# Revit family: ESTS-DOAS
name_source: partatom
category: Mechanical Equipment
revit_build: Autodesk Revit 2018 (Build: 20170223_1515(x64)
units: mm (PartAtom-declared; Revit-internal decimal feet)

## family parameters
Always vertical = Yes
Cut with Voids When Loaded = No
Part Type = Normal
Room Calculation Point = No
Round Connector Dimension = Use Radius
Shared = No
Work Plane-Based = No

## types (364) — shared parameters
Connect Dia = 7/8"
Connect V = 1 5/16"
Discharge Offset = 3"
Induct Filter C = 15 3/4"
Induct Filter Thickness = 2"
Induction C = 15"
Inlet Offset = 4"
Inlet S = 5 1/2"
Manufacturer = Anemostat
Pipe Radius = 7/16"

## per-type parameters (varying)
- ESTS/DOAS 1-hp - 16L W/2ROW & Filter: Connect H=1 7/16"; Connect Length=4 1/2"; Connector for 6ROW LS=No; Connector for 6ROW RS=No; Description=DOAS SERIES FAN POWERED AIR TERMINAL; Diameter=15 7/8"; Discharge Height "Y"=16"; Discharge Width "X"=19"; Duct Inlet=8"; Filter LH=No; Filter RH=Yes; Height=20"; Induct Center C=10"; Induct Center D=24"; Induct Filter D=41 3/4"; Induction D=41"; Inlet Left=Yes; Inlet Right=No; Length=48"; Model=ESTS/DOAS; Radius=7 15/16"; Row F=4"; Second Pipe H=1/8"; URL=https://www.anemostat-hvac.com; Width=48"
- ESTS/DOAS 3/4-hp - 14L W/2ROW & Filter: Connect H=1 7/16"; Connect Length=4 1/4"; Connector for 6ROW LS=No; Connector for 6ROW RS=No; Description=DOAS SERIES FAN POWERED AIR TERMINAL; Diameter=13 7/8"; Discharge Height "Y"=16"; Discharge Width "X"=19"; Duct Inlet=7"; Filter LH=No; Filter RH=Yes; Height=20"; Induct Center C=10"; Induct Center D=24"; Induct Filter D=41 3/4"; Induction D=41"; Inlet Left=Yes; Inlet Right=No; Length=48"; Model=ESTS/DOAS; Radius=6 15/16"; Row F=4"; Second Pipe H=1/8"; URL=https://www.anemostat-hvac.com; Width=48"
- ESTS/DOAS 1/2-hp - 14L W/2ROW & Filter: Connect H=1 7/16"; Connect Length=4 1/2"; Connector for 6ROW LS=No; Connector for 6ROW RS=No; Description=DOAS SERIES FAN POWERED AIR TERMINAL; Diameter=13 7/8"; Discharge Height "Y"=12"; Discharge Width "X"=14"; Duct Inlet=7"; Filter LH=No; Filter RH=Yes; Height=18"; Induct Center C=9"; Induct Center D=20"; Induct Filter D=33 3/4"; Induction D=33"; Inlet Left=Yes; Inlet Right=No; Length=40"; Model=ESTS/DOAS; Radius=6 15/16"; Row F=4"; Second Pipe H=1/8"; URL=https://www.anemostat-hvac.com; Width=40"
- ESTS/DOAS 1/3-hp - 10L W/2ROW & Filter: Connect H=1 7/16"; Connect Length=4 1/2"; Connector for 6ROW LS=No; Connector for 6ROW RS=No; Description=DOAS SERIES FAN POWERED AIR TERMINAL; Diameter=9 7/8"; Discharge Height "Y"=11"; Discharge Width "X"=11 1/2"; Duct Inlet=5"; Filter LH=No; Filter RH=Yes; Height=18"; Induct Center C=9"; Induct Center D=18"; Induct Filter D=29 3/4"; Induction D=29"; Inlet Left=Yes; Inlet Right=No; Length=36"; Model=ESTS/DOAS; Radius=4 15/16"; Row F=4"; Second Pipe H=1/8"; URL=https://www.anemostat-hvac.com; Width=32"
- ESTS/DOAS 3/4-hp - 14R W/2ROW & Filter: Connect H=1 7/16"; Connect Length=4 1/4"; Connector for 6ROW LS=No; Connector for 6ROW RS=No; Description=DOAS SERIES FAN POWERED AIR TERMINAL; Diameter=13 7/8"; Discharge Height "Y"=16"; Discharge Width "X"=19"; Duct Inlet=7"; Filter LH=Yes; Filter RH=No; Height=20"; Induct Center C=10"; Induct Center D=24"; Induct Filter D=41 3/4"; Induction D=41"; Inlet Left=No; Inlet Right=Yes; Length=48"; Model=ESTS/DOAS; Radius=6 15/16"; Row F=4"; Second Pipe H=1/8"; URL=https://www.anemostat-hvac.com; Width=48"
- ESTS/DOAS 1-hp - 16R W/2ROW & Filter: Connect H=1 5/16"; Connect Length=4 1/4"; Connector for 6ROW LS=No; Connector for 6ROW RS=No; Description=Series Fan Powered Air Terminal with ECM Motor; Diameter=15 7/8"; Discharge Height "Y"=16"; Discharge Width "X"=19"; Duct Inlet=8"; Filter LH=Yes; Filter RH=No; Height=20"; Induct Center C=10"; Induct Center D=24"; Induct Filter D=41 3/4"; Induction D=41"; Inlet Left=No; Inlet Right=Yes; Length=48"; Model=ESTS; Radius=7 15/16"; Row F=4"; Second Pipe H=1/8"; URL=http://www.anemostat.com; Width=48"
- ESTS/DOAS 1/3-hp - 10R W/2ROW & Filter: Connect H=1 7/16"; Connect Length=4 1/2"; Connector for 6ROW LS=No; Connector for 6ROW RS=No; Description=DOAS SERIES FAN POWERED AIR TERMINAL; Diameter=9 7/8"; Discharge Height "Y"=11"; Discharge Width "X"=11 1/2"; Duct Inlet=5"; Filter LH=Yes; Filter RH=No; Height=18"; Induct Center C=9"; Induct Center D=18"; Induct Filter D=29 3/4"; Induction D=29"; Inlet Left=No; Inlet Right=Yes; Length=36"; Model=ESTS/DOAS; Radius=4 15/16"; Row F=4"; Second Pipe H=1/8"; URL=https://www.anemostat-hvac.com; Width=32"
- ESTS/DOAS 1/2-hp - 14R W/2ROW & Filter: Connect H=1 7/16"; Connect Length=4 1/2"; Connector for 6ROW LS=No; Connector for 6ROW RS=No; Description=DOAS SERIES FAN POWERED AIR TERMINAL; Diameter=13 7/8"; Discharge Height "Y"=12"; Discharge Width "X"=14"; Duct Inlet=7"; Filter LH=Yes; Filter RH=No; Height=18"; Induct Center C=9"; Induct Center D=20"; Induct Filter D=33 3/4"; Induction D=33"; Inlet Left=No; Inlet Right=Yes; Length=40"; Model=ESTS/DOAS; Radius=6 15/16"; Row F=4"; Second Pipe H=1/8"; URL=https://www.anemostat-hvac.com; Width=40"
- ESTS/DOAS 1/3-hp - 09L W/2ROW & Filter: Connect H=1 7/16"; Connect Length=4 1/2"; Connector for 6ROW LS=No; Connector for 6ROW RS=No; Description=DOAS SERIES FAN POWERED AIR TERMINAL; Diameter=8 7/8"; Discharge Height "Y"=11"; Discharge Width "X"=11 1/2"; Duct Inlet=4"; Filter LH=No; Filter RH=Yes; Height=18"; Induct Center C=9"; Induct Center D=18"; Induct Filter D=29 3/4"; Induction D=29"; Inlet Left=Yes; Inlet Right=No; Length=36"; Model=ESTS/DOAS; Radius=4 7/16"; Row F=4"; Second Pipe H=1/8"; URL=https://www.anemostat-hvac.com; Width=32"
- ESTS/DOAS 1/3-hp - 08L W/2ROW & Filter: Connect H=1 7/16"; Connect Length=4 1/2"; Connector for 6ROW LS=No; Connector for 6ROW RS=No; Description=DOAS SERIES FAN POWERED AIR TERMINAL; Diameter=7 7/8"; Discharge Height "Y"=11"; Discharge Width "X"=11 1/2"; Duct Inlet=4"; Filter LH=No; Filter RH=Yes; Height=18"; Induct Center C=9"; Induct Center D=18"; Induct Filter D=29 3/4"; Induction D=29"; Inlet Left=Yes; Inlet Right=No; Length=36"; Model=ESTS/DOAS; Radius=3 15/16"; Row F=4"; Second Pipe H=1/8"; URL=https://www.anemostat-hvac.com; Width=32"
- ESTS/DOAS 1/3-hp - 07L W/2ROW & Filter: Connect H=1 7/16"; Connect Length=4 1/2"; Connector for 6ROW LS=No; Connector for 6ROW RS=No; Description=DOAS SERIES FAN POWERED AIR TERMINAL; Diameter=6 7/8"; Discharge Height "Y"=11"; Discharge Width "X"=11 1/2"; Duct Inlet=3"; Filter LH=No; Filter RH=Yes; Height=18"; Induct Center C=9"; Induct Center D=18"; Induct Filter D=29 3/4"; Induction D=29"; Inlet Left=Yes; Inlet Right=No; Length=36"; Model=ESTS/DOAS; Radius=3 7/16"; Row F=4"; Second Pipe H=1/8"; URL=https://www.anemostat-hvac.com; Width=32"
- ESTS/DOAS 1/3-hp - 06L W/2ROW & Filter: Connect H=1 7/16"; Connect Length=4 1/2"; Connector for 6ROW LS=No; Connector for 6ROW RS=No; Description=DOAS SERIES FAN POWERED AIR TERMINAL; Diameter=5 7/8"; Discharge Height "Y"=11"; Discharge Width "X"=11 1/2"; Duct Inlet=3"; Filter LH=No; Filter RH=Yes; Height=18"; Induct Center C=9"; Induct Center D=18"; Induct Filter D=29 3/4"; Induction D=29"; Inlet Left=Yes; Inlet Right=No; Length=36"; Model=ESTS/DOAS; Radius=2 15/16"; Row F=4"; Second Pipe H=1/8"; URL=https://www.anemostat-hvac.com; Width=32"
- ESTS/DOAS 1/3-hp - 05L W/2ROW & Filter: Connect H=1 7/16"; Connect Length=4 1/2"; Connector for 6ROW LS=No; Connector for 6ROW RS=No; Description=DOAS SERIES FAN POWERED AIR TERMINAL; Diameter=4 7/8"; Discharge Height "Y"=11"; Discharge Width "X"=11 1/2"; Duct Inlet=2"; Filter LH=No; Filter RH=Yes; Height=18"; Induct Center C=9"; Induct Center D=18"; Induct Filter D=29 3/4"; Induction D=29"; Inlet Left=Yes; Inlet Right=No; Length=36"; Model=ESTS/DOAS; Radius=2 7/16"; Row F=4"; Second Pipe H=1/8"; URL=https://www.anemostat-hvac.com; Width=32"
- ESTS/DOAS 1/3-hp - 09R W/2ROW & Filter: Connect H=1 7/16"; Connect Length=4 1/2"; Connector for 6ROW LS=No; Connector for 6ROW RS=No; Description=DOAS SERIES FAN POWERED AIR TERMINAL; Diameter=8 7/8"; Discharge Height "Y"=11"; Discharge Width "X"=11 1/2"; Duct Inlet=4"; Filter LH=Yes; Filter RH=No; Height=18"; Induct Center C=9"; Induct Center D=18"; Induct Filter D=29 3/4"; Induction D=29"; Inlet Left=No; Inlet Right=Yes; Length=36"; Model=ESTS/DOAS; Radius=4 7/16"; Row F=4"; Second Pipe H=1/8"; URL=https://www.anemostat-hvac.com; Width=32"
- ESTS/DOAS 1/3-hp - 08R W/2ROW & Filter: Connect H=1 7/16"; Connect Length=4 1/2"; Connector for 6ROW LS=No; Connector for 6ROW RS=No; Description=DOAS SERIES FAN POWERED AIR TERMINAL; Diameter=7 7/8"; Discharge Height "Y"=11"; Discharge Width "X"=11 1/2"; Duct Inlet=4"; Filter LH=Yes; Filter RH=No; Height=18"; Induct Center C=9"; Induct Center D=18"; Induct Filter D=29 3/4"; Induction D=29"; Inlet Left=No; Inlet Right=Yes; Length=36"; Model=ESTS/DOAS; Radius=3 15/16"; Row F=4"; Second Pipe H=1/8"; URL=https://www.anemostat-hvac.com; Width=32"
- ESTS/DOAS 1/3-hp - 07R W/2ROW & Filter: Connect H=1 7/16"; Connect Length=4 1/2"; Connector for 6ROW LS=No; Connector for 6ROW RS=No; Description=DOAS SERIES FAN POWERED AIR TERMINAL; Diameter=6 7/8"; Discharge Height "Y"=11"; Discharge Width "X"=11 1/2"; Duct Inlet=3"; Filter LH=Yes; Filter RH=No; Height=18"; Induct Center C=9"; Induct Center D=18"; Induct Filter D=29 3/4"; Induction D=29"; Inlet Left=No; Inlet Right=Yes; Length=36"; Model=ESTS/DOAS; Radius=3 7/16"; Row F=4"; Second Pipe H=1/8"; URL=https://www.anemostat-hvac.com; Width=32"
- ESTS/DOAS 1/3-hp - 06R W/2ROW & Filter: Connect H=1 7/16"; Connect Length=4 1/2"; Connector for 6ROW LS=No; Connector for 6ROW RS=No; Description=DOAS SERIES FAN POWERED AIR TERMINAL; Diameter=5 7/8"; Discharge Height "Y"=11"; Discharge Width "X"=11 1/2"; Duct Inlet=3"; Filter LH=Yes; Filter RH=No; Height=18"; Induct Center C=9"; Induct Center D=18"; Induct Filter D=29 3/4"; Induction D=29"; Inlet Left=No; Inlet Right=Yes; Length=36"; Model=ESTS/DOAS; Radius=2 15/16"; Row F=4"; Second Pipe H=1/8"; URL=https://www.anemostat-hvac.com; Width=32"
- ESTS/DOAS 1/3-hp - 05R W/2ROW & Filter: Connect H=1 7/16"; Connect Length=4 1/2"; Connector for 6ROW LS=No; Connector for 6ROW RS=No; Description=DOAS SERIES FAN POWERED AIR TERMINAL; Diameter=4 7/8"; Discharge Height "Y"=11"; Discharge Width "X"=11 1/2"; Duct Inlet=2"; Filter LH=Yes; Filter RH=No; Height=18"; Induct Center C=9"; Induct Center D=18"; Induct Filter D=29 3/4"; Induction D=29"; Inlet Left=No; Inlet Right=Yes; Length=36"; Model=ESTS/DOAS; Radius=2 7/16"; Row F=4"; Second Pipe H=1/8"; URL=https://www.anemostat-hvac.com; Width=32"
- ESTS/DOAS 1/2-hp - 14L W/2ROW NO Filter: Connect H=1 7/16"; Connect Length=4 1/2"; Connector for 6ROW LS=No; Connector for 6ROW RS=No; Description=DOAS SERIES FAN POWERED AIR TERMINAL; Diameter=13 7/8"; Discharge Height "Y"=12"; Discharge Width "X"=14"; Duct Inlet=7"; Filter LH=No; Filter RH=No; Height=18"; Induct Center C=9"; Induct Center D=20"; Induct Filter D=33 3/4"; Induction D=33"; Inlet Left=Yes; Inlet Right=No; Length=40"; Model=ESTS/DOAS; Radius=6 15/16"; Row F=4"; Second Pipe H=1/8"; URL=https://www.anemostat-hvac.com; Width=40"
- ESTS/DOAS 1/3-hp - 10R W/2ROW NO Filter: Connect H=1 7/16"; Connect Length=4 1/2"; Connector for 6ROW LS=No; Connector for 6ROW RS=No; Description=DOAS SERIES FAN POWERED AIR TERMINAL; Diameter=9 7/8"; Discharge Height "Y"=11"; Discharge Width "X"=11 1/2"; Duct Inlet=5"; Filter LH=No; Filter RH=No; Height=18"; Induct Center C=9"; Induct Center D=18"; Induct Filter D=29 3/4"; Induction D=29"; Inlet Left=No; Inlet Right=Yes; Length=36"; Model=ESTS/DOAS; Radius=4 15/16"; Row F=4"; Second Pipe H=1/8"; URL=https://www.anemostat-hvac.com; Width=32"
- ESTS/DOAS 1/3-hp - 10L W/2ROW NO Filter: Connect H=1 7/16"; Connect Length=4 1/2"; Connector for 6ROW LS=No; Connector for 6ROW RS=No; Description=DOAS SERIES FAN POWERED AIR TERMINAL; Diameter=9 7/8"; Discharge Height "Y"=11"; Discharge Width "X"=11 1/2"; Duct Inlet=5"; Filter LH=No; Filter RH=No; Height=18"; Induct Center C=9"; Induct Center D=18"; Induct Filter D=29 3/4"; Induction D=29"; Inlet Left=Yes; Inlet Right=No; Length=36"; Model=ESTS/DOAS; Radius=4 15/16"; Row F=4"; Second Pipe H=1/8"; URL=https://www.anemostat-hvac.com; Width=32"
- ESTS/DOAS 1/3-hp - 09R W/2ROW NO Filter: Connect H=1 7/16"; Connect Length=4 1/2"; Connector for 6ROW LS=No; Connector for 6ROW RS=No; Description=DOAS SERIES FAN POWERED AIR TERMINAL; Diameter=8 7/8"; Discharge Height "Y"=11"; Discharge Width "X"=11 1/2"; Duct Inlet=4"; Filter LH=No; Filter RH=No; Height=18"; Induct Center C=9"; Induct Center D=18"; Induct Filter D=29 3/4"; Induction D=29"; Inlet Left=No; Inlet Right=Yes; Length=36"; Model=ESTS/DOAS; Radius=4 7/16"; Row F=4"; Second Pipe H=1/8"; URL=https://www.anemostat-hvac.com; Width=32"
- ESTS/DOAS 1/3-hp - 09L W/2ROW NO Filter: Connect H=1 7/16"; Connect Length=4 1/2"; Connector for 6ROW LS=No; Connector for 6ROW RS=No; Description=DOAS SERIES FAN POWERED AIR TERMINAL; Diameter=8 7/8"; Discharge Height "Y"=11"; Discharge Width "X"=11 1/2"; Duct Inlet=4"; Filter LH=No; Filter RH=No; Height=18"; Induct Center C=9"; Induct Center D=18"; Induct Filter D=29 3/4"; Induction D=29"; Inlet Left=Yes; Inlet Right=No; Length=36"; Model=ESTS/DOAS; Radius=4 7/16"; Row F=4"; Second Pipe H=1/8"; URL=https://www.anemostat-hvac.com; Width=32"
- ESTS/DOAS 1/3-hp - 08R W/2ROW NO Filter: Connect H=1 7/16"; Connect Length=4 1/2"; Connector for 6ROW LS=No; Connector for 6ROW RS=No; Description=DOAS SERIES FAN POWERED AIR TERMINAL; Diameter=7 7/8"; Discharge Height "Y"=11"; Discharge Width "X"=11 1/2"; Duct Inlet=4"; Filter LH=No; Filter RH=No; Height=18"; Induct Center C=9"; Induct Center D=18"; Induct Filter D=29 3/4"; Induction D=29"; Inlet Left=No; Inlet Right=Yes; Length=36"; Model=ESTS/DOAS; Radius=3 15/16"; Row F=4"; Second Pipe H=1/8"; URL=https://www.anemostat-hvac.com; Width=32"
- ESTS/DOAS 1/3-hp - 08L W/2ROW NO Filter: Connect H=1 7/16"; Connect Length=4 1/2"; Connector for 6ROW LS=No; Connector for 6ROW RS=No; Description=DOAS SERIES FAN POWERED AIR TERMINAL; Diameter=7 7/8"; Discharge Height "Y"=11"; Discharge Width "X"=11 1/2"; Duct Inlet=4"; Filter LH=No; Filter RH=No; Height=18"; Induct Center C=9"; Induct Center D=18"; Induct Filter D=29 3/4"; Induction D=29"; Inlet Left=Yes; Inlet Right=No; Length=36"; Model=ESTS/DOAS; Radius=3 15/16"; Row F=4"; Second Pipe H=1/8"; URL=https://www.anemostat-hvac.com; Width=32"
- ESTS/DOAS 1/3-hp - 07R W/2ROW NO Filter: Connect H=1 7/16"; Connect Length=4 1/2"; Connector for 6ROW LS=No; Connector for 6ROW RS=No; Description=DOAS SERIES FAN POWERED AIR TERMINAL; Diameter=6 7/8"; Discharge Height "Y"=11"; Discharge Width "X"=11 1/2"; Duct Inlet=3"; Filter LH=No; Filter RH=No; Height=18"; Induct Center C=9"; Induct Center D=18"; Induct Filter D=29 3/4"; Induction D=29"; Inlet Left=No; Inlet Right=Yes; Length=36"; Model=ESTS/DOAS; Radius=3 7/16"; Row F=4"; Second Pipe H=1/8"; URL=https://www.anemostat-hvac.com; Width=32"
- ESTS/DOAS 1/3-hp - 07L W/2ROW NO Filter: Connect H=1 7/16"; Connect Length=4 1/2"; Connector for 6ROW LS=No; Connector for 6ROW RS=No; Description=DOAS SERIES FAN POWERED AIR TERMINAL; Diameter=6 7/8"; Discharge Height "Y"=11"; Discharge Width "X"=11 1/2"; Duct Inlet=3"; Filter LH=No; Filter RH=No; Height=18"; Induct Center C=9"; Induct Center D=18"; Induct Filter D=29 3/4"; Induction D=29"; Inlet Left=Yes; Inlet Right=No; Length=36"; Model=ESTS/DOAS; Radius=3 7/16"; Row F=4"; Second Pipe H=1/8"; URL=https://www.anemostat-hvac.com; Width=32"
- ESTS/DOAS 1/3-hp - 06R W/2ROW NO Filter: Connect H=1 7/16"; Connect Length=4 1/2"; Connector for 6ROW LS=No; Connector for 6ROW RS=No; Description=DOAS SERIES FAN POWERED AIR TERMINAL; Diameter=5 7/8"; Discharge Height "Y"=11"; Discharge Width "X"=11 1/2"; Duct Inlet=3"; Filter LH=No; Filter RH=No; Height=18"; Induct Center C=9"; Induct Center D=18"; Induct Filter D=29 3/4"; Induction D=29"; Inlet Left=No; Inlet Right=Yes; Length=36"; Model=ESTS/DOAS; Radius=2 15/16"; Row F=4"; Second Pipe H=1/8"; URL=https://www.anemostat-hvac.com; Width=32"
- ESTS/DOAS 1/3-hp - 06L W/2ROW NO Filter: Connect H=1 7/16"; Connect Length=4 1/2"; Connector for 6ROW LS=No; Connector for 6ROW RS=No; Description=DOAS SERIES FAN POWERED AIR TERMINAL; Diameter=5 7/8"; Discharge Height "Y"=11"; Discharge Width "X"=11 1/2"; Duct Inlet=3"; Filter LH=No; Filter RH=No; Height=18"; Induct Center C=9"; Induct Center D=18"; Induct Filter D=29 3/4"; Induction D=29"; Inlet Left=Yes; Inlet Right=No; Length=36"; Model=ESTS/DOAS; Radius=2 15/16"; Row F=4"; Second Pipe H=1/8"; URL=https://www.anemostat-hvac.com; Width=32"
- ESTS/DOAS 1/3-hp - 05R W/2ROW NO Filter: Connect H=1 7/16"; Connect Length=4 1/2"; Connector for 6ROW LS=No; Connector for 6ROW RS=No; Description=DOAS SERIES FAN POWERED AIR TERMINAL; Diameter=4 7/8"; Discharge Height "Y"=11"; Discharge Width "X"=11 1/2"; Duct Inlet=2"; Filter LH=No; Filter RH=No; Height=18"; Induct Center C=9"; Induct Center D=18"; Induct Filter D=29 3/4"; Induction D=29"; Inlet Left=No; Inlet Right=Yes; Length=36"; Model=ESTS/DOAS; Radius=2 7/16"; Row F=4"; Second Pipe H=1/8"; URL=https://www.anemostat-hvac.com; Width=32"
- ESTS/DOAS 1/3-hp - 05L W/2ROW NO Filter: Connect H=1 7/16"; Connect Length=4 1/2"; Connector for 6ROW LS=No; Connector for 6ROW RS=No; Description=DOAS SERIES FAN POWERED AIR TERMINAL; Diameter=4 7/8"; Discharge Height "Y"=11"; Discharge Width "X"=11 1/2"; Duct Inlet=2"; Filter LH=No; Filter RH=No; Height=18"; Induct Center C=9"; Induct Center D=18"; Induct Filter D=29 3/4"; Induction D=29"; Inlet Left=Yes; Inlet Right=No; Length=36"; Model=ESTS/DOAS; Radius=2 7/16"; Row F=4"; Second Pipe H=1/8"; URL=https://www.anemostat-hvac.com; Width=32"
- ESTS/DOAS 1/2-hp - 14R W/2ROW NO Filter: Connect H=1 7/16"; Connect Length=4 1/2"; Connector for 6ROW LS=No; Connector for 6ROW RS=No; Description=DOAS SERIES FAN POWERED AIR TERMINAL; Diameter=13 7/8"; Discharge Height "Y"=12"; Discharge Width "X"=14"; Duct Inlet=7"; Filter LH=No; Filter RH=No; Height=18"; Induct Center C=9"; Induct Center D=20"; Induct Filter D=33 3/4"; Induction D=33"; Inlet Left=No; Inlet Right=Yes; Length=40"; Model=ESTS/DOAS; Radius=6 15/16"; Row F=4"; Second Pipe H=1/8"; URL=https://www.anemostat-hvac.com; Width=40"
- ESTS/DOAS 3/4-hp - 14R W/2ROW NO Filter: Connect H=1 7/16"; Connect Length=4 1/4"; Connector for 6ROW LS=No; Connector for 6ROW RS=No; Description=DOAS SERIES FAN POWERED AIR TERMINAL; Diameter=13 7/8"; Discharge Height "Y"=16"; Discharge Width "X"=19"; Duct Inlet=7"; Filter LH=No; Filter RH=No; Height=20"; Induct Center C=10"; Induct Center D=24"; Induct Filter D=41 3/4"; Induction D=41"; Inlet Left=No; Inlet Right=Yes; Length=48"; Model=ESTS/DOAS; Radius=6 15/16"; Row F=4"; Second Pipe H=1/8"; URL=https://www.anemostat-hvac.com; Width=48"
- ESTS/DOAS 3/4-hp - 14L W/2ROW NO Filter: Connect H=1 7/16"; Connect Length=4 1/4"; Connector for 6ROW LS=No; Connector for 6ROW RS=Yes; Description=DOAS SERIES FAN POWERED AIR TERMINAL; Diameter=13 7/8"; Discharge Height "Y"=16"; Discharge Width "X"=19"; Duct Inlet=7"; Filter LH=No; Filter RH=No; Height=20"; Induct Center C=10"; Induct Center D=24"; Induct Filter D=41 3/4"; Induction D=41"; Inlet Left=Yes; Inlet Right=No; Length=48"; Model=ESTS/DOAS; Radius=6 15/16"; Row F=4"; Second Pipe H=1/8"; URL=https://www.anemostat-hvac.com; Width=48"
- ESTS/DOAS 1-hp - 16R W/2ROW NO Filter: Connect H=1 5/16"; Connect Length=4 1/4"; Connector for 6ROW LS=No; Connector for 6ROW RS=No; Description=Series Fan Powered Air Terminal with ECM Motor; Diameter=15 7/8"; Discharge Height "Y"=16"; Discharge Width "X"=19"; Duct Inlet=8"; Filter LH=No; Filter RH=No; Height=20"; Induct Center C=10"; Induct Center D=24"; Induct Filter D=41 3/4"; Induction D=41"; Inlet Left=No; Inlet Right=Yes; Length=48"; Model=ESTS; Radius=7 15/16"; Row F=4"; Second Pipe H=1/8"; URL=http://www.anemostat.com; Width=48"
- ESTS/DOAS 1-hp - 14L W/2ROW NO Filter: Connect H=1 7/16"; Connect Length=4 1/4"; Connector for 6ROW LS=No; Connector for 6ROW RS=No; Description=DOAS SERIES FAN POWERED AIR TERMINAL; Diameter=13 7/8"; Discharge Height "Y"=16"; Discharge Width "X"=19"; Duct Inlet=7"; Filter LH=No; Filter RH=No; Height=20"; Induct Center C=10"; Induct Center D=24"; Induct Filter D=41 3/4"; Induction D=41"; Inlet Left=Yes; Inlet Right=No; Length=48"; Model=ESTS/DOAS; Radius=6 15/16"; Row F=4"; Second Pipe H=1/8"; URL=https://www.anemostat-hvac.com; Width=48"
- ESTS/DOAS 1-hp - 12L W/2ROW NO Filter: Connect H=1 7/16"; Connect Length=4 1/2"; Connector for 6ROW LS=No; Connector for 6ROW RS=No; Description=DOAS SERIES FAN POWERED AIR TERMINAL; Diameter=11 7/8"; Discharge Height "Y"=16"; Discharge Width "X"=19"; Duct Inlet=6"; Filter LH=No; Filter RH=No; Height=20"; Induct Center C=10"; Induct Center D=24"; Induct Filter D=41 3/4"; Induction D=41"; Inlet Left=Yes; Inlet Right=No; Length=48"; Model=ESTS/DOAS; Radius=5 15/16"; Row F=4"; Second Pipe H=1/8"; URL=https://www.anemostat-hvac.com; Width=48"
- ESTS/DOAS 1-hp - 14L W/2ROW & Filter: Connect H=1 7/16"; Connect Length=4 1/2"; Connector for 6ROW LS=No; Connector for 6ROW RS=No; Description=DOAS SERIES FAN POWERED AIR TERMINAL; Diameter=13 7/8"; Discharge Height "Y"=16"; Discharge Width "X"=19"; Duct Inlet=7"; Filter LH=No; Filter RH=Yes; Height=20"; Induct Center C=10"; Induct Center D=24"; Induct Filter D=41 3/4"; Induction D=41"; Inlet Left=Yes; Inlet Right=No; Length=48"; Model=ESTS/DOAS; Radius=6 15/16"; Row F=4"; Second Pipe H=1/8"; URL=https://www.anemostat-hvac.com; Width=48"
- ESTS/DOAS 1-hp - 12L W/2ROW & Filter: Connect H=1 7/16"; Connect Length=4 1/2"; Connector for 6ROW LS=No; Connector for 6ROW RS=No; Description=DOAS SERIES FAN POWERED AIR TERMINAL; Diameter=11 7/8"; Discharge Height "Y"=16"; Discharge Width "X"=19"; Duct Inlet=6"; Filter LH=No; Filter RH=Yes; Height=20"; Induct Center C=10"; Induct Center D=24"; Induct Filter D=41 3/4"; Induction D=41"; Inlet Left=Yes; Inlet Right=No; Length=48"; Model=ESTS/DOAS; Radius=5 15/16"; Row F=4"; Second Pipe H=1/8"; URL=https://www.anemostat-hvac.com; Width=48"
- ESTS/DOAS 1-hp - 14R W/2ROW & Filter: Connect H=1 5/16"; Connect Length=4 1/4"; Connector for 6ROW LS=No; Connector for 6ROW RS=No; Description=Series Fan Powered Air Terminal with ECM Motor; Diameter=13 7/8"; Discharge Height "Y"=16"; Discharge Width "X"=19"; Duct Inlet=7"; Filter LH=Yes; Filter RH=No; Height=20"; Induct Center C=10"; Induct Center D=24"; Induct Filter D=41 3/4"; Induction D=41"; Inlet Left=No; Inlet Right=Yes; Length=48"; Model=ESTS; Radius=6 15/16"; Row F=4"; Second Pipe H=1/8"; URL=http://www.anemostat.com; Width=48"
- ESTS/DOAS 1-hp - 12R W/2ROW & Filter: Connect H=1 5/16"; Connect Length=4 1/4"; Connector for 6ROW LS=No; Connector for 6ROW RS=No; Description=Series Fan Powered Air Terminal with ECM Motor; Diameter=11 7/8"; Discharge Height "Y"=16"; Discharge Width "X"=19"; Duct Inlet=6"; Filter LH=Yes; Filter RH=No; Height=20"; Induct Center C=10"; Induct Center D=24"; Induct Filter D=41 3/4"; Induction D=41"; Inlet Left=No; Inlet Right=Yes; Length=48"; Model=ESTS; Radius=5 15/16"; Row F=4"; Second Pipe H=1/8"; URL=http://www.anemostat.com; Width=48"
- ESTS/DOAS 1-hp - 10R W/2ROW & Filter: Connect H=1 5/16"; Connect Length=4 1/4"; Connector for 6ROW LS=No; Connector for 6ROW RS=No; Description=Series Fan Powered Air Terminal with ECM Motor; Diameter=9 7/8"; Discharge Height "Y"=16"; Discharge Width "X"=19"; Duct Inlet=5"; Filter LH=Yes; Filter RH=No; Height=20"; Induct Center C=10"; Induct Center D=24"; Induct Filter D=41 3/4"; Induction D=41"; Inlet Left=No; Inlet Right=Yes; Length=48"; Model=ESTS; Radius=4 15/16"; Row F=4"; Second Pipe H=1/8"; URL=http://www.anemostat.com; Width=48"
- ESTS/DOAS 1-hp - 09R W/2ROW & Filter: Connect H=1 5/16"; Connect Length=4 1/4"; Connector for 6ROW LS=No; Connector for 6ROW RS=No; Description=Series Fan Powered Air Terminal with ECM Motor; Diameter=8 7/8"; Discharge Height "Y"=16"; Discharge Width "X"=19"; Duct Inlet=4"; Filter LH=Yes; Filter RH=No; Height=20"; Induct Center C=10"; Induct Center D=24"; Induct Filter D=41 3/4"; Induction D=41"; Inlet Left=No; Inlet Right=Yes; Length=48"; Model=ESTS; Radius=4 7/16"; Row F=4"; Second Pipe H=1/8"; URL=http://www.anemostat.com; Width=48"
- ESTS/DOAS 1-hp - 08R W/2ROW & Filter: Connect H=1 5/16"; Connect Length=4 1/4"; Connector for 6ROW LS=No; Connector for 6ROW RS=No; Description=Series Fan Powered Air Terminal with ECM Motor; Diameter=7 7/8"; Discharge Height "Y"=16"; Discharge Width "X"=19"; Duct Inlet=4"; Filter LH=Yes; Filter RH=No; Height=20"; Induct Center C=10"; Induct Center D=24"; Induct Filter D=41 3/4"; Induction D=41"; Inlet Left=No; Inlet Right=Yes; Length=48"; Model=ESTS; Radius=3 15/16"; Row F=4"; Second Pipe H=1/8"; URL=http://www.anemostat.com; Width=48"
- ESTS/DOAS 1-hp - 07R W/2ROW & Filter: Connect H=1 5/16"; Connect Length=4 1/4"; Connector for 6ROW LS=No; Connector for 6ROW RS=No; Description=Series Fan Powered Air Terminal with ECM Motor; Diameter=6 7/8"; Discharge Height "Y"=16"; Discharge Width "X"=19"; Duct Inlet=3"; Filter LH=Yes; Filter RH=No; Height=20"; Induct Center C=10"; Induct Center D=24"; Induct Filter D=41 3/4"; Induction D=41"; Inlet Left=No; Inlet Right=Yes; Length=48"; Model=ESTS; Radius=3 7/16"; Row F=4"; Second Pipe H=1/8"; URL=http://www.anemostat.com; Width=48"
- ESTS/DOAS 1-hp - 06R W/2ROW & Filter: Connect H=1 5/16"; Connect Length=4 1/4"; Connector for 6ROW LS=No; Connector for 6ROW RS=No; Description=Series Fan Powered Air Terminal with ECM Motor; Diameter=5 7/8"; Discharge Height "Y"=16"; Discharge Width "X"=19"; Duct Inlet=3"; Filter LH=Yes; Filter RH=No; Height=20"; Induct Center C=10"; Induct Center D=24"; Induct Filter D=41 3/4"; Induction D=41"; Inlet Left=No; Inlet Right=Yes; Length=48"; Model=ESTS; Radius=2 15/16"; Row F=4"; Second Pipe H=1/8"; URL=http://www.anemostat.com; Width=48"
- ESTS/DOAS 1-hp - 05R W/2ROW & Filter: Connect H=1 5/16"; Connect Length=4 1/4"; Connector for 6ROW LS=No; Connector for 6ROW RS=No; Description=Series Fan Powered Air Terminal with ECM Motor; Diameter=4 7/8"; Discharge Height "Y"=16"; Discharge Width "X"=19"; Duct Inlet=2"; Filter LH=No; Filter RH=Yes; Height=20"; Induct Center C=10"; Induct Center D=24"; Induct Filter D=41 3/4"; Induction D=41"; Inlet Left=No; Inlet Right=Yes; Length=48"; Model=ESTS; Radius=2 7/16"; Row F=4"; Second Pipe H=1/8"; URL=http://www.anemostat.com; Width=48"
- ESTS/DOAS 1-hp - 14R W/2ROW NO Filter: Connect H=1 5/16"; Connect Length=4 1/4"; Connector for 6ROW LS=No; Connector for 6ROW RS=No; Description=Series Fan Powered Air Terminal with ECM Motor; Diameter=13 7/8"; Discharge Height "Y"=16"; Discharge Width "X"=19"; Duct Inlet=7"; Filter LH=No; Filter RH=No; Height=20"; Induct Center C=10"; Induct Center D=24"; Induct Filter D=41 3/4"; Induction D=41"; Inlet Left=No; Inlet Right=Yes; Length=48"; Model=ESTS; Radius=6 15/16"; Row F=4"; Second Pipe H=1/8"; URL=http://www.anemostat.com; Width=48"
- ESTS/DOAS 1-hp - 12R W/2ROW NO Filter: Connect H=1 5/16"; Connect Length=4 1/4"; Connector for 6ROW LS=No; Connector for 6ROW RS=No; Description=Series Fan Powered Air Terminal with ECM Motor; Diameter=11 7/8"; Discharge Height "Y"=16"; Discharge Width "X"=19"; Duct Inlet=6"; Filter LH=No; Filter RH=No; Height=20"; Induct Center C=10"; Induct Center D=24"; Induct Filter D=41 3/4"; Induction D=41"; Inlet Left=No; Inlet Right=Yes; Length=48"; Model=ESTS; Radius=5 15/16"; Row F=4"; Second Pipe H=1/8"; URL=http://www.anemostat.com; Width=48"
- ESTS/DOAS 1-hp - 10R W/2ROW NO Filter: Connect H=1 5/16"; Connect Length=4 1/4"; Connector for 6ROW LS=No; Connector for 6ROW RS=No; Description=Series Fan Powered Air Terminal with ECM Motor; Diameter=9 7/8"; Discharge Height "Y"=16"; Discharge Width "X"=19"; Duct Inlet=5"; Filter LH=No; Filter RH=No; Height=20"; Induct Center C=10"; Induct Center D=24"; Induct Filter D=41 3/4"; Induction D=41"; Inlet Left=No; Inlet Right=Yes; Length=48"; Model=ESTS; Radius=4 15/16"; Row F=4"; Second Pipe H=1/8"; URL=http://www.anemostat.com; Width=48"
- ESTS/DOAS 1-hp - 09R W/2ROW NO Filter: Connect H=1 5/16"; Connect Length=4 1/4"; Connector for 6ROW LS=No; Connector for 6ROW RS=No; Description=Series Fan Powered Air Terminal with ECM Motor; Diameter=8 7/8"; Discharge Height "Y"=16"; Discharge Width "X"=19"; Duct Inlet=4"; Filter LH=No; Filter RH=No; Height=20"; Induct Center C=10"; Induct Center D=24"; Induct Filter D=41 3/4"; Induction D=41"; Inlet Left=No; Inlet Right=Yes; Length=48"; Model=ESTS; Radius=4 7/16"; Row F=4"; Second Pipe H=1/8"; URL=http://www.anemostat.com; Width=48"
- ESTS/DOAS 1-hp - 08R W/2ROW NO Filter: Connect H=1 5/16"; Connect Length=4 1/4"; Connector for 6ROW LS=No; Connector for 6ROW RS=No; Description=Series Fan Powered Air Terminal with ECM Motor; Diameter=7 7/8"; Discharge Height "Y"=16"; Discharge Width "X"=19"; Duct Inlet=4"; Filter LH=No; Filter RH=No; Height=20"; Induct Center C=10"; Induct Center D=24"; Induct Filter D=41 3/4"; Induction D=41"; Inlet Left=No; Inlet Right=Yes; Length=48"; Model=ESTS; Radius=3 15/16"; Row F=4"; Second Pipe H=1/8"; URL=http://www.anemostat.com; Width=48"
- ESTS/DOAS 1-hp - 07R W/2ROW NO Filter: Connect H=1 5/16"; Connect Length=4 1/4"; Connector for 6ROW LS=No; Connector for 6ROW RS=No; Description=Series Fan Powered Air Terminal with ECM Motor; Diameter=6 7/8"; Discharge Height "Y"=16"; Discharge Width "X"=19"; Duct Inlet=3"; Filter LH=No; Filter RH=No; Height=20"; Induct Center C=10"; Induct Center D=24"; Induct Filter D=41 3/4"; Induction D=41"; Inlet Left=No; Inlet Right=Yes; Length=48"; Model=ESTS; Radius=3 7/16"; Row F=4"; Second Pipe H=1/8"; URL=http://www.anemostat.com; Width=48"
- ESTS/DOAS 1-hp - 06R W/2ROW NO Filter: Connect H=1 5/16"; Connect Length=4 1/4"; Connector for 6ROW LS=No; Connector for 6ROW RS=No; Description=Series Fan Powered Air Terminal with ECM Motor; Diameter=5 7/8"; Discharge Height "Y"=16"; Discharge Width "X"=19"; Duct Inlet=3"; Filter LH=No; Filter RH=No; Height=20"; Induct Center C=10"; Induct Center D=24"; Induct Filter D=41 3/4"; Induction D=41"; Inlet Left=No; Inlet Right=Yes; Length=48"; Model=ESTS; Radius=2 15/16"; Row F=4"; Second Pipe H=1/8"; URL=http://www.anemostat.com; Width=48"
- ESTS/DOAS 1-hp - 05R W/2ROW NO Filter: Connect H=1 5/16"; Connect Length=4 1/4"; Connector for 6ROW LS=No; Connector for 6ROW RS=No; Description=Series Fan Powered Air Terminal with ECM Motor; Diameter=4 7/8"; Discharge Height "Y"=16"; Discharge Width "X"=19"; Duct Inlet=2"; Filter LH=No; Filter RH=No; Height=20"; Induct Center C=10"; Induct Center D=24"; Induct Filter D=41 3/4"; Induction D=41"; Inlet Left=No; Inlet Right=Yes; Length=48"; Model=ESTS; Radius=2 7/16"; Row F=4"; Second Pipe H=1/8"; URL=http://www.anemostat.com; Width=48"
- ESTS/DOAS 3/4-hp - 12L W/2ROW NO Filter: Connect H=1 7/16"; Connect Length=4 1/4"; Connector for 6ROW LS=No; Connector for 6ROW RS=No; Description=DOAS SERIES FAN POWERED AIR TERMINAL; Diameter=11 7/8"; Discharge Height "Y"=16"; Discharge Width "X"=19"; Duct Inlet=6"; Filter LH=No; Filter RH=No; Height=20"; Induct Center C=10"; Induct Center D=24"; Induct Filter D=41 3/4"; Induction D=41"; Inlet Left=Yes; Inlet Right=No; Length=48"; Model=ESTS/DOAS; Radius=5 15/16"; Row F=4"; Second Pipe H=1/8"; URL=https://www.anemostat-hvac.com; Width=48"
- ESTS/DOAS 3/4-hp - 10L W/2ROW NO Filter: Connect H=1 7/16"; Connect Length=4 1/4"; Connector for 6ROW LS=No; Connector for 6ROW RS=No; Description=DOAS SERIES FAN POWERED AIR TERMINAL; Diameter=9 7/8"; Discharge Height "Y"=16"; Discharge Width "X"=19"; Duct Inlet=5"; Filter LH=No; Filter RH=No; Height=20"; Induct Center C=10"; Induct Center D=24"; Induct Filter D=41 3/4"; Induction D=41"; Inlet Left=Yes; Inlet Right=No; Length=48"; Model=ESTS/DOAS; Radius=4 15/16"; Row F=4"; Second Pipe H=1/8"; URL=https://www.anemostat-hvac.com; Width=48"
- ESTS/DOAS 3/4-hp - 09L W/2ROW NO Filter: Connect H=1 7/16"; Connect Length=4 1/4"; Connector for 6ROW LS=No; Connector for 6ROW RS=Yes; Description=DOAS SERIES FAN POWERED AIR TERMINAL; Diameter=8 7/8"; Discharge Height "Y"=16"; Discharge Width "X"=19"; Duct Inlet=4"; Filter LH=No; Filter RH=No; Height=20"; Induct Center C=10"; Induct Center D=24"; Induct Filter D=41 3/4"; Induction D=41"; Inlet Left=Yes; Inlet Right=No; Length=48"; Model=ESTS/DOAS; Radius=4 7/16"; Row F=4"; Second Pipe H=1/8"; URL=https://www.anemostat-hvac.com; Width=48"
- ESTS/DOAS 3/4-hp - 08L W/2ROW NO Filter: Connect H=1 7/16"; Connect Length=4 1/4"; Connector for 6ROW LS=No; Connector for 6ROW RS=No; Description=DOAS SERIES FAN POWERED AIR TERMINAL; Diameter=7 7/8"; Discharge Height "Y"=16"; Discharge Width "X"=19"; Duct Inlet=4"; Filter LH=No; Filter RH=No; Height=20"; Induct Center C=10"; Induct Center D=24"; Induct Filter D=41 3/4"; Induction D=41"; Inlet Left=Yes; Inlet Right=No; Length=48"; Model=ESTS/DOAS; Radius=3 15/16"; Row F=4"; Second Pipe H=1/8"; URL=https://www.anemostat-hvac.com; Width=48"
- ESTS/DOAS 3/4-hp - 07L W/2ROW NO Filter: Connect H=1 7/16"; Connect Length=4 1/4"; Connector for 6ROW LS=No; Connector for 6ROW RS=No; Description=DOAS SERIES FAN POWERED AIR TERMINAL; Diameter=6 7/8"; Discharge Height "Y"=16"; Discharge Width "X"=19"; Duct Inlet=3"; Filter LH=No; Filter RH=No; Height=20"; Induct Center C=10"; Induct Center D=24"; Induct Filter D=41 3/4"; Induction D=41"; Inlet Left=Yes; Inlet Right=No; Length=48"; Model=ESTS/DOAS; Radius=3 7/16"; Row F=4"; Second Pipe H=1/8"; URL=https://www.anemostat-hvac.com; Width=48"
- ESTS/DOAS 3/4-hp - 06L W/2ROW NO Filter: Connect H=1 7/16"; Connect Length=4 1/4"; Connector for 6ROW LS=No; Connector for 6ROW RS=No; Description=DOAS SERIES FAN POWERED AIR TERMINAL; Diameter=5 7/8"; Discharge Height "Y"=16"; Discharge Width "X"=19"; Duct Inlet=3"; Filter LH=No; Filter RH=No; Height=20"; Induct Center C=10"; Induct Center D=24"; Induct Filter D=41 3/4"; Induction D=41"; Inlet Left=Yes; Inlet Right=No; Length=48"; Model=ESTS/DOAS; Radius=2 15/16"; Row F=4"; Second Pipe H=1/8"; URL=https://www.anemostat-hvac.com; Width=48"
- ESTS/DOAS 3/4-hp - 05L W/2ROW NO Filter: Connect H=1 7/16"; Connect Length=4 1/4"; Connector for 6ROW LS=No; Connector for 6ROW RS=No; Description=DOAS SERIES FAN POWERED AIR TERMINAL; Diameter=4 7/8"; Discharge Height "Y"=16"; Discharge Width "X"=19"; Duct Inlet=2"; Filter LH=No; Filter RH=No; Height=20"; Induct Center C=10"; Induct Center D=24"; Induct Filter D=41 3/4"; Induction D=41"; Inlet Left=Yes; Inlet Right=No; Length=48"; Model=ESTS/DOAS; Radius=2 7/16"; Row F=4"; Second Pipe H=1/8"; URL=https://www.anemostat-hvac.com; Width=48"
- ESTS/DOAS 3/4-hp - 12L W/2ROW & Filter: Connect H=1 7/16"; Connect Length=4 1/4"; Connector for 6ROW LS=No; Connector for 6ROW RS=No; Description=DOAS SERIES FAN POWERED AIR TERMINAL; Diameter=11 7/8"; Discharge Height "Y"=16"; Discharge Width "X"=19"; Duct Inlet=6"; Filter LH=No; Filter RH=Yes; Height=20"; Induct Center C=10"; Induct Center D=24"; Induct Filter D=41 3/4"; Induction D=41"; Inlet Left=Yes; Inlet Right=No; Length=48"; Model=ESTS/DOAS; Radius=5 15/16"; Row F=4"; Second Pipe H=1/8"; URL=https://www.anemostat-hvac.com; Width=48"
- ESTS/DOAS 3/4-hp - 10L W/2ROW & Filter: Connect H=1 7/16"; Connect Length=4 1/4"; Connector for 6ROW LS=No; Connector for 6ROW RS=No; Description=DOAS SERIES FAN POWERED AIR TERMINAL; Diameter=9 7/8"; Discharge Height "Y"=16"; Discharge Width "X"=19"; Duct Inlet=5"; Filter LH=No; Filter RH=Yes; Height=20"; Induct Center C=10"; Induct Center D=24"; Induct Filter D=41 3/4"; Induction D=41"; Inlet Left=Yes; Inlet Right=No; Length=48"; Model=ESTS/DOAS; Radius=4 15/16"; Row F=4"; Second Pipe H=1/8"; URL=https://www.anemostat-hvac.com; Width=48"
- ESTS/DOAS 3/4-hp - 09L W/2ROW & Filter: Connect H=1 7/16"; Connect Length=4 1/4"; Connector for 6ROW LS=No; Connector for 6ROW RS=No; Description=DOAS SERIES FAN POWERED AIR TERMINAL; Diameter=8 7/8"; Discharge Height "Y"=16"; Discharge Width "X"=19"; Duct Inlet=4"; Filter LH=No; Filter RH=Yes; Height=20"; Induct Center C=10"; Induct Center D=24"; Induct Filter D=41 3/4"; Induction D=41"; Inlet Left=Yes; Inlet Right=No; Length=48"; Model=ESTS/DOAS; Radius=4 7/16"; Row F=4"; Second Pipe H=1/8"; URL=https://www.anemostat-hvac.com; Width=48"
- ESTS/DOAS 3/4-hp - 08L W/2ROW & Filter: Connect H=1 7/16"; Connect Length=4 1/4"; Connector for 6ROW LS=No; Connector for 6ROW RS=No; Description=DOAS SERIES FAN POWERED AIR TERMINAL; Diameter=7 7/8"; Discharge Height "Y"=16"; Discharge Width "X"=19"; Duct Inlet=4"; Filter LH=No; Filter RH=Yes; Height=20"; Induct Center C=10"; Induct Center D=24"; Induct Filter D=41 3/4"; Induction D=41"; Inlet Left=Yes; Inlet Right=No; Length=48"; Model=ESTS/DOAS; Radius=3 15/16"; Row F=4"; Second Pipe H=1/8"; URL=https://www.anemostat-hvac.com; Width=48"
- ESTS/DOAS 3/4-hp - 07L W/2ROW & Filter: Connect H=1 7/16"; Connect Length=4 1/4"; Connector for 6ROW LS=No; Connector for 6ROW RS=No; Description=DOAS SERIES FAN POWERED AIR TERMINAL; Diameter=6 7/8"; Discharge Height "Y"=16"; Discharge Width "X"=19"; Duct Inlet=3"; Filter LH=No; Filter RH=Yes; Height=20"; Induct Center C=10"; Induct Center D=24"; Induct Filter D=41 3/4"; Induction D=41"; Inlet Left=Yes; Inlet Right=No; Length=48"; Model=ESTS/DOAS; Radius=3 7/16"; Row F=4"; Second Pipe H=1/8"; URL=https://www.anemostat-hvac.com; Width=48"
- ESTS/DOAS 3/4-hp - 06L W/2ROW & Filter: Connect H=1 7/16"; Connect Length=4 1/4"; Connector for 6ROW LS=No; Connector for 6ROW RS=No; Description=DOAS SERIES FAN POWERED AIR TERMINAL; Diameter=5 7/8"; Discharge Height "Y"=16"; Discharge Width "X"=19"; Duct Inlet=3"; Filter LH=No; Filter RH=Yes; Height=20"; Induct Center C=10"; Induct Center D=24"; Induct Filter D=41 3/4"; Induction D=41"; Inlet Left=Yes; Inlet Right=No; Length=48"; Model=ESTS/DOAS; Radius=2 15/16"; Row F=4"; Second Pipe H=1/8"; URL=https://www.anemostat-hvac.com; Width=48"
- ESTS/DOAS 3/4-hp - 05L W/2ROW & Filter: Connect H=1 7/16"; Connect Length=4 1/4"; Connector for 6ROW LS=No; Connector for 6ROW RS=No; Description=DOAS SERIES FAN POWERED AIR TERMINAL; Diameter=4 7/8"; Discharge Height "Y"=16"; Discharge Width "X"=19"; Duct Inlet=2"; Filter LH=No; Filter RH=Yes; Height=20"; Induct Center C=10"; Induct Center D=24"; Induct Filter D=41 3/4"; Induction D=41"; Inlet Left=Yes; Inlet Right=No; Length=48"; Model=ESTS/DOAS; Radius=2 7/16"; Row F=4"; Second Pipe H=1/8"; URL=https://www.anemostat-hvac.com; Width=48"
- ESTS/DOAS 1/2-hp - 12L W/2ROW & Filter: Connect H=1 7/16"; Connect Length=4 1/2"; Connector for 6ROW LS=No; Connector for 6ROW RS=No; Description=DOAS SERIES FAN POWERED AIR TERMINAL; Diameter=11 7/8"; Discharge Height "Y"=12"; Discharge Width "X"=14"; Duct Inlet=6"; Filter LH=No; Filter RH=Yes; Height=18"; Induct Center C=9"; Induct Center D=20"; Induct Filter D=33 3/4"; Induction D=33"; Inlet Left=Yes; Inlet Right=No; Length=40"; Model=ESTS/DOAS; Radius=5 15/16"; Row F=4"; Second Pipe H=1/8"; URL=https://www.anemostat-hvac.com; Width=40"
- ESTS/DOAS 1/2-hp - 10L W/2ROW & Filter: Connect H=1 7/16"; Connect Length=4 1/2"; Connector for 6ROW LS=No; Connector for 6ROW RS=No; Description=DOAS SERIES FAN POWERED AIR TERMINAL; Diameter=9 7/8"; Discharge Height "Y"=12"; Discharge Width "X"=14"; Duct Inlet=5"; Filter LH=No; Filter RH=Yes; Height=18"; Induct Center C=9"; Induct Center D=20"; Induct Filter D=33 3/4"; Induction D=33"; Inlet Left=Yes; Inlet Right=No; Length=40"; Model=ESTS/DOAS; Radius=4 15/16"; Row F=4"; Second Pipe H=1/8"; URL=https://www.anemostat-hvac.com; Width=40"
- ESTS/DOAS 1/2-hp - 09L W/2ROW & Filter: Connect H=1 7/16"; Connect Length=4 1/2"; Connector for 6ROW LS=No; Connector for 6ROW RS=No; Description=DOAS SERIES FAN POWERED AIR TERMINAL; Diameter=8 7/8"; Discharge Height "Y"=12"; Discharge Width "X"=14"; Duct Inlet=4"; Filter LH=No; Filter RH=Yes; Height=18"; Induct Center C=9"; Induct Center D=20"; Induct Filter D=33 3/4"; Induction D=33"; Inlet Left=Yes; Inlet Right=No; Length=40"; Model=ESTS/DOAS; Radius=4 7/16"; Row F=4"; Second Pipe H=1/8"; URL=https://www.anemostat-hvac.com; Width=40"
- ESTS/DOAS 1/2-hp - 08L W/2ROW & Filter: Connect H=1 7/16"; Connect Length=4 1/2"; Connector for 6ROW LS=No; Connector for 6ROW RS=No; Description=DOAS SERIES FAN POWERED AIR TERMINAL; Diameter=7 7/8"; Discharge Height "Y"=12"; Discharge Width "X"=14"; Duct Inlet=4"; Filter LH=No; Filter RH=Yes; Height=18"; Induct Center C=9"; Induct Center D=20"; Induct Filter D=33 3/4"; Induction D=33"; Inlet Left=Yes; Inlet Right=No; Length=40"; Model=ESTS/DOAS; Radius=3 15/16"; Row F=4"; Second Pipe H=1/8"; URL=https://www.anemostat-hvac.com; Width=40"
- ESTS/DOAS 1/2-hp - 07L W/2ROW & Filter: Connect H=1 7/16"; Connect Length=4 1/2"; Connector for 6ROW LS=No; Connector for 6ROW RS=No; Description=DOAS SERIES FAN POWERED AIR TERMINAL; Diameter=6 7/8"; Discharge Height "Y"=12"; Discharge Width "X"=14"; Duct Inlet=3"; Filter LH=No; Filter RH=Yes; Height=18"; Induct Center C=9"; Induct Center D=20"; Induct Filter D=33 3/4"; Induction D=33"; Inlet Left=Yes; Inlet Right=No; Length=40"; Model=ESTS/DOAS; Radius=3 7/16"; Row F=4"; Second Pipe H=1/8"; URL=https://www.anemostat-hvac.com; Width=40"
- ESTS/DOAS 1/2-hp - 06L W/2ROW & Filter: Connect H=1 7/16"; Connect Length=4 1/2"; Connector for 6ROW LS=No; Connector for 6ROW RS=No; Description=DOAS SERIES FAN POWERED AIR TERMINAL; Diameter=5 7/8"; Discharge Height "Y"=12"; Discharge Width "X"=14"; Duct Inlet=3"; Filter LH=No; Filter RH=Yes; Height=18"; Induct Center C=9"; Induct Center D=20"; Induct Filter D=33 3/4"; Induction D=33"; Inlet Left=Yes; Inlet Right=No; Length=40"; Model=ESTS/DOAS; Radius=2 15/16"; Row F=4"; Second Pipe H=1/8"; URL=https://www.anemostat-hvac.com; Width=40"
- ESTS/DOAS 1/2-hp - 05L W/2ROW & Filter: Connect H=1 7/16"; Connect Length=4 1/2"; Connector for 6ROW LS=No; Connector for 6ROW RS=No; Description=DOAS SERIES FAN POWERED AIR TERMINAL; Diameter=4 7/8"; Discharge Height "Y"=12"; Discharge Width "X"=14"; Duct Inlet=2"; Filter LH=No; Filter RH=Yes; Height=18"; Induct Center C=9"; Induct Center D=20"; Induct Filter D=33 3/4"; Induction D=33"; Inlet Left=Yes; Inlet Right=No; Length=40"; Model=ESTS/DOAS; Radius=2 7/16"; Row F=4"; Second Pipe H=1/8"; URL=https://www.anemostat-hvac.com; Width=40"
- ESTS/DOAS 1/2-hp - 12L W/2ROW NO Filter: Connect H=1 7/16"; Connect Length=4 1/2"; Connector for 6ROW LS=No; Connector for 6ROW RS=No; Description=DOAS SERIES FAN POWERED AIR TERMINAL; Diameter=11 7/8"; Discharge Height "Y"=12"; Discharge Width "X"=14"; Duct Inlet=6"; Filter LH=No; Filter RH=No; Height=18"; Induct Center C=9"; Induct Center D=20"; Induct Filter D=33 3/4"; Induction D=33"; Inlet Left=Yes; Inlet Right=No; Length=40"; Model=ESTS/DOAS; Radius=5 15/16"; Row F=4"; Second Pipe H=1/8"; URL=https://www.anemostat-hvac.com; Width=40"
- ESTS/DOAS 1/2-hp - 10L W/2ROW NO Filter: Connect H=1 7/16"; Connect Length=4 1/2"; Connector for 6ROW LS=No; Connector for 6ROW RS=No; Description=DOAS SERIES FAN POWERED AIR TERMINAL; Diameter=9 7/8"; Discharge Height "Y"=12"; Discharge Width "X"=14"; Duct Inlet=5"; Filter LH=No; Filter RH=No; Height=18"; Induct Center C=9"; Induct Center D=20"; Induct Filter D=33 3/4"; Induction D=33"; Inlet Left=Yes; Inlet Right=No; Length=40"; Model=ESTS/DOAS; Radius=4 15/16"; Row F=4"; Second Pipe H=1/8"; URL=https://www.anemostat-hvac.com; Width=40"
- ESTS/DOAS 1/2-hp - 09L W/2ROW NO Filter: Connect H=1 7/16"; Connect Length=4 1/2"; Connector for 6ROW LS=No; Connector for 6ROW RS=No; Description=DOAS SERIES FAN POWERED AIR TERMINAL; Diameter=8 7/8"; Discharge Height "Y"=12"; Discharge Width "X"=14"; Duct Inlet=4"; Filter LH=No; Filter RH=No; Height=18"; Induct Center C=9"; Induct Center D=20"; Induct Filter D=33 3/4"; Induction D=33"; Inlet Left=Yes; Inlet Right=No; Length=40"; Model=ESTS/DOAS; Radius=4 7/16"; Row F=4"; Second Pipe H=1/8"; URL=https://www.anemostat-hvac.com; Width=40"
- ESTS/DOAS 1/2-hp - 08L W/2ROW NO Filter: Connect H=1 7/16"; Connect Length=4 1/2"; Connector for 6ROW LS=No; Connector for 6ROW RS=No; Description=DOAS SERIES FAN POWERED AIR TERMINAL; Diameter=7 7/8"; Discharge Height "Y"=12"; Discharge Width "X"=14"; Duct Inlet=4"; Filter LH=No; Filter RH=No; Height=18"; Induct Center C=9"; Induct Center D=20"; Induct Filter D=33 3/4"; Induction D=33"; Inlet Left=Yes; Inlet Right=No; Length=40"; Model=ESTS/DOAS; Radius=3 15/16"; Row F=4"; Second Pipe H=1/8"; URL=https://www.anemostat-hvac.com; Width=40"
- ESTS/DOAS 1/2-hp - 07L W/2ROW NO Filter: Connect H=1 7/16"; Connect Length=4 1/2"; Connector for 6ROW LS=No; Connector for 6ROW RS=No; Description=DOAS SERIES FAN POWERED AIR TERMINAL; Diameter=6 7/8"; Discharge Height "Y"=12"; Discharge Width "X"=14"; Duct Inlet=3"; Filter LH=No; Filter RH=No; Height=18"; Induct Center C=9"; Induct Center D=20"; Induct Filter D=33 3/4"; Induction D=33"; Inlet Left=Yes; Inlet Right=No; Length=40"; Model=ESTS/DOAS; Radius=3 7/16"; Row F=4"; Second Pipe H=1/8"; URL=https://www.anemostat-hvac.com; Width=40"
- ESTS/DOAS 1/2-hp - 06L W/2ROW NO Filter: Connect H=1 7/16"; Connect Length=4 1/2"; Connector for 6ROW LS=No; Connector for 6ROW RS=No; Description=DOAS SERIES FAN POWERED AIR TERMINAL; Diameter=5 7/8"; Discharge Height "Y"=12"; Discharge Width "X"=14"; Duct Inlet=3"; Filter LH=No; Filter RH=No; Height=18"; Induct Center C=9"; Induct Center D=20"; Induct Filter D=33 3/4"; Induction D=33"; Inlet Left=Yes; Inlet Right=No; Length=40"; Model=ESTS/DOAS; Radius=2 15/16"; Row F=4"; Second Pipe H=1/8"; URL=https://www.anemostat-hvac.com; Width=40"
- ESTS/DOAS 1/2-hp - 05L W/2ROW NO Filter: Connect H=1 7/16"; Connect Length=4 1/2"; Connector for 6ROW LS=No; Connector for 6ROW RS=No; Description=DOAS SERIES FAN POWERED AIR TERMINAL; Diameter=4 7/8"; Discharge Height "Y"=12"; Discharge Width "X"=14"; Duct Inlet=2"; Filter LH=No; Filter RH=No; Height=18"; Induct Center C=9"; Induct Center D=20"; Induct Filter D=33 3/4"; Induction D=33"; Inlet Left=Yes; Inlet Right=No; Length=40"; Model=ESTS/DOAS; Radius=2 7/16"; Row F=4"; Second Pipe H=1/8"; URL=https://www.anemostat-hvac.com; Width=40"
- ESTS/DOAS 1/2-hp - 12R W/2ROW & Filter: Connect H=1 7/16"; Connect Length=4 1/2"; Connector for 6ROW LS=No; Connector for 6ROW RS=No; Description=DOAS SERIES FAN POWERED AIR TERMINAL; Diameter=11 7/8"; Discharge Height "Y"=12"; Discharge Width "X"=14"; Duct Inlet=6"; Filter LH=Yes; Filter RH=No; Height=18"; Induct Center C=9"; Induct Center D=20"; Induct Filter D=33 3/4"; Induction D=33"; Inlet Left=No; Inlet Right=Yes; Length=40"; Model=ESTS/DOAS; Radius=5 15/16"; Row F=4"; Second Pipe H=1/8"; URL=https://www.anemostat-hvac.com; Width=40"
- ESTS/DOAS 1/2-hp - 10R W/2ROW & Filter: Connect H=1 7/16"; Connect Length=4 1/2"; Connector for 6ROW LS=No; Connector for 6ROW RS=No; Description=DOAS SERIES FAN POWERED AIR TERMINAL; Diameter=9 7/8"; Discharge Height "Y"=12"; Discharge Width "X"=14"; Duct Inlet=5"; Filter LH=Yes; Filter RH=No; Height=18"; Induct Center C=9"; Induct Center D=20"; Induct Filter D=33 3/4"; Induction D=33"; Inlet Left=No; Inlet Right=Yes; Length=40"; Model=ESTS/DOAS; Radius=4 15/16"; Row F=4"; Second Pipe H=1/8"; URL=https://www.anemostat-hvac.com; Width=40"
- ESTS/DOAS 1/2-hp - 09R W/2ROW & Filter: Connect H=1 7/16"; Connect Length=4 1/2"; Connector for 6ROW LS=No; Connector for 6ROW RS=No; Description=DOAS SERIES FAN POWERED AIR TERMINAL; Diameter=8 7/8"; Discharge Height "Y"=12"; Discharge Width "X"=14"; Duct Inlet=4"; Filter LH=Yes; Filter RH=No; Height=18"; Induct Center C=9"; Induct Center D=20"; Induct Filter D=33 3/4"; Induction D=33"; Inlet Left=No; Inlet Right=Yes; Length=40"; Model=ESTS/DOAS; Radius=4 7/16"; Row F=4"; Second Pipe H=1/8"; URL=https://www.anemostat-hvac.com; Width=40"
- ESTS/DOAS 1/2-hp - 08R W/2ROW & Filter: Connect H=1 7/16"; Connect Length=4 1/2"; Connector for 6ROW LS=No; Connector for 6ROW RS=No; Description=DOAS SERIES FAN POWERED AIR TERMINAL; Diameter=7 7/8"; Discharge Height "Y"=12"; Discharge Width "X"=14"; Duct Inlet=4"; Filter LH=Yes; Filter RH=No; Height=18"; Induct Center C=9"; Induct Center D=20"; Induct Filter D=33 3/4"; Induction D=33"; Inlet Left=No; Inlet Right=Yes; Length=40"; Model=ESTS/DOAS; Radius=3 15/16"; Row F=4"; Second Pipe H=1/8"; URL=https://www.anemostat-hvac.com; Width=40"
- ESTS/DOAS 1/2-hp - 07R W/2ROW & Filter: Connect H=1 7/16"; Connect Length=4 1/2"; Connector for 6ROW LS=No; Connector for 6ROW RS=No; Description=DOAS SERIES FAN POWERED AIR TERMINAL; Diameter=6 7/8"; Discharge Height "Y"=12"; Discharge Width "X"=14"; Duct Inlet=3"; Filter LH=Yes; Filter RH=No; Height=18"; Induct Center C=9"; Induct Center D=20"; Induct Filter D=33 3/4"; Induction D=33"; Inlet Left=No; Inlet Right=Yes; Length=40"; Model=ESTS/DOAS; Radius=3 7/16"; Row F=4"; Second Pipe H=1/8"; URL=https://www.anemostat-hvac.com; Width=40"
- ESTS/DOAS 1/2-hp - 06R W/2ROW & Filter: Connect H=1 7/16"; Connect Length=4 1/2"; Connector for 6ROW LS=No; Connector for 6ROW RS=No; Description=DOAS SERIES FAN POWERED AIR TERMINAL; Diameter=5 7/8"; Discharge Height "Y"=12"; Discharge Width "X"=14"; Duct Inlet=3"; Filter LH=Yes; Filter RH=No; Height=18"; Induct Center C=9"; Induct Center D=20"; Induct Filter D=33 3/4"; Induction D=33"; Inlet Left=No; Inlet Right=Yes; Length=40"; Model=ESTS/DOAS; Radius=2 15/16"; Row F=4"; Second Pipe H=1/8"; URL=https://www.anemostat-hvac.com; Width=40"
- ESTS/DOAS 1/2-hp - 05R W/2ROW & Filter: Connect H=1 7/16"; Connect Length=4 1/2"; Connector for 6ROW LS=No; Connector for 6ROW RS=No; Description=DOAS SERIES FAN POWERED AIR TERMINAL; Diameter=4 7/8"; Discharge Height "Y"=12"; Discharge Width "X"=14"; Duct Inlet=2"; Filter LH=Yes; Filter RH=No; Height=18"; Induct Center C=9"; Induct Center D=20"; Induct Filter D=33 3/4"; Induction D=33"; Inlet Left=No; Inlet Right=Yes; Length=40"; Model=ESTS/DOAS; Radius=2 7/16"; Row F=4"; Second Pipe H=1/8"; URL=https://www.anemostat-hvac.com; Width=40"
- ESTS/DOAS 1/2-hp - 12R W/2ROW NO Filter: Connect H=1 7/16"; Connect Length=4 1/2"; Connector for 6ROW LS=No; Connector for 6ROW RS=No; Description=DOAS SERIES FAN POWERED AIR TERMINAL; Diameter=11 7/8"; Discharge Height "Y"=12"; Discharge Width "X"=14"; Duct Inlet=6"; Filter LH=No; Filter RH=No; Height=18"; Induct Center C=9"; Induct Center D=20"; Induct Filter D=33 3/4"; Induction D=33"; Inlet Left=No; Inlet Right=Yes; Length=40"; Model=ESTS/DOAS; Radius=5 15/16"; Row F=4"; Second Pipe H=1/8"; URL=https://www.anemostat-hvac.com; Width=40"
- ESTS/DOAS 1/2-hp - 10R W/2ROW NO Filter: Connect H=1 7/16"; Connect Length=4 1/2"; Connector for 6ROW LS=No; Connector for 6ROW RS=No; Description=DOAS SERIES FAN POWERED AIR TERMINAL; Diameter=9 7/8"; Discharge Height "Y"=12"; Discharge Width "X"=14"; Duct Inlet=5"; Filter LH=No; Filter RH=No; Height=18"; Induct Center C=9"; Induct Center D=20"; Induct Filter D=33 3/4"; Induction D=33"; Inlet Left=No; Inlet Right=Yes; Length=40"; Model=ESTS/DOAS; Radius=4 15/16"; Row F=4"; Second Pipe H=1/8"; URL=https://www.anemostat-hvac.com; Width=40"
- ESTS/DOAS 1/2-hp - 09R W/2ROW NO Filter: Connect H=1 7/16"; Connect Length=4 1/2"; Connector for 6ROW LS=No; Connector for 6ROW RS=No; Description=DOAS SERIES FAN POWERED AIR TERMINAL; Diameter=8 7/8"; Discharge Height "Y"=12"; Discharge Width "X"=14"; Duct Inlet=4"; Filter LH=No; Filter RH=No; Height=18"; Induct Center C=9"; Induct Center D=20"; Induct Filter D=33 3/4"; Induction D=33"; Inlet Left=No; Inlet Right=Yes; Length=40"; Model=ESTS/DOAS; Radius=4 7/16"; Row F=4"; Second Pipe H=1/8"; URL=https://www.anemostat-hvac.com; Width=40"
- ESTS/DOAS 1/2-hp - 08R W/2ROW NO Filter: Connect H=1 7/16"; Connect Length=4 1/2"; Connector for 6ROW LS=No; Connector for 6ROW RS=No; Description=DOAS SERIES FAN POWERED AIR TERMINAL; Diameter=7 7/8"; Discharge Height "Y"=12"; Discharge Width "X"=14"; Duct Inlet=4"; Filter LH=No; Filter RH=No; Height=18"; Induct Center C=9"; Induct Center D=20"; Induct Filter D=33 3/4"; Induction D=33"; Inlet Left=No; Inlet Right=Yes; Length=40"; Model=ESTS/DOAS; Radius=3 15/16"; Row F=4"; Second Pipe H=1/8"; URL=https://www.anemostat-hvac.com; Width=40"
- ESTS/DOAS 1/2-hp - 07R W/2ROW NO Filter: Connect H=1 7/16"; Connect Length=4 1/2"; Connector for 6ROW LS=No; Connector for 6ROW RS=No; Description=DOAS SERIES FAN POWERED AIR TERMINAL; Diameter=6 7/8"; Discharge Height "Y"=12"; Discharge Width "X"=14"; Duct Inlet=3"; Filter LH=No; Filter RH=No; Height=18"; Induct Center C=9"; Induct Center D=20"; Induct Filter D=33 3/4"; Induction D=33"; Inlet Left=No; Inlet Right=Yes; Length=40"; Model=ESTS/DOAS; Radius=3 7/16"; Row F=4"; Second Pipe H=1/8"; URL=https://www.anemostat-hvac.com; Width=40"
- ESTS/DOAS 1/2-hp - 06R W/2ROW NO Filter: Connect H=1 7/16"; Connect Length=4 1/2"; Connector for 6ROW LS=No; Connector for 6ROW RS=No; Description=DOAS SERIES FAN POWERED AIR TERMINAL; Diameter=5 7/8"; Discharge Height "Y"=12"; Discharge Width "X"=14"; Duct Inlet=3"; Filter LH=No; Filter RH=No; Height=18"; Induct Center C=9"; Induct Center D=20"; Induct Filter D=33 3/4"; Induction D=33"; Inlet Left=No; Inlet Right=Yes; Length=40"; Model=ESTS/DOAS; Radius=2 15/16"; Row F=4"; Second Pipe H=1/8"; URL=https://www.anemostat-hvac.com; Width=40"
- ESTS/DOAS 1/2-hp - 05R W/2ROW NO Filter: Connect H=1 7/16"; Connect Length=4 1/2"; Connector for 6ROW LS=No; Connector for 6ROW RS=No; Description=DOAS SERIES FAN POWERED AIR TERMINAL; Diameter=4 7/8"; Discharge Height "Y"=12"; Discharge Width "X"=14"; Duct Inlet=2"; Filter LH=No; Filter RH=No; Height=18"; Induct Center C=9"; Induct Center D=20"; Induct Filter D=33 3/4"; Induction D=33"; Inlet Left=No; Inlet Right=Yes; Length=40"; Model=ESTS/DOAS; Radius=2 7/16"; Row F=4"; Second Pipe H=1/8"; URL=https://www.anemostat-hvac.com; Width=40"
- ESTS/DOAS 3/4-hp - 14R W/4ROW NO Filter: Connect H=1 7/16"; Connect Length=4 1/4"; Connector for 6ROW LS=No; Connector for 6ROW RS=No; Description=DOAS SERIES FAN POWERED AIR TERMINAL; Diameter=13 7/8"; Discharge Height "Y"=16"; Discharge Width "X"=19"; Duct Inlet=7"; Filter LH=No; Filter RH=No; Height=20"; Induct Center C=10"; Induct Center D=24"; Induct Filter D=41 3/4"; Induction D=41"; Inlet Left=No; Inlet Right=Yes; Length=48"; Model=ESTS/DOAS; Radius=6 15/16"; Row F=6"; Second Pipe H=2 1/8"; URL=https://www.anemostat-hvac.com; Width=48"
- ESTS/DOAS 3/4-hp - 14R W/4ROW & Filter: Connect H=1 7/16"; Connect Length=4 1/4"; Connector for 6ROW LS=No; Connector for 6ROW RS=No; Description=DOAS SERIES FAN POWERED AIR TERMINAL; Diameter=13 7/8"; Discharge Height "Y"=16"; Discharge Width "X"=19"; Duct Inlet=7"; Filter LH=Yes; Filter RH=No; Height=20"; Induct Center C=10"; Induct Center D=24"; Induct Filter D=41 3/4"; Induction D=41"; Inlet Left=No; Inlet Right=Yes; Length=48"; Model=ESTS/DOAS; Radius=6 15/16"; Row F=6"; Second Pipe H=2 1/8"; URL=https://www.anemostat-hvac.com; Width=48"
- ESTS/DOAS 3/4-hp - 14L W/4ROW NO Filter: Connect H=1 7/16"; Connect Length=4 1/4"; Connector for 6ROW LS=No; Connector for 6ROW RS=No; Description=DOAS SERIES FAN POWERED AIR TERMINAL; Diameter=13 7/8"; Discharge Height "Y"=16"; Discharge Width "X"=19"; Duct Inlet=7"; Filter LH=No; Filter RH=No; Height=20"; Induct Center C=10"; Induct Center D=24"; Induct Filter D=41 3/4"; Induction D=41"; Inlet Left=Yes; Inlet Right=No; Length=48"; Model=ESTS/DOAS; Radius=6 15/16"; Row F=6"; Second Pipe H=2 1/8"; URL=https://www.anemostat-hvac.com; Width=48"
- ESTS/DOAS 3/4-hp - 14L W/6ROW NO Filter: Connect H=1 7/16"; Connect Length=4 1/4"; Connector for 6ROW LS=No; Connector for 6ROW RS=Yes; Description=DOAS SERIES FAN POWERED AIR TERMINAL; Diameter=13 7/8"; Discharge Height "Y"=16"; Discharge Width "X"=19"; Duct Inlet=7"; Filter LH=No; Filter RH=No; Height=20"; Induct Center C=10"; Induct Center D=24"; Induct Filter D=41 3/4"; Induction D=41"; Inlet Left=Yes; Inlet Right=No; Length=48"; Model=ESTS/DOAS; Radius=6 15/16"; Row F=8"; Second Pipe H=4 1/8"; URL=https://www.anemostat-hvac.com; Width=48"
- ESTS/DOAS 3/4-hp - 14R W/6ROW NO Filter: Connect H=1 7/16"; Connect Length=4 1/4"; Connector for 6ROW LS=Yes; Connector for 6ROW RS=No; Description=DOAS SERIES FAN POWERED AIR TERMINAL; Diameter=13 7/8"; Discharge Height "Y"=16"; Discharge Width "X"=19"; Duct Inlet=7"; Filter LH=No; Filter RH=No; Height=20"; Induct Center C=10"; Induct Center D=24"; Induct Filter D=41 3/4"; Induction D=41"; Inlet Left=No; Inlet Right=Yes; Length=48"; Model=ESTS/DOAS; Radius=6 15/16"; Row F=8"; Second Pipe H=4 1/8"; URL=https://www.anemostat-hvac.com; Width=48"
- ESTS/DOAS 3/4-hp - 14R W/6ROW & Filter: Connect H=1 7/16"; Connect Length=4 1/4"; Connector for 6ROW LS=Yes; Connector for 6ROW RS=No; Description=DOAS SERIES FAN POWERED AIR TERMINAL; Diameter=13 7/8"; Discharge Height "Y"=16"; Discharge Width "X"=19"; Duct Inlet=7"; Filter LH=Yes; Filter RH=No; Height=20"; Induct Center C=10"; Induct Center D=24"; Induct Filter D=41 3/4"; Induction D=41"; Inlet Left=No; Inlet Right=Yes; Length=48"; Model=ESTS/DOAS; Radius=6 15/16"; Row F=8"; Second Pipe H=4 1/8"; URL=https://www.anemostat-hvac.com; Width=48"
- ESTS/DOAS 3/4-hp - 14L W/4ROW & Filter: Connect H=1 7/16"; Connect Length=4 1/4"; Connector for 6ROW LS=No; Connector for 6ROW RS=No; Description=DOAS SERIES FAN POWERED AIR TERMINAL; Diameter=13 7/8"; Discharge Height "Y"=16"; Discharge Width "X"=19"; Duct Inlet=7"; Filter LH=No; Filter RH=Yes; Height=20"; Induct Center C=10"; Induct Center D=24"; Induct Filter D=41 3/4"; Induction D=41"; Inlet Left=Yes; Inlet Right=No; Length=48"; Model=ESTS/DOAS; Radius=6 15/16"; Row F=6"; Second Pipe H=2 1/8"; URL=https://www.anemostat-hvac.com; Width=48"
- ESTS/DOAS 3/4-hp - 14L W/6ROW & Filter: Connect H=1 7/16"; Connect Length=4 1/4"; Connector for 6ROW LS=No; Connector for 6ROW RS=Yes; Description=DOAS SERIES FAN POWERED AIR TERMINAL; Diameter=13 7/8"; Discharge Height "Y"=16"; Discharge Width "X"=19"; Duct Inlet=7"; Filter LH=No; Filter RH=Yes; Height=20"; Induct Center C=10"; Induct Center D=24"; Induct Filter D=41 3/4"; Induction D=41"; Inlet Left=Yes; Inlet Right=No; Length=48"; Model=ESTS/DOAS; Radius=6 15/16"; Row F=8"; Second Pipe H=4 1/8"; URL=https://www.anemostat-hvac.com; Width=48"
- ESTS/DOAS 3/4-hp - 12L W/4ROW & Filter: Connect H=1 7/16"; Connect Length=4 1/4"; Connector for 6ROW LS=No; Connector for 6ROW RS=No; Description=DOAS SERIES FAN POWERED AIR TERMINAL; Diameter=11 7/8"; Discharge Height "Y"=16"; Discharge Width "X"=19"; Duct Inlet=6"; Filter LH=No; Filter RH=Yes; Height=20"; Induct Center C=10"; Induct Center D=24"; Induct Filter D=41 3/4"; Induction D=41"; Inlet Left=Yes; Inlet Right=No; Length=48"; Model=ESTS/DOAS; Radius=5 15/16"; Row F=6"; Second Pipe H=2 1/8"; URL=https://www.anemostat-hvac.com; Width=48"
- ESTS/DOAS 3/4-hp - 12L W/6ROW & Filter: Connect H=1 7/16"; Connect Length=4 1/4"; Connector for 6ROW LS=No; Connector for 6ROW RS=Yes; Description=DOAS SERIES FAN POWERED AIR TERMINAL; Diameter=11 7/8"; Discharge Height "Y"=16"; Discharge Width "X"=19"; Duct Inlet=6"; Filter LH=No; Filter RH=Yes; Height=20"; Induct Center C=10"; Induct Center D=24"; Induct Filter D=41 3/4"; Induction D=41"; Inlet Left=Yes; Inlet Right=No; Length=48"; Model=ESTS/DOAS; Radius=5 15/16"; Row F=8"; Second Pipe H=4 1/8"; URL=https://www.anemostat-hvac.com; Width=48"
- ESTS/DOAS 3/4-hp - 12L W/4ROW NO Filter: Connect H=1 7/16"; Connect Length=4 1/4"; Connector for 6ROW LS=No; Connector for 6ROW RS=No; Description=DOAS SERIES FAN POWERED AIR TERMINAL; Diameter=11 7/8"; Discharge Height "Y"=16"; Discharge Width "X"=19"; Duct Inlet=6"; Filter LH=No; Filter RH=No; Height=20"; Induct Center C=10"; Induct Center D=24"; Induct Filter D=41 3/4"; Induction D=41"; Inlet Left=Yes; Inlet Right=No; Length=48"; Model=ESTS/DOAS; Radius=5 15/16"; Row F=6"; Second Pipe H=2 1/8"; URL=https://www.anemostat-hvac.com; Width=48"
- ESTS/DOAS 3/4-hp - 12L W/6ROW NO Filter: Connect H=1 7/16"; Connect Length=4 1/4"; Connector for 6ROW LS=No; Connector for 6ROW RS=Yes; Description=DOAS SERIES FAN POWERED AIR TERMINAL; Diameter=11 7/8"; Discharge Height "Y"=16"; Discharge Width "X"=19"; Duct Inlet=6"; Filter LH=No; Filter RH=No; Height=20"; Induct Center C=10"; Induct Center D=24"; Induct Filter D=41 3/4"; Induction D=41"; Inlet Left=Yes; Inlet Right=No; Length=48"; Model=ESTS/DOAS; Radius=5 15/16"; Row F=8"; Second Pipe H=4 1/8"; URL=https://www.anemostat-hvac.com; Width=48"
- ESTS/DOAS 3/4-hp - 12R W/2ROW & Filter: Connect H=1 7/16"; Connect Length=4 1/4"; Connector for 6ROW LS=No; Connector for 6ROW RS=No; Description=DOAS SERIES FAN POWERED AIR TERMINAL; Diameter=11 7/8"; Discharge Height "Y"=16"; Discharge Width "X"=19"; Duct Inlet=6"; Filter LH=Yes; Filter RH=No; Height=20"; Induct Center C=10"; Induct Center D=24"; Induct Filter D=41 3/4"; Induction D=41"; Inlet Left=No; Inlet Right=Yes; Length=48"; Model=ESTS/DOAS; Radius=5 15/16"; Row F=4"; Second Pipe H=1/8"; URL=https://www.anemostat-hvac.com; Width=48"
- ESTS/DOAS 3/4-hp - 12R W/4ROW & Filter: Connect H=1 7/16"; Connect Length=4 1/4"; Connector for 6ROW LS=No; Connector for 6ROW RS=No; Description=DOAS SERIES FAN POWERED AIR TERMINAL; Diameter=11 7/8"; Discharge Height "Y"=16"; Discharge Width "X"=19"; Duct Inlet=6"; Filter LH=Yes; Filter RH=No; Height=20"; Induct Center C=10"; Induct Center D=24"; Induct Filter D=41 3/4"; Induction D=41"; Inlet Left=No; Inlet Right=Yes; Length=48"; Model=ESTS/DOAS; Radius=5 15/16"; Row F=6"; Second Pipe H=2 1/8"; URL=https://www.anemostat-hvac.com; Width=48"
- ESTS/DOAS 3/4-hp - 12R W/6ROW & Filter: Connect H=1 7/16"; Connect Length=4 1/4"; Connector for 6ROW LS=Yes; Connector for 6ROW RS=No; Description=DOAS SERIES FAN POWERED AIR TERMINAL; Diameter=11 7/8"; Discharge Height "Y"=16"; Discharge Width "X"=19"; Duct Inlet=6"; Filter LH=Yes; Filter RH=No; Height=20"; Induct Center C=10"; Induct Center D=24"; Induct Filter D=41 3/4"; Induction D=41"; Inlet Left=No; Inlet Right=Yes; Length=48"; Model=ESTS/DOAS; Radius=5 15/16"; Row F=8"; Second Pipe H=4 1/8"; URL=https://www.anemostat-hvac.com; Width=48"
- ESTS/DOAS 3/4-hp - 12R W/2ROW NO Filter: Connect H=1 7/16"; Connect Length=4 1/4"; Connector for 6ROW LS=No; Connector for 6ROW RS=No; Description=DOAS SERIES FAN POWERED AIR TERMINAL; Diameter=11 7/8"; Discharge Height "Y"=16"; Discharge Width "X"=19"; Duct Inlet=6"; Filter LH=No; Filter RH=No; Height=20"; Induct Center C=10"; Induct Center D=24"; Induct Filter D=41 3/4"; Induction D=41"; Inlet Left=No; Inlet Right=Yes; Length=48"; Model=ESTS/DOAS; Radius=5 15/16"; Row F=4"; Second Pipe H=1/8"; URL=https://www.anemostat-hvac.com; Width=48"
- ESTS/DOAS 3/4-hp - 12R W/4ROW NO Filter: Connect H=1 7/16"; Connect Length=4 1/4"; Connector for 6ROW LS=No; Connector for 6ROW RS=No; Description=DOAS SERIES FAN POWERED AIR TERMINAL; Diameter=11 7/8"; Discharge Height "Y"=16"; Discharge Width "X"=19"; Duct Inlet=6"; Filter LH=No; Filter RH=No; Height=20"; Induct Center C=10"; Induct Center D=24"; Induct Filter D=41 3/4"; Induction D=41"; Inlet Left=No; Inlet Right=Yes; Length=48"; Model=ESTS/DOAS; Radius=5 15/16"; Row F=6"; Second Pipe H=2 1/8"; URL=https://www.anemostat-hvac.com; Width=48"
- ESTS/DOAS 3/4-hp - 12R W/6ROW NO Filter: Connect H=1 7/16"; Connect Length=4 1/4"; Connector for 6ROW LS=Yes; Connector for 6ROW RS=No; Description=DOAS SERIES FAN POWERED AIR TERMINAL; Diameter=11 7/8"; Discharge Height "Y"=16"; Discharge Width "X"=19"; Duct Inlet=6"; Filter LH=No; Filter RH=No; Height=20"; Induct Center C=10"; Induct Center D=24"; Induct Filter D=41 3/4"; Induction D=41"; Inlet Left=No; Inlet Right=Yes; Length=48"; Model=ESTS/DOAS; Radius=5 15/16"; Row F=8"; Second Pipe H=4 1/8"; URL=https://www.anemostat-hvac.com; Width=48"
- ESTS/DOAS 3/4-hp - 10R W/2ROW & Filter: Connect H=1 7/16"; Connect Length=4 1/4"; Connector for 6ROW LS=No; Connector for 6ROW RS=No; Description=DOAS SERIES FAN POWERED AIR TERMINAL; Diameter=9 7/8"; Discharge Height "Y"=16"; Discharge Width "X"=19"; Duct Inlet=5"; Filter LH=Yes; Filter RH=No; Height=20"; Induct Center C=10"; Induct Center D=24"; Induct Filter D=41 3/4"; Induction D=41"; Inlet Left=No; Inlet Right=Yes; Length=48"; Model=ESTS/DOAS; Radius=4 15/16"; Row F=4"; Second Pipe H=1/8"; URL=https://www.anemostat-hvac.com; Width=48"
- ESTS/DOAS 3/4-hp - 10R W/4ROW & Filter: Connect H=1 7/16"; Connect Length=4 1/4"; Connector for 6ROW LS=No; Connector for 6ROW RS=No; Description=DOAS SERIES FAN POWERED AIR TERMINAL; Diameter=9 7/8"; Discharge Height "Y"=16"; Discharge Width "X"=19"; Duct Inlet=5"; Filter LH=Yes; Filter RH=No; Height=20"; Induct Center C=10"; Induct Center D=24"; Induct Filter D=41 3/4"; Induction D=41"; Inlet Left=No; Inlet Right=Yes; Length=48"; Model=ESTS/DOAS; Radius=4 15/16"; Row F=6"; Second Pipe H=2 1/8"; URL=https://www.anemostat-hvac.com; Width=48"
- ESTS/DOAS 3/4-hp - 10R W/6ROW & Filter: Connect H=1 7/16"; Connect Length=4 1/4"; Connector for 6ROW LS=Yes; Connector for 6ROW RS=No; Description=DOAS SERIES FAN POWERED AIR TERMINAL; Diameter=9 7/8"; Discharge Height "Y"=16"; Discharge Width "X"=19"; Duct Inlet=5"; Filter LH=Yes; Filter RH=No; Height=20"; Induct Center C=10"; Induct Center D=24"; Induct Filter D=41 3/4"; Induction D=41"; Inlet Left=No; Inlet Right=Yes; Length=48"; Model=ESTS/DOAS; Radius=4 15/16"; Row F=8"; Second Pipe H=4 1/8"; URL=https://www.anemostat-hvac.com; Width=48"
- ESTS/DOAS 3/4-hp - 10R W/2ROW NO Filter: Connect H=1 7/16"; Connect Length=4 1/4"; Connector for 6ROW LS=No; Connector for 6ROW RS=No; Description=DOAS SERIES FAN POWERED AIR TERMINAL; Diameter=9 7/8"; Discharge Height "Y"=16"; Discharge Width "X"=19"; Duct Inlet=5"; Filter LH=No; Filter RH=No; Height=20"; Induct Center C=10"; Induct Center D=24"; Induct Filter D=41 3/4"; Induction D=41"; Inlet Left=No; Inlet Right=Yes; Length=48"; Model=ESTS/DOAS; Radius=4 15/16"; Row F=4"; Second Pipe H=1/8"; URL=https://www.anemostat-hvac.com; Width=48"
- ESTS/DOAS 3/4-hp - 10R W/4ROW NO Filter: Connect H=1 7/16"; Connect Length=4 1/4"; Connector for 6ROW LS=No; Connector for 6ROW RS=No; Description=DOAS SERIES FAN POWERED AIR TERMINAL; Diameter=9 7/8"; Discharge Height "Y"=16"; Discharge Width "X"=19"; Duct Inlet=5"; Filter LH=No; Filter RH=No; Height=20"; Induct Center C=10"; Induct Center D=24"; Induct Filter D=41 3/4"; Induction D=41"; Inlet Left=No; Inlet Right=Yes; Length=48"; Model=ESTS/DOAS; Radius=4 15/16"; Row F=6"; Second Pipe H=2 1/8"; URL=https://www.anemostat-hvac.com; Width=48"
- ESTS/DOAS 3/4-hp - 10R W/6ROW NO Filter: Connect H=1 7/16"; Connect Length=4 1/4"; Connector for 6ROW LS=Yes; Connector for 6ROW RS=No; Description=DOAS SERIES FAN POWERED AIR TERMINAL; Diameter=9 7/8"; Discharge Height "Y"=16"; Discharge Width "X"=19"; Duct Inlet=5"; Filter LH=No; Filter RH=No; Height=20"; Induct Center C=10"; Induct Center D=24"; Induct Filter D=41 3/4"; Induction D=41"; Inlet Left=No; Inlet Right=Yes; Length=48"; Model=ESTS/DOAS; Radius=4 15/16"; Row F=8"; Second Pipe H=4 1/8"; URL=https://www.anemostat-hvac.com; Width=48"
- ESTS/DOAS 3/4-hp - 09R W/2ROW & Filter: Connect H=1 7/16"; Connect Length=4 1/4"; Connector for 6ROW LS=No; Connector for 6ROW RS=No; Description=DOAS SERIES FAN POWERED AIR TERMINAL; Diameter=8 7/8"; Discharge Height "Y"=16"; Discharge Width "X"=19"; Duct Inlet=4"; Filter LH=Yes; Filter RH=No; Height=20"; Induct Center C=10"; Induct Center D=24"; Induct Filter D=41 3/4"; Induction D=41"; Inlet Left=No; Inlet Right=Yes; Length=48"; Model=ESTS/DOAS; Radius=4 7/16"; Row F=4"; Second Pipe H=1/8"; URL=https://www.anemostat-hvac.com; Width=48"
- ESTS/DOAS 3/4-hp - 09R W/4ROW & Filter: Connect H=1 7/16"; Connect Length=4 1/4"; Connector for 6ROW LS=No; Connector for 6ROW RS=No; Description=DOAS SERIES FAN POWERED AIR TERMINAL; Diameter=8 7/8"; Discharge Height "Y"=16"; Discharge Width "X"=19"; Duct Inlet=4"; Filter LH=Yes; Filter RH=No; Height=20"; Induct Center C=10"; Induct Center D=24"; Induct Filter D=41 3/4"; Induction D=41"; Inlet Left=No; Inlet Right=Yes; Length=48"; Model=ESTS/DOAS; Radius=4 7/16"; Row F=6"; Second Pipe H=2 1/8"; URL=https://www.anemostat-hvac.com; Width=48"
- ESTS/DOAS 3/4-hp - 09R W/6ROW & Filter: Connect H=1 7/16"; Connect Length=4 1/4"; Connector for 6ROW LS=Yes; Connector for 6ROW RS=No; Description=DOAS SERIES FAN POWERED AIR TERMINAL; Diameter=8 7/8"; Discharge Height "Y"=16"; Discharge Width "X"=19"; Duct Inlet=4"; Filter LH=Yes; Filter RH=No; Height=20"; Induct Center C=10"; Induct Center D=24"; Induct Filter D=41 3/4"; Induction D=41"; Inlet Left=No; Inlet Right=Yes; Length=48"; Model=ESTS/DOAS; Radius=4 7/16"; Row F=8"; Second Pipe H=4 1/8"; URL=https://www.anemostat-hvac.com; Width=48"
- ESTS/DOAS 3/4-hp - 09R W/2ROW NO Filter: Connect H=1 7/16"; Connect Length=4 1/4"; Connector for 6ROW LS=No; Connector for 6ROW RS=No; Description=DOAS SERIES FAN POWERED AIR TERMINAL; Diameter=8 7/8"; Discharge Height "Y"=16"; Discharge Width "X"=19"; Duct Inlet=4"; Filter LH=No; Filter RH=No; Height=20"; Induct Center C=10"; Induct Center D=24"; Induct Filter D=41 3/4"; Induction D=41"; Inlet Left=No; Inlet Right=Yes; Length=48"; Model=ESTS/DOAS; Radius=4 7/16"; Row F=4"; Second Pipe H=1/8"; URL=https://www.anemostat-hvac.com; Width=48"
- ESTS/DOAS 3/4-hp - 09R W/4ROW NO Filter: Connect H=1 7/16"; Connect Length=4 1/4"; Connector for 6ROW LS=No; Connector for 6ROW RS=No; Description=DOAS SERIES FAN POWERED AIR TERMINAL; Diameter=8 7/8"; Discharge Height "Y"=16"; Discharge Width "X"=19"; Duct Inlet=4"; Filter LH=No; Filter RH=No; Height=20"; Induct Center C=10"; Induct Center D=24"; Induct Filter D=41 3/4"; Induction D=41"; Inlet Left=No; Inlet Right=Yes; Length=48"; Model=ESTS/DOAS; Radius=4 7/16"; Row F=6"; Second Pipe H=2 1/8"; URL=https://www.anemostat-hvac.com; Width=48"
- ESTS/DOAS 3/4-hp - 09R W/6ROW NO Filter: Connect H=1 7/16"; Connect Length=4 1/4"; Connector for 6ROW LS=Yes; Connector for 6ROW RS=No; Description=DOAS SERIES FAN POWERED AIR TERMINAL; Diameter=8 7/8"; Discharge Height "Y"=16"; Discharge Width "X"=19"; Duct Inlet=4"; Filter LH=No; Filter RH=No; Height=20"; Induct Center C=10"; Induct Center D=24"; Induct Filter D=41 3/4"; Induction D=41"; Inlet Left=No; Inlet Right=Yes; Length=48"; Model=ESTS/DOAS; Radius=4 7/16"; Row F=8"; Second Pipe H=4 1/8"; URL=https://www.anemostat-hvac.com; Width=48"
- ESTS/DOAS 3/4-hp - 08R W/2ROW & Filter: Connect H=1 7/16"; Connect Length=4 1/4"; Connector for 6ROW LS=No; Connector for 6ROW RS=No; Description=DOAS SERIES FAN POWERED AIR TERMINAL; Diameter=7 7/8"; Discharge Height "Y"=16"; Discharge Width "X"=19"; Duct Inlet=4"; Filter LH=Yes; Filter RH=No; Height=20"; Induct Center C=10"; Induct Center D=24"; Induct Filter D=41 3/4"; Induction D=41"; Inlet Left=No; Inlet Right=Yes; Length=48"; Model=ESTS/DOAS; Radius=3 15/16"; Row F=4"; Second Pipe H=1/8"; URL=https://www.anemostat-hvac.com; Width=48"
- ESTS/DOAS 3/4-hp - 08R W/4ROW & Filter: Connect H=1 7/16"; Connect Length=4 1/4"; Connector for 6ROW LS=No; Connector for 6ROW RS=No; Description=DOAS SERIES FAN POWERED AIR TERMINAL; Diameter=7 7/8"; Discharge Height "Y"=16"; Discharge Width "X"=19"; Duct Inlet=4"; Filter LH=Yes; Filter RH=No; Height=20"; Induct Center C=10"; Induct Center D=24"; Induct Filter D=41 3/4"; Induction D=41"; Inlet Left=No; Inlet Right=Yes; Length=48"; Model=ESTS/DOAS; Radius=3 15/16"; Row F=6"; Second Pipe H=2 1/8"; URL=https://www.anemostat-hvac.com; Width=48"
- ESTS/DOAS 3/4-hp - 08R W/6ROW & Filter: Connect H=1 7/16"; Connect Length=4 1/4"; Connector for 6ROW LS=Yes; Connector for 6ROW RS=No; Description=DOAS SERIES FAN POWERED AIR TERMINAL; Diameter=7 7/8"; Discharge Height "Y"=16"; Discharge Width "X"=19"; Duct Inlet=4"; Filter LH=Yes; Filter RH=No; Height=20"; Induct Center C=10"; Induct Center D=24"; Induct Filter D=41 3/4"; Induction D=41"; Inlet Left=No; Inlet Right=Yes; Length=48"; Model=ESTS/DOAS; Radius=3 15/16"; Row F=8"; Second Pipe H=4 1/8"; URL=https://www.anemostat-hvac.com; Width=48"
- ESTS/DOAS 3/4-hp - 08R W/2ROW NO Filter: Connect H=1 7/16"; Connect Length=4 1/4"; Connector for 6ROW LS=No; Connector for 6ROW RS=No; Description=DOAS SERIES FAN POWERED AIR TERMINAL; Diameter=7 7/8"; Discharge Height "Y"=16"; Discharge Width "X"=19"; Duct Inlet=4"; Filter LH=No; Filter RH=No; Height=20"; Induct Center C=10"; Induct Center D=24"; Induct Filter D=41 3/4"; Induction D=41"; Inlet Left=No; Inlet Right=Yes; Length=48"; Model=ESTS/DOAS; Radius=3 15/16"; Row F=4"; Second Pipe H=1/8"; URL=https://www.anemostat-hvac.com; Width=48"
- ESTS/DOAS 3/4-hp - 08R W/4ROW NO Filter: Connect H=1 7/16"; Connect Length=4 1/4"; Connector for 6ROW LS=No; Connector for 6ROW RS=No; Description=DOAS SERIES FAN POWERED AIR TERMINAL; Diameter=7 7/8"; Discharge Height "Y"=16"; Discharge Width "X"=19"; Duct Inlet=4"; Filter LH=No; Filter RH=No; Height=20"; Induct Center C=10"; Induct Center D=24"; Induct Filter D=41 3/4"; Induction D=41"; Inlet Left=No; Inlet Right=Yes; Length=48"; Model=ESTS/DOAS; Radius=3 15/16"; Row F=6"; Second Pipe H=2 1/8"; URL=https://www.anemostat-hvac.com; Width=48"
- ESTS/DOAS 3/4-hp - 08R W/6ROW NO Filter: Connect H=1 7/16"; Connect Length=4 1/4"; Connector for 6ROW LS=Yes; Connector for 6ROW RS=No; Description=DOAS SERIES FAN POWERED AIR TERMINAL; Diameter=7 7/8"; Discharge Height "Y"=16"; Discharge Width "X"=19"; Duct Inlet=4"; Filter LH=No; Filter RH=No; Height=20"; Induct Center C=10"; Induct Center D=24"; Induct Filter D=41 3/4"; Induction D=41"; Inlet Left=No; Inlet Right=Yes; Length=48"; Model=ESTS/DOAS; Radius=3 15/16"; Row F=8"; Second Pipe H=4 1/8"; URL=https://www.anemostat-hvac.com; Width=48"
- ESTS/DOAS 3/4-hp - 10L W/4ROW & Filter: Connect H=1 7/16"; Connect Length=4 1/4"; Connector for 6ROW LS=No; Connector for 6ROW RS=No; Description=DOAS SERIES FAN POWERED AIR TERMINAL; Diameter=9 7/8"; Discharge Height "Y"=16"; Discharge Width "X"=19"; Duct Inlet=5"; Filter LH=No; Filter RH=Yes; Height=20"; Induct Center C=10"; Induct Center D=24"; Induct Filter D=41 3/4"; Induction D=41"; Inlet Left=Yes; Inlet Right=No; Length=48"; Model=ESTS/DOAS; Radius=4 15/16"; Row F=6"; Second Pipe H=2 1/8"; URL=https://www.anemostat-hvac.com; Width=48"
- ESTS/DOAS 3/4-hp - 10L W/6ROW & Filter: Connect H=1 7/16"; Connect Length=4 1/4"; Connector for 6ROW LS=No; Connector for 6ROW RS=Yes; Description=DOAS SERIES FAN POWERED AIR TERMINAL; Diameter=9 7/8"; Discharge Height "Y"=16"; Discharge Width "X"=19"; Duct Inlet=5"; Filter LH=No; Filter RH=Yes; Height=20"; Induct Center C=10"; Induct Center D=24"; Induct Filter D=41 3/4"; Induction D=41"; Inlet Left=Yes; Inlet Right=No; Length=48"; Model=ESTS/DOAS; Radius=4 15/16"; Row F=8"; Second Pipe H=4 1/8"; URL=https://www.anemostat-hvac.com; Width=48"
- ESTS/DOAS 3/4-hp - 10L W/4ROW NO Filter: Connect H=1 7/16"; Connect Length=4 1/4"; Connector for 6ROW LS=No; Connector for 6ROW RS=No; Description=DOAS SERIES FAN POWERED AIR TERMINAL; Diameter=9 7/8"; Discharge Height "Y"=16"; Discharge Width "X"=19"; Duct Inlet=5"; Filter LH=No; Filter RH=No; Height=20"; Induct Center C=10"; Induct Center D=24"; Induct Filter D=41 3/4"; Induction D=41"; Inlet Left=Yes; Inlet Right=No; Length=48"; Model=ESTS/DOAS; Radius=4 15/16"; Row F=6"; Second Pipe H=2 1/8"; URL=https://www.anemostat-hvac.com; Width=48"
- ESTS/DOAS 3/4-hp - 10L W/6ROW NO Filter: Connect H=1 7/16"; Connect Length=4 1/4"; Connector for 6ROW LS=No; Connector for 6ROW RS=Yes; Description=DOAS SERIES FAN POWERED AIR TERMINAL; Diameter=9 7/8"; Discharge Height "Y"=16"; Discharge Width "X"=19"; Duct Inlet=5"; Filter LH=No; Filter RH=No; Height=20"; Induct Center C=10"; Induct Center D=24"; Induct Filter D=41 3/4"; Induction D=41"; Inlet Left=Yes; Inlet Right=No; Length=48"; Model=ESTS/DOAS; Radius=4 15/16"; Row F=8"; Second Pipe H=4 1/8"; URL=https://www.anemostat-hvac.com; Width=48"
- ESTS/DOAS 3/4-hp - 09L W/4ROW & Filter: Connect H=1 7/16"; Connect Length=4 1/4"; Connector for 6ROW LS=No; Connector for 6ROW RS=No; Description=DOAS SERIES FAN POWERED AIR TERMINAL; Diameter=8 7/8"; Discharge Height "Y"=16"; Discharge Width "X"=19"; Duct Inlet=4"; Filter LH=No; Filter RH=Yes; Height=20"; Induct Center C=10"; Induct Center D=24"; Induct Filter D=41 3/4"; Induction D=41"; Inlet Left=Yes; Inlet Right=No; Length=48"; Model=ESTS/DOAS; Radius=4 7/16"; Row F=6"; Second Pipe H=2 1/8"; URL=https://www.anemostat-hvac.com; Width=48"
- ESTS/DOAS 3/4-hp - 09L W/6ROW & Filter: Connect H=1 7/16"; Connect Length=4 1/4"; Connector for 6ROW LS=No; Connector for 6ROW RS=Yes; Description=DOAS SERIES FAN POWERED AIR TERMINAL; Diameter=8 7/8"; Discharge Height "Y"=16"; Discharge Width "X"=19"; Duct Inlet=4"; Filter LH=No; Filter RH=Yes; Height=20"; Induct Center C=10"; Induct Center D=24"; Induct Filter D=41 3/4"; Induction D=41"; Inlet Left=Yes; Inlet Right=No; Length=48"; Model=ESTS/DOAS; Radius=4 7/16"; Row F=8"; Second Pipe H=4 1/8"; URL=https://www.anemostat-hvac.com; Width=48"
- ESTS/DOAS 3/4-hp - 09L W/4ROW NO Filter: Connect H=1 7/16"; Connect Length=4 1/4"; Connector for 6ROW LS=No; Connector for 6ROW RS=No; Description=DOAS SERIES FAN POWERED AIR TERMINAL; Diameter=8 7/8"; Discharge Height "Y"=16"; Discharge Width "X"=19"; Duct Inlet=4"; Filter LH=No; Filter RH=No; Height=20"; Induct Center C=10"; Induct Center D=24"; Induct Filter D=41 3/4"; Induction D=41"; Inlet Left=Yes; Inlet Right=No; Length=48"; Model=ESTS/DOAS; Radius=4 7/16"; Row F=6"; Second Pipe H=2 1/8"; URL=https://www.anemostat-hvac.com; Width=48"
- ESTS/DOAS 3/4-hp - 09L W/6ROW NO Filter: Connect H=1 7/16"; Connect Length=4 1/4"; Connector for 6ROW LS=No; Connector for 6ROW RS=Yes; Description=DOAS SERIES FAN POWERED AIR TERMINAL; Diameter=8 7/8"; Discharge Height "Y"=16"; Discharge Width "X"=19"; Duct Inlet=4"; Filter LH=No; Filter RH=No; Height=20"; Induct Center C=10"; Induct Center D=24"; Induct Filter D=41 3/4"; Induction D=41"; Inlet Left=Yes; Inlet Right=No; Length=48"; Model=ESTS/DOAS; Radius=4 7/16"; Row F=8"; Second Pipe H=4 1/8"; URL=https://www.anemostat-hvac.com; Width=48"
- ESTS/DOAS 3/4-hp - 08L W/4ROW & Filter: Connect H=1 7/16"; Connect Length=4 1/4"; Connector for 6ROW LS=No; Connector for 6ROW RS=No; Description=DOAS SERIES FAN POWERED AIR TERMINAL; Diameter=7 7/8"; Discharge Height "Y"=16"; Discharge Width "X"=19"; Duct Inlet=4"; Filter LH=No; Filter RH=Yes; Height=20"; Induct Center C=10"; Induct Center D=24"; Induct Filter D=41 3/4"; Induction D=41"; Inlet Left=Yes; Inlet Right=No; Length=48"; Model=ESTS/DOAS; Radius=3 15/16"; Row F=6"; Second Pipe H=2 1/8"; URL=https://www.anemostat-hvac.com; Width=48"
- ESTS/DOAS 3/4-hp - 08L W/6ROW & Filter: Connect H=1 7/16"; Connect Length=4 1/4"; Connector for 6ROW LS=No; Connector for 6ROW RS=Yes; Description=DOAS SERIES FAN POWERED AIR TERMINAL; Diameter=7 7/8"; Discharge Height "Y"=16"; Discharge Width "X"=19"; Duct Inlet=4"; Filter LH=No; Filter RH=Yes; Height=20"; Induct Center C=10"; Induct Center D=24"; Induct Filter D=41 3/4"; Induction D=41"; Inlet Left=Yes; Inlet Right=No; Length=48"; Model=ESTS/DOAS; Radius=3 15/16"; Row F=8"; Second Pipe H=4 1/8"; URL=https://www.anemostat-hvac.com; Width=48"
- ESTS/DOAS 3/4-hp - 08L W/4ROW NO Filter: Connect H=1 7/16"; Connect Length=4 1/4"; Connector for 6ROW LS=No; Connector for 6ROW RS=No; Description=DOAS SERIES FAN POWERED AIR TERMINAL; Diameter=7 7/8"; Discharge Height "Y"=16"; Discharge Width "X"=19"; Duct Inlet=4"; Filter LH=No; Filter RH=No; Height=20"; Induct Center C=10"; Induct Center D=24"; Induct Filter D=41 3/4"; Induction D=41"; Inlet Left=Yes; Inlet Right=No; Length=48"; Model=ESTS/DOAS; Radius=3 15/16"; Row F=6"; Second Pipe H=2 1/8"; URL=https://www.anemostat-hvac.com; Width=48"
- ESTS/DOAS 3/4-hp - 08L W/6ROW NO Filter: Connect H=1 7/16"; Connect Length=4 1/4"; Connector for 6ROW LS=No; Connector for 6ROW RS=Yes; Description=DOAS SERIES FAN POWERED AIR TERMINAL; Diameter=7 7/8"; Discharge Height "Y"=16"; Discharge Width "X"=19"; Duct Inlet=4"; Filter LH=No; Filter RH=No; Height=20"; Induct Center C=10"; Induct Center D=24"; Induct Filter D=41 3/4"; Induction D=41"; Inlet Left=Yes; Inlet Right=No; Length=48"; Model=ESTS/DOAS; Radius=3 15/16"; Row F=8"; Second Pipe H=4 1/8"; URL=https://www.anemostat-hvac.com; Width=48"
- ESTS/DOAS 3/4-hp - 07L W/4ROW NO Filter: Connect H=1 7/16"; Connect Length=4 1/4"; Connector for 6ROW LS=No; Connector for 6ROW RS=No; Description=DOAS SERIES FAN POWERED AIR TERMINAL; Diameter=6 7/8"; Discharge Height "Y"=16"; Discharge Width "X"=19"; Duct Inlet=3"; Filter LH=No; Filter RH=No; Height=20"; Induct Center C=10"; Induct Center D=24"; Induct Filter D=41 3/4"; Induction D=41"; Inlet Left=Yes; Inlet Right=No; Length=48"; Model=ESTS/DOAS; Radius=3 7/16"; Row F=6"; Second Pipe H=2 1/8"; URL=https://www.anemostat-hvac.com; Width=48"
- ESTS/DOAS 3/4-hp - 07L W/6ROW NO Filter: Connect H=1 7/16"; Connect Length=4 1/4"; Connector for 6ROW LS=No; Connector for 6ROW RS=Yes; Description=DOAS SERIES FAN POWERED AIR TERMINAL; Diameter=6 7/8"; Discharge Height "Y"=16"; Discharge Width "X"=19"; Duct Inlet=3"; Filter LH=No; Filter RH=No; Height=20"; Induct Center C=10"; Induct Center D=24"; Induct Filter D=41 3/4"; Induction D=41"; Inlet Left=Yes; Inlet Right=No; Length=48"; Model=ESTS/DOAS; Radius=3 7/16"; Row F=8"; Second Pipe H=4 1/8"; URL=https://www.anemostat-hvac.com; Width=48"
- ESTS/DOAS 3/4-hp - 07L W/4ROW & Filter: Connect H=1 7/16"; Connect Length=4 1/4"; Connector for 6ROW LS=No; Connector for 6ROW RS=No; Description=DOAS SERIES FAN POWERED AIR TERMINAL; Diameter=6 7/8"; Discharge Height "Y"=16"; Discharge Width "X"=19"; Duct Inlet=3"; Filter LH=No; Filter RH=Yes; Height=20"; Induct Center C=10"; Induct Center D=24"; Induct Filter D=41 3/4"; Induction D=41"; Inlet Left=Yes; Inlet Right=No; Length=48"; Model=ESTS/DOAS; Radius=3 7/16"; Row F=6"; Second Pipe H=2 1/8"; URL=https://www.anemostat-hvac.com; Width=48"
- ESTS/DOAS 3/4-hp - 07L W/6ROW & Filter: Connect H=1 7/16"; Connect Length=4 1/4"; Connector for 6ROW LS=No; Connector for 6ROW RS=Yes; Description=DOAS SERIES FAN POWERED AIR TERMINAL; Diameter=6 7/8"; Discharge Height "Y"=16"; Discharge Width "X"=19"; Duct Inlet=3"; Filter LH=No; Filter RH=Yes; Height=20"; Induct Center C=10"; Induct Center D=24"; Induct Filter D=41 3/4"; Induction D=41"; Inlet Left=Yes; Inlet Right=No; Length=48"; Model=ESTS/DOAS; Radius=3 7/16"; Row F=8"; Second Pipe H=4 1/8"; URL=https://www.anemostat-hvac.com; Width=48"
- ESTS/DOAS 3/4-hp - 06L W/4ROW NO Filter: Connect H=1 7/16"; Connect Length=4 1/4"; Connector for 6ROW LS=No; Connector for 6ROW RS=No; Description=DOAS SERIES FAN POWERED AIR TERMINAL; Diameter=5 7/8"; Discharge Height "Y"=16"; Discharge Width "X"=19"; Duct Inlet=3"; Filter LH=No; Filter RH=No; Height=20"; Induct Center C=10"; Induct Center D=24"; Induct Filter D=41 3/4"; Induction D=41"; Inlet Left=Yes; Inlet Right=No; Length=48"; Model=ESTS/DOAS; Radius=2 15/16"; Row F=6"; Second Pipe H=2 1/8"; URL=https://www.anemostat-hvac.com; Width=48"
- ESTS/DOAS 3/4-hp - 06L W/6ROW NO Filter: Connect H=1 7/16"; Connect Length=4 1/4"; Connector for 6ROW LS=No; Connector for 6ROW RS=Yes; Description=DOAS SERIES FAN POWERED AIR TERMINAL; Diameter=5 7/8"; Discharge Height "Y"=16"; Discharge Width "X"=19"; Duct Inlet=3"; Filter LH=No; Filter RH=No; Height=20"; Induct Center C=10"; Induct Center D=24"; Induct Filter D=41 3/4"; Induction D=41"; Inlet Left=Yes; Inlet Right=No; Length=48"; Model=ESTS/DOAS; Radius=2 15/16"; Row F=8"; Second Pipe H=4 1/8"; URL=https://www.anemostat-hvac.com; Width=48"
- ESTS/DOAS 3/4-hp - 06L W/4ROW & Filter: Connect H=1 7/16"; Connect Length=4 1/4"; Connector for 6ROW LS=No; Connector for 6ROW RS=No; Description=DOAS SERIES FAN POWERED AIR TERMINAL; Diameter=5 7/8"; Discharge Height "Y"=16"; Discharge Width "X"=19"; Duct Inlet=3"; Filter LH=No; Filter RH=Yes; Height=20"; Induct Center C=10"; Induct Center D=24"; Induct Filter D=41 3/4"; Induction D=41"; Inlet Left=Yes; Inlet Right=No; Length=48"; Model=ESTS/DOAS; Radius=2 15/16"; Row F=6"; Second Pipe H=2 1/8"; URL=https://www.anemostat-hvac.com; Width=48"
- ESTS/DOAS 3/4-hp - 06L W/6ROW & Filter: Connect H=1 7/16"; Connect Length=4 1/4"; Connector for 6ROW LS=No; Connector for 6ROW RS=Yes; Description=DOAS SERIES FAN POWERED AIR TERMINAL; Diameter=5 7/8"; Discharge Height "Y"=16"; Discharge Width "X"=19"; Duct Inlet=3"; Filter LH=No; Filter RH=Yes; Height=20"; Induct Center C=10"; Induct Center D=24"; Induct Filter D=41 3/4"; Induction D=41"; Inlet Left=Yes; Inlet Right=No; Length=48"; Model=ESTS/DOAS; Radius=2 15/16"; Row F=8"; Second Pipe H=4 1/8"; URL=https://www.anemostat-hvac.com; Width=48"
- ESTS/DOAS 3/4-hp - 07R W/2ROW NO Filter: Connect H=1 7/16"; Connect Length=4 1/4"; Connector for 6ROW LS=No; Connector for 6ROW RS=No; Description=DOAS SERIES FAN POWERED AIR TERMINAL; Diameter=6 7/8"; Discharge Height "Y"=16"; Discharge Width "X"=19"; Duct Inlet=3"; Filter LH=No; Filter RH=No; Height=20"; Induct Center C=10"; Induct Center D=24"; Induct Filter D=41 3/4"; Induction D=41"; Inlet Left=No; Inlet Right=Yes; Length=48"; Model=ESTS/DOAS; Radius=3 7/16"; Row F=4"; Second Pipe H=1/8"; URL=https://www.anemostat-hvac.com; Width=48"
- ESTS/DOAS 3/4-hp - 07R W/4ROW NO Filter: Connect H=1 7/16"; Connect Length=4 1/4"; Connector for 6ROW LS=No; Connector for 6ROW RS=No; Description=DOAS SERIES FAN POWERED AIR TERMINAL; Diameter=6 7/8"; Discharge Height "Y"=16"; Discharge Width "X"=19"; Duct Inlet=3"; Filter LH=No; Filter RH=No; Height=20"; Induct Center C=10"; Induct Center D=24"; Induct Filter D=41 3/4"; Induction D=41"; Inlet Left=No; Inlet Right=Yes; Length=48"; Model=ESTS/DOAS; Radius=3 7/16"; Row F=6"; Second Pipe H=2 1/8"; URL=https://www.anemostat-hvac.com; Width=48"
- ESTS/DOAS 3/4-hp - 07R W/6ROW NO Filter: Connect H=1 7/16"; Connect Length=4 1/4"; Connector for 6ROW LS=Yes; Connector for 6ROW RS=No; Description=DOAS SERIES FAN POWERED AIR TERMINAL; Diameter=6 7/8"; Discharge Height "Y"=16"; Discharge Width "X"=19"; Duct Inlet=3"; Filter LH=No; Filter RH=No; Height=20"; Induct Center C=10"; Induct Center D=24"; Induct Filter D=41 3/4"; Induction D=41"; Inlet Left=No; Inlet Right=Yes; Length=48"; Model=ESTS/DOAS; Radius=3 7/16"; Row F=8"; Second Pipe H=4 1/8"; URL=https://www.anemostat-hvac.com; Width=48"
- ESTS/DOAS 3/4-hp - 07R W/2ROW & Filter: Connect H=1 7/16"; Connect Length=4 1/4"; Connector for 6ROW LS=No; Connector for 6ROW RS=No; Description=DOAS SERIES FAN POWERED AIR TERMINAL; Diameter=6 7/8"; Discharge Height "Y"=16"; Discharge Width "X"=19"; Duct Inlet=3"; Filter LH=Yes; Filter RH=No; Height=20"; Induct Center C=10"; Induct Center D=24"; Induct Filter D=41 3/4"; Induction D=41"; Inlet Left=No; Inlet Right=Yes; Length=48"; Model=ESTS/DOAS; Radius=3 7/16"; Row F=4"; Second Pipe H=1/8"; URL=https://www.anemostat-hvac.com; Width=48"
- ESTS/DOAS 3/4-hp - 07R W/4ROW & Filter: Connect H=1 7/16"; Connect Length=4 1/4"; Connector for 6ROW LS=No; Connector for 6ROW RS=No; Description=DOAS SERIES FAN POWERED AIR TERMINAL; Diameter=6 7/8"; Discharge Height "Y"=16"; Discharge Width "X"=19"; Duct Inlet=3"; Filter LH=Yes; Filter RH=No; Height=20"; Induct Center C=10"; Induct Center D=24"; Induct Filter D=41 3/4"; Induction D=41"; Inlet Left=No; Inlet Right=Yes; Length=48"; Model=ESTS/DOAS; Radius=3 7/16"; Row F=6"; Second Pipe H=2 1/8"; URL=https://www.anemostat-hvac.com; Width=48"
- ESTS/DOAS 3/4-hp - 07R W/6ROW & Filter: Connect H=1 7/16"; Connect Length=4 1/4"; Connector for 6ROW LS=No; Connector for 6ROW RS=No; Description=DOAS SERIES FAN POWERED AIR TERMINAL; Diameter=6 7/8"; Discharge Height "Y"=16"; Discharge Width "X"=19"; Duct Inlet=3"; Filter LH=Yes; Filter RH=No; Height=20"; Induct Center C=10"; Induct Center D=24"; Induct Filter D=41 3/4"; Induction D=41"; Inlet Left=No; Inlet Right=Yes; Length=48"; Model=ESTS/DOAS; Radius=3 7/16"; Row F=8"; Second Pipe H=4 1/8"; URL=https://www.anemostat-hvac.com; Width=48"
- ESTS/DOAS 3/4-hp - 06R W/6ROW NO Filter: Connect H=1 7/16"; Connect Length=4 1/4"; Connector for 6ROW LS=Yes; Connector for 6ROW RS=No; Description=DOAS SERIES FAN POWERED AIR TERMINAL; Diameter=5 7/8"; Discharge Height "Y"=16"; Discharge Width "X"=19"; Duct Inlet=3"; Filter LH=No; Filter RH=No; Height=20"; Induct Center C=10"; Induct Center D=24"; Induct Filter D=41 3/4"; Induction D=41"; Inlet Left=No; Inlet Right=Yes; Length=48"; Model=ESTS/DOAS; Radius=2 15/16"; Row F=8"; Second Pipe H=4 1/8"; URL=https://www.anemostat-hvac.com; Width=48"
- ESTS/DOAS 3/4-hp - 06R W/4ROW NO Filter: Connect H=1 7/16"; Connect Length=4 1/4"; Connector for 6ROW LS=No; Connector for 6ROW RS=No; Description=DOAS SERIES FAN POWERED AIR TERMINAL; Diameter=5 7/8"; Discharge Height "Y"=16"; Discharge Width "X"=19"; Duct Inlet=3"; Filter LH=No; Filter RH=No; Height=20"; Induct Center C=10"; Induct Center D=24"; Induct Filter D=41 3/4"; Induction D=41"; Inlet Left=No; Inlet Right=Yes; Length=48"; Model=ESTS/DOAS; Radius=2 15/16"; Row F=6"; Second Pipe H=2 1/8"; URL=https://www.anemostat-hvac.com; Width=48"
- ESTS/DOAS 3/4-hp - 06R W/2ROW NO Filter: Connect H=1 7/16"; Connect Length=4 1/4"; Connector for 6ROW LS=No; Connector for 6ROW RS=No; Description=DOAS SERIES FAN POWERED AIR TERMINAL; Diameter=5 7/8"; Discharge Height "Y"=16"; Discharge Width "X"=19"; Duct Inlet=3"; Filter LH=No; Filter RH=No; Height=20"; Induct Center C=10"; Induct Center D=24"; Induct Filter D=41 3/4"; Induction D=41"; Inlet Left=No; Inlet Right=Yes; Length=48"; Model=ESTS/DOAS; Radius=2 15/16"; Row F=4"; Second Pipe H=1/8"; URL=https://www.anemostat-hvac.com; Width=48"
- ESTS/DOAS 3/4-hp - 06R W/2ROW & Filter: Connect H=1 7/16"; Connect Length=4 1/4"; Connector for 6ROW LS=No; Connector for 6ROW RS=No; Description=DOAS SERIES FAN POWERED AIR TERMINAL; Diameter=5 7/8"; Discharge Height "Y"=16"; Discharge Width "X"=19"; Duct Inlet=3"; Filter LH=Yes; Filter RH=No; Height=20"; Induct Center C=10"; Induct Center D=24"; Induct Filter D=41 3/4"; Induction D=41"; Inlet Left=No; Inlet Right=Yes; Length=48"; Model=ESTS/DOAS; Radius=2 15/16"; Row F=4"; Second Pipe H=1/8"; URL=https://www.anemostat-hvac.com; Width=48"
- ESTS/DOAS 3/4-hp - 06R W/4ROW & Filter: Connect H=1 7/16"; Connect Length=4 1/4"; Connector for 6ROW LS=No; Connector for 6ROW RS=No; Description=DOAS SERIES FAN POWERED AIR TERMINAL; Diameter=5 7/8"; Discharge Height "Y"=16"; Discharge Width "X"=19"; Duct Inlet=3"; Filter LH=Yes; Filter RH=No; Height=20"; Induct Center C=10"; Induct Center D=24"; Induct Filter D=41 3/4"; Induction D=41"; Inlet Left=No; Inlet Right=Yes; Length=48"; Model=ESTS/DOAS; Radius=2 15/16"; Row F=6"; Second Pipe H=2 1/8"; URL=https://www.anemostat-hvac.com; Width=48"
- ESTS/DOAS 3/4-hp - 06R W/6ROW & Filter: Connect H=1 7/16"; Connect Length=4 1/4"; Connector for 6ROW LS=Yes; Connector for 6ROW RS=No; Description=DOAS SERIES FAN POWERED AIR TERMINAL; Diameter=5 7/8"; Discharge Height "Y"=16"; Discharge Width "X"=19"; Duct Inlet=3"; Filter LH=Yes; Filter RH=No; Height=20"; Induct Center C=10"; Induct Center D=24"; Induct Filter D=41 3/4"; Induction D=41"; Inlet Left=No; Inlet Right=Yes; Length=48"; Model=ESTS/DOAS; Radius=2 15/16"; Row F=8"; Second Pipe H=4 1/8"; URL=https://www.anemostat-hvac.com; Width=48"
- ESTS/DOAS 3/4-hp - 05L W/4ROW NO Filter: Connect H=1 7/16"; Connect Length=4 1/4"; Connector for 6ROW LS=No; Connector for 6ROW RS=No; Description=DOAS SERIES FAN POWERED AIR TERMINAL; Diameter=4 7/8"; Discharge Height "Y"=16"; Discharge Width "X"=19"; Duct Inlet=2"; Filter LH=No; Filter RH=No; Height=20"; Induct Center C=10"; Induct Center D=24"; Induct Filter D=41 3/4"; Induction D=41"; Inlet Left=Yes; Inlet Right=No; Length=48"; Model=ESTS/DOAS; Radius=2 7/16"; Row F=6"; Second Pipe H=2 1/8"; URL=https://www.anemostat-hvac.com; Width=48"
- ESTS/DOAS 3/4-hp - 05L W/6ROW NO Filter: Connect H=1 7/16"; Connect Length=4 1/4"; Connector for 6ROW LS=No; Connector for 6ROW RS=Yes; Description=DOAS SERIES FAN POWERED AIR TERMINAL; Diameter=4 7/8"; Discharge Height "Y"=16"; Discharge Width "X"=19"; Duct Inlet=2"; Filter LH=No; Filter RH=No; Height=20"; Induct Center C=10"; Induct Center D=24"; Induct Filter D=41 3/4"; Induction D=41"; Inlet Left=Yes; Inlet Right=No; Length=48"; Model=ESTS/DOAS; Radius=2 7/16"; Row F=8"; Second Pipe H=4 1/8"; URL=https://www.anemostat-hvac.com; Width=48"
- ESTS/DOAS 3/4-hp - 05R W/2ROW & Filter: Connect H=1 7/16"; Connect Length=4 1/4"; Connector for 6ROW LS=No; Connector for 6ROW RS=No; Description=DOAS SERIES FAN POWERED AIR TERMINAL; Diameter=4 7/8"; Discharge Height "Y"=16"; Discharge Width "X"=19"; Duct Inlet=2"; Filter LH=Yes; Filter RH=No; Height=20"; Induct Center C=10"; Induct Center D=24"; Induct Filter D=41 3/4"; Induction D=41"; Inlet Left=No; Inlet Right=Yes; Length=48"; Model=ESTS/DOAS; Radius=2 7/16"; Row F=4"; Second Pipe H=1/8"; URL=https://www.anemostat-hvac.com; Width=48"
- ESTS/DOAS 3/4-hp - 05R W/4ROW & Filter: Connect H=1 7/16"; Connect Length=4 1/4"; Connector for 6ROW LS=No; Connector for 6ROW RS=No; Description=DOAS SERIES FAN POWERED AIR TERMINAL; Diameter=4 7/8"; Discharge Height "Y"=16"; Discharge Width "X"=19"; Duct Inlet=2"; Filter LH=Yes; Filter RH=No; Height=20"; Induct Center C=10"; Induct Center D=24"; Induct Filter D=41 3/4"; Induction D=41"; Inlet Left=No; Inlet Right=Yes; Length=48"; Model=ESTS/DOAS; Radius=2 7/16"; Row F=6"; Second Pipe H=2 1/8"; URL=https://www.anemostat-hvac.com; Width=48"
- ESTS/DOAS 3/4-hp - 05R W/6ROW & Filter: Connect H=1 7/16"; Connect Length=4 1/4"; Connector for 6ROW LS=Yes; Connector for 6ROW RS=No; Description=DOAS SERIES FAN POWERED AIR TERMINAL; Diameter=4 7/8"; Discharge Height "Y"=16"; Discharge Width "X"=19"; Duct Inlet=2"; Filter LH=Yes; Filter RH=No; Height=20"; Induct Center C=10"; Induct Center D=24"; Induct Filter D=41 3/4"; Induction D=41"; Inlet Left=No; Inlet Right=Yes; Length=48"; Model=ESTS/DOAS; Radius=2 7/16"; Row F=8"; Second Pipe H=4 1/8"; URL=https://www.anemostat-hvac.com; Width=48"
- ESTS/DOAS 3/4-hp - 05R W/2ROW NO Filter: Connect H=1 7/16"; Connect Length=4 1/4"; Connector for 6ROW LS=No; Connector for 6ROW RS=No; Description=DOAS SERIES FAN POWERED AIR TERMINAL; Diameter=4 7/8"; Discharge Height "Y"=16"; Discharge Width "X"=19"; Duct Inlet=2"; Filter LH=No; Filter RH=No; Height=20"; Induct Center C=10"; Induct Center D=24"; Induct Filter D=41 3/4"; Induction D=41"; Inlet Left=No; Inlet Right=Yes; Length=48"; Model=ESTS/DOAS; Radius=2 7/16"; Row F=4"; Second Pipe H=1/8"; URL=https://www.anemostat-hvac.com; Width=48"
- ESTS/DOAS 3/4-hp - 05R W/4ROW NO Filter: Connect H=1 7/16"; Connect Length=4 1/4"; Connector for 6ROW LS=No; Connector for 6ROW RS=No; Description=DOAS SERIES FAN POWERED AIR TERMINAL; Diameter=4 7/8"; Discharge Height "Y"=16"; Discharge Width "X"=19"; Duct Inlet=2"; Filter LH=No; Filter RH=No; Height=20"; Induct Center C=10"; Induct Center D=24"; Induct Filter D=41 3/4"; Induction D=41"; Inlet Left=No; Inlet Right=Yes; Length=48"; Model=ESTS/DOAS; Radius=2 7/16"; Row F=6"; Second Pipe H=2 1/8"; URL=https://www.anemostat-hvac.com; Width=48"
- ESTS/DOAS 3/4-hp - 05R W/6ROW NO Filter: Connect H=1 7/16"; Connect Length=4 1/4"; Connector for 6ROW LS=Yes; Connector for 6ROW RS=No; Description=DOAS SERIES FAN POWERED AIR TERMINAL; Diameter=4 7/8"; Discharge Height "Y"=16"; Discharge Width "X"=19"; Duct Inlet=2"; Filter LH=No; Filter RH=No; Height=20"; Induct Center C=10"; Induct Center D=24"; Induct Filter D=41 3/4"; Induction D=41"; Inlet Left=No; Inlet Right=Yes; Length=48"; Model=ESTS/DOAS; Radius=2 7/16"; Row F=8"; Second Pipe H=4 1/8"; URL=https://www.anemostat-hvac.com; Width=48"
- ESTS/DOAS 3/4-hp - 05L W/4ROW & Filter: Connect H=1 7/16"; Connect Length=4 1/4"; Connector for 6ROW LS=No; Connector for 6ROW RS=No; Description=DOAS SERIES FAN POWERED AIR TERMINAL; Diameter=4 7/8"; Discharge Height "Y"=16"; Discharge Width "X"=19"; Duct Inlet=2"; Filter LH=No; Filter RH=Yes; Height=20"; Induct Center C=10"; Induct Center D=24"; Induct Filter D=41 3/4"; Induction D=41"; Inlet Left=Yes; Inlet Right=No; Length=48"; Model=ESTS/DOAS; Radius=2 7/16"; Row F=6"; Second Pipe H=2 1/8"; URL=https://www.anemostat-hvac.com; Width=48"
- ESTS/DOAS 3/4-hp - 05L W/6ROW & Filter: Connect H=1 7/16"; Connect Length=4 1/4"; Connector for 6ROW LS=No; Connector for 6ROW RS=Yes; Description=DOAS SERIES FAN POWERED AIR TERMINAL; Diameter=4 7/8"; Discharge Height "Y"=16"; Discharge Width "X"=19"; Duct Inlet=2"; Filter LH=No; Filter RH=Yes; Height=20"; Induct Center C=10"; Induct Center D=24"; Induct Filter D=41 3/4"; Induction D=41"; Inlet Left=Yes; Inlet Right=No; Length=48"; Model=ESTS/DOAS; Radius=2 7/16"; Row F=8"; Second Pipe H=4 1/8"; URL=https://www.anemostat-hvac.com; Width=48"
- ESTS/DOAS 1-hp - 16R W/4ROW NO Filter: Connect H=1 5/16"; Connect Length=4 1/4"; Connector for 6ROW LS=No; Connector for 6ROW RS=No; Description=Series Fan Powered Air Terminal with ECM Motor; Diameter=15 7/8"; Discharge Height "Y"=16"; Discharge Width "X"=19"; Duct Inlet=8"; Filter LH=No; Filter RH=No; Height=20"; Induct Center C=10"; Induct Center D=24"; Induct Filter D=41 3/4"; Induction D=41"; Inlet Left=No; Inlet Right=Yes; Length=48"; Model=ESTS; Radius=7 15/16"; Row F=6"; Second Pipe H=2 1/8"; URL=http://www.anemostat.com; Width=48"
- ESTS/DOAS 1-hp - 16R W/6ROW NO Filter: Connect H=1 5/16"; Connect Length=4 1/4"; Connector for 6ROW LS=Yes; Connector for 6ROW RS=No; Description=Series Fan Powered Air Terminal with ECM Motor; Diameter=15 7/8"; Discharge Height "Y"=16"; Discharge Width "X"=19"; Duct Inlet=8"; Filter LH=No; Filter RH=No; Height=20"; Induct Center C=10"; Induct Center D=24"; Induct Filter D=41 3/4"; Induction D=41"; Inlet Left=No; Inlet Right=Yes; Length=48"; Model=ESTS; Radius=7 15/16"; Row F=8"; Second Pipe H=4 1/8"; URL=http://www.anemostat.com; Width=48"
- ESTS/DOAS 1-hp - 16R W/4ROW & Filter: Connect H=1 5/16"; Connect Length=4 1/4"; Connector for 6ROW LS=No; Connector for 6ROW RS=No; Description=Series Fan Powered Air Terminal with ECM Motor; Diameter=15 7/8"; Discharge Height "Y"=16"; Discharge Width "X"=19"; Duct Inlet=8"; Filter LH=Yes; Filter RH=No; Height=20"; Induct Center C=10"; Induct Center D=24"; Induct Filter D=41 3/4"; Induction D=41"; Inlet Left=No; Inlet Right=Yes; Length=48"; Model=ESTS; Radius=7 15/16"; Row F=6"; Second Pipe H=2 1/8"; URL=http://www.anemostat.com; Width=48"
- ESTS/DOAS 1-hp - 16R W/6ROW & Filter: Connect H=1 5/16"; Connect Length=4 1/4"; Connector for 6ROW LS=Yes; Connector for 6ROW RS=No; Description=Series Fan Powered Air Terminal with ECM Motor; Diameter=15 7/8"; Discharge Height "Y"=16"; Discharge Width "X"=19"; Duct Inlet=8"; Filter LH=Yes; Filter RH=No; Height=20"; Induct Center C=10"; Induct Center D=24"; Induct Filter D=41 3/4"; Induction D=41"; Inlet Left=No; Inlet Right=Yes; Length=48"; Model=ESTS; Radius=7 15/16"; Row F=8"; Second Pipe H=4 1/8"; URL=http://www.anemostat.com; Width=48"
- ESTS/DOAS 1-hp - 16L W/2ROW NO Filter: Connect H=1 7/16"; Connect Length=4 1/2"; Connector for 6ROW LS=No; Connector for 6ROW RS=No; Description=DOAS SERIES FAN POWERED AIR TERMINAL; Diameter=15 7/8"; Discharge Height "Y"=16"; Discharge Width "X"=19"; Duct Inlet=8"; Filter LH=No; Filter RH=No; Height=20"; Induct Center C=10"; Induct Center D=24"; Induct Filter D=41 3/4"; Induction D=41"; Inlet Left=Yes; Inlet Right=No; Length=48"; Model=ESTS/DOAS; Radius=7 15/16"; Row F=4"; Second Pipe H=1/8"; URL=https://www.anemostat-hvac.com; Width=48"
- ESTS/DOAS 1-hp - 16L W/4ROW NO Filter: Connect H=1 7/16"; Connect Length=4 1/2"; Connector for 6ROW LS=No; Connector for 6ROW RS=Yes; Description=DOAS SERIES FAN POWERED AIR TERMINAL; Diameter=15 7/8"; Discharge Height "Y"=16"; Discharge Width "X"=19"; Duct Inlet=8"; Filter LH=No; Filter RH=No; Height=20"; Induct Center C=10"; Induct Center D=24"; Induct Filter D=41 3/4"; Induction D=41"; Inlet Left=Yes; Inlet Right=No; Length=48"; Model=ESTS/DOAS; Radius=7 15/16"; Row F=6"; Second Pipe H=2 1/8"; URL=https://www.anemostat-hvac.com; Width=48"
- ESTS/DOAS 1-hp - 16L W/6ROW NO Filter: Connect H=1 7/16"; Connect Length=4 1/2"; Connector for 6ROW LS=No; Connector for 6ROW RS=Yes; Description=DOAS SERIES FAN POWERED AIR TERMINAL; Diameter=15 7/8"; Discharge Height "Y"=16"; Discharge Width "X"=19"; Duct Inlet=8"; Filter LH=No; Filter RH=No; Height=20"; Induct Center C=10"; Induct Center D=24"; Induct Filter D=41 3/4"; Induction D=41"; Inlet Left=Yes; Inlet Right=No; Length=48"; Model=ESTS/DOAS; Radius=7 15/16"; Row F=8"; Second Pipe H=4 1/8"; URL=https://www.anemostat-hvac.com; Width=48"
- ESTS/DOAS 1-hp - 16L W/4ROW & Filter: Connect H=1 7/16"; Connect Length=4 1/2"; Connector for 6ROW LS=No; Connector for 6ROW RS=No; Description=DOAS SERIES FAN POWERED AIR TERMINAL; Diameter=15 7/8"; Discharge Height "Y"=16"; Discharge Width "X"=19"; Duct Inlet=8"; Filter LH=No; Filter RH=Yes; Height=20"; Induct Center C=10"; Induct Center D=24"; Induct Filter D=41 3/4"; Induction D=41"; Inlet Left=Yes; Inlet Right=No; Length=48"; Model=ESTS/DOAS; Radius=7 15/16"; Row F=6"; Second Pipe H=2 1/8"; URL=https://www.anemostat-hvac.com; Width=48"
- ESTS/DOAS 1-hp - 16L W/6ROW & Filter: Connect H=1 7/16"; Connect Length=4 1/2"; Connector for 6ROW LS=No; Connector for 6ROW RS=Yes; Description=DOAS SERIES FAN POWERED AIR TERMINAL; Diameter=15 7/8"; Discharge Height "Y"=16"; Discharge Width "X"=19"; Duct Inlet=8"; Filter LH=No; Filter RH=Yes; Height=20"; Induct Center C=10"; Induct Center D=24"; Induct Filter D=41 3/4"; Induction D=41"; Inlet Left=Yes; Inlet Right=No; Length=48"; Model=ESTS/DOAS; Radius=7 15/16"; Row F=8"; Second Pipe H=4 1/8"; URL=https://www.anemostat-hvac.com; Width=48"
- ESTS/DOAS 1-hp - 14L W/4ROW & Filter: Connect H=1 7/16"; Connect Length=4 1/2"; Connector for 6ROW LS=No; Connector for 6ROW RS=No; Description=DOAS SERIES FAN POWERED AIR TERMINAL; Diameter=13 7/8"; Discharge Height "Y"=16"; Discharge Width "X"=19"; Duct Inlet=7"; Filter LH=No; Filter RH=Yes; Height=20"; Induct Center C=10"; Induct Center D=24"; Induct Filter D=41 3/4"; Induction D=41"; Inlet Left=Yes; Inlet Right=No; Length=48"; Model=ESTS/DOAS; Radius=6 15/16"; Row F=6"; Second Pipe H=2 1/8"; URL=https://www.anemostat-hvac.com; Width=48"
- ESTS/DOAS 1-hp - 14L W/6ROW & Filter: Connect H=1 7/16"; Connect Length=4 1/2"; Connector for 6ROW LS=No; Connector for 6ROW RS=Yes; Description=DOAS SERIES FAN POWERED AIR TERMINAL; Diameter=13 7/8"; Discharge Height "Y"=16"; Discharge Width "X"=19"; Duct Inlet=7"; Filter LH=No; Filter RH=Yes; Height=20"; Induct Center C=10"; Induct Center D=24"; Induct Filter D=41 3/4"; Induction D=41"; Inlet Left=Yes; Inlet Right=No; Length=48"; Model=ESTS/DOAS; Radius=6 15/16"; Row F=8"; Second Pipe H=4 1/8"; URL=https://www.anemostat-hvac.com; Width=48"
- ESTS/DOAS 1-hp - 14R W/4ROW NO Filter: Connect H=1 5/16"; Connect Length=4 1/4"; Connector for 6ROW LS=No; Connector for 6ROW RS=No; Description=Series Fan Powered Air Terminal with ECM Motor; Diameter=13 7/8"; Discharge Height "Y"=16"; Discharge Width "X"=19"; Duct Inlet=7"; Filter LH=No; Filter RH=No; Height=20"; Induct Center C=10"; Induct Center D=24"; Induct Filter D=41 3/4"; Induction D=41"; Inlet Left=No; Inlet Right=Yes; Length=48"; Model=ESTS; Radius=6 15/16"; Row F=6"; Second Pipe H=2 1/8"; URL=http://www.anemostat.com; Width=48"
- ESTS/DOAS 1-hp - 14R W/6ROW NO Filter: Connect H=1 5/16"; Connect Length=4 1/4"; Connector for 6ROW LS=Yes; Connector for 6ROW RS=No; Description=Series Fan Powered Air Terminal with ECM Motor; Diameter=13 7/8"; Discharge Height "Y"=16"; Discharge Width "X"=19"; Duct Inlet=7"; Filter LH=No; Filter RH=No; Height=20"; Induct Center C=10"; Induct Center D=24"; Induct Filter D=41 3/4"; Induction D=41"; Inlet Left=No; Inlet Right=Yes; Length=48"; Model=ESTS; Radius=6 15/16"; Row F=8"; Second Pipe H=4 1/8"; URL=http://www.anemostat.com; Width=48"
- ESTS/DOAS 1-hp - 14L W/4ROW NO Filter: Connect H=1 7/16"; Connect Length=4 1/4"; Connector for 6ROW LS=Yes; Connector for 6ROW RS=No; Description=DOAS SERIES FAN POWERED AIR TERMINAL; Diameter=13 7/8"; Discharge Height "Y"=16"; Discharge Width "X"=19"; Duct Inlet=7"; Filter LH=No; Filter RH=No; Height=20"; Induct Center C=10"; Induct Center D=24"; Induct Filter D=41 3/4"; Induction D=41"; Inlet Left=Yes; Inlet Right=No; Length=48"; Model=ESTS/DOAS; Radius=6 15/16"; Row F=6"; Second Pipe H=2 1/8"; URL=https://www.anemostat-hvac.com; Width=48"
- ESTS/DOAS 1-hp - 14L W/6ROW NO Filter: Connect H=1 7/16"; Connect Length=4 1/4"; Connector for 6ROW LS=No; Connector for 6ROW RS=Yes; Description=DOAS SERIES FAN POWERED AIR TERMINAL; Diameter=13 7/8"; Discharge Height "Y"=16"; Discharge Width "X"=19"; Duct Inlet=7"; Filter LH=No; Filter RH=No; Height=20"; Induct Center C=10"; Induct Center D=24"; Induct Filter D=41 3/4"; Induction D=41"; Inlet Left=Yes; Inlet Right=No; Length=48"; Model=ESTS/DOAS; Radius=6 15/16"; Row F=8"; Second Pipe H=4 1/8"; URL=https://www.anemostat-hvac.com; Width=48"
- ESTS/DOAS 1-hp - 14R W/4ROW & Filter: Connect H=1 5/16"; Connect Length=4 1/4"; Connector for 6ROW LS=No; Connector for 6ROW RS=No; Description=Series Fan Powered Air Terminal with ECM Motor; Diameter=13 7/8"; Discharge Height "Y"=16"; Discharge Width "X"=19"; Duct Inlet=7"; Filter LH=Yes; Filter RH=No; Height=20"; Induct Center C=10"; Induct Center D=24"; Induct Filter D=41 3/4"; Induction D=41"; Inlet Left=No; Inlet Right=Yes; Length=48"; Model=ESTS; Radius=6 15/16"; Row F=6"; Second Pipe H=2 1/8"; URL=http://www.anemostat.com; Width=48"
- ESTS/DOAS 1-hp - 14R W/6ROW & Filter: Connect H=1 5/16"; Connect Length=4 1/4"; Connector for 6ROW LS=No; Connector for 6ROW RS=No; Description=Series Fan Powered Air Terminal with ECM Motor; Diameter=13 7/8"; Discharge Height "Y"=16"; Discharge Width "X"=19"; Duct Inlet=7"; Filter LH=Yes; Filter RH=No; Height=20"; Induct Center C=10"; Induct Center D=24"; Induct Filter D=41 3/4"; Induction D=41"; Inlet Left=No; Inlet Right=Yes; Length=48"; Model=ESTS; Radius=6 15/16"; Row F=8"; Second Pipe H=4 1/8"; URL=http://www.anemostat.com; Width=48"
- ESTS/DOAS 1-hp - 10L W/2ROW & Filter: Connect H=1 7/16"; Connect Length=4 1/2"; Connector for 6ROW LS=No; Connector for 6ROW RS=No; Description=DOAS SERIES FAN POWERED AIR TERMINAL; Diameter=9 7/8"; Discharge Height "Y"=16"; Discharge Width "X"=19"; Duct Inlet=5"; Filter LH=No; Filter RH=Yes; Height=20"; Induct Center C=10"; Induct Center D=24"; Induct Filter D=41 3/4"; Induction D=41"; Inlet Left=Yes; Inlet Right=No; Length=48"; Model=ESTS/DOAS; Radius=4 15/16"; Row F=4"; Second Pipe H=1/8"; URL=https://www.anemostat-hvac.com; Width=48"
- ESTS/DOAS 1-hp - 10L W/4ROW & Filter: Connect H=1 7/16"; Connect Length=4 1/2"; Connector for 6ROW LS=No; Connector for 6ROW RS=No; Description=DOAS SERIES FAN POWERED AIR TERMINAL; Diameter=9 7/8"; Discharge Height "Y"=16"; Discharge Width "X"=19"; Duct Inlet=5"; Filter LH=No; Filter RH=Yes; Height=20"; Induct Center C=10"; Induct Center D=24"; Induct Filter D=41 3/4"; Induction D=41"; Inlet Left=Yes; Inlet Right=No; Length=48"; Model=ESTS/DOAS; Radius=4 15/16"; Row F=6"; Second Pipe H=2 1/8"; URL=https://www.anemostat-hvac.com; Width=48"
- ESTS/DOAS 1-hp - 10L W/6ROW & Filter: Connect H=1 7/16"; Connect Length=4 1/2"; Connector for 6ROW LS=No; Connector for 6ROW RS=Yes; Description=DOAS SERIES FAN POWERED AIR TERMINAL; Diameter=9 7/8"; Discharge Height "Y"=16"; Discharge Width "X"=19"; Duct Inlet=5"; Filter LH=No; Filter RH=Yes; Height=20"; Induct Center C=10"; Induct Center D=24"; Induct Filter D=41 3/4"; Induction D=41"; Inlet Left=Yes; Inlet Right=No; Length=48"; Model=ESTS/DOAS; Radius=4 15/16"; Row F=8"; Second Pipe H=4 1/8"; URL=https://www.anemostat-hvac.com; Width=48"
- ESTS/DOAS 1-hp - 10L W/2ROW NO Filter: Connect H=1 7/16"; Connect Length=4 1/2"; Connector for 6ROW LS=No; Connector for 6ROW RS=No; Description=DOAS SERIES FAN POWERED AIR TERMINAL; Diameter=9 7/8"; Discharge Height "Y"=16"; Discharge Width "X"=19"; Duct Inlet=5"; Filter LH=No; Filter RH=No; Height=20"; Induct Center C=10"; Induct Center D=24"; Induct Filter D=41 3/4"; Induction D=41"; Inlet Left=Yes; Inlet Right=No; Length=48"; Model=ESTS/DOAS; Radius=4 15/16"; Row F=4"; Second Pipe H=1/8"; URL=https://www.anemostat-hvac.com; Width=48"
- ESTS/DOAS 1-hp - 10L W/4ROW NO Filter: Connect H=1 7/16"; Connect Length=4 1/2"; Connector for 6ROW LS=No; Connector for 6ROW RS=No; Description=DOAS SERIES FAN POWERED AIR TERMINAL; Diameter=9 7/8"; Discharge Height "Y"=16"; Discharge Width "X"=19"; Duct Inlet=5"; Filter LH=No; Filter RH=No; Height=20"; Induct Center C=10"; Induct Center D=24"; Induct Filter D=41 3/4"; Induction D=41"; Inlet Left=Yes; Inlet Right=No; Length=48"; Model=ESTS/DOAS; Radius=4 15/16"; Row F=6"; Second Pipe H=2 1/8"; URL=https://www.anemostat-hvac.com; Width=48"
- ESTS/DOAS 1-hp - 10L W/6ROW NO Filter: Connect H=1 7/16"; Connect Length=4 1/2"; Connector for 6ROW LS=No; Connector for 6ROW RS=Yes; Description=DOAS SERIES FAN POWERED AIR TERMINAL; Diameter=9 7/8"; Discharge Height "Y"=16"; Discharge Width "X"=19"; Duct Inlet=5"; Filter LH=No; Filter RH=No; Height=20"; Induct Center C=10"; Induct Center D=24"; Induct Filter D=41 3/4"; Induction D=41"; Inlet Left=Yes; Inlet Right=No; Length=48"; Model=ESTS/DOAS; Radius=4 15/16"; Row F=8"; Second Pipe H=4 1/8"; URL=https://www.anemostat-hvac.com; Width=48"
- ESTS/DOAS 1-hp - 10R W/4ROW & Filter: Connect H=1 5/16"; Connect Length=4 1/4"; Connector for 6ROW LS=No; Connector for 6ROW RS=No; Description=Series Fan Powered Air Terminal with ECM Motor; Diameter=9 7/8"; Discharge Height "Y"=16"; Discharge Width "X"=19"; Duct Inlet=5"; Filter LH=Yes; Filter RH=No; Height=20"; Induct Center C=10"; Induct Center D=24"; Induct Filter D=41 3/4"; Induction D=41"; Inlet Left=No; Inlet Right=Yes; Length=48"; Model=ESTS; Radius=4 15/16"; Row F=6"; Second Pipe H=2 1/8"; URL=http://www.anemostat.com; Width=48"
- ESTS/DOAS 1-hp - 10R W/6ROW & Filter: Connect H=1 5/16"; Connect Length=4 1/4"; Connector for 6ROW LS=Yes; Connector for 6ROW RS=No; Description=Series Fan Powered Air Terminal with ECM Motor; Diameter=9 7/8"; Discharge Height "Y"=16"; Discharge Width "X"=19"; Duct Inlet=5"; Filter LH=Yes; Filter RH=No; Height=20"; Induct Center C=10"; Induct Center D=24"; Induct Filter D=41 3/4"; Induction D=41"; Inlet Left=No; Inlet Right=Yes; Length=48"; Model=ESTS; Radius=4 15/16"; Row F=8"; Second Pipe H=4 1/8"; URL=http://www.anemostat.com; Width=48"
- ESTS/DOAS 1-hp - 10R W/4ROW NO Filter: Connect H=1 5/16"; Connect Length=4 1/4"; Connector for 6ROW LS=No; Connector for 6ROW RS=No; Description=Series Fan Powered Air Terminal with ECM Motor; Diameter=9 7/8"; Discharge Height "Y"=16"; Discharge Width "X"=19"; Duct Inlet=5"; Filter LH=No; Filter RH=No; Height=20"; Induct Center C=10"; Induct Center D=24"; Induct Filter D=41 3/4"; Induction D=41"; Inlet Left=No; Inlet Right=Yes; Length=48"; Model=ESTS; Radius=4 15/16"; Row F=6"; Second Pipe H=2 1/8"; URL=http://www.anemostat.com; Width=48"
- ESTS/DOAS 1-hp - 10R W/6ROW NO Filter: Connect H=1 5/16"; Connect Length=4 1/4"; Connector for 6ROW LS=Yes; Connector for 6ROW RS=No; Description=Series Fan Powered Air Terminal with ECM Motor; Diameter=9 7/8"; Discharge Height "Y"=16"; Discharge Width "X"=19"; Duct Inlet=5"; Filter LH=No; Filter RH=No; Height=20"; Induct Center C=10"; Induct Center D=24"; Induct Filter D=41 3/4"; Induction D=41"; Inlet Left=No; Inlet Right=Yes; Length=48"; Model=ESTS; Radius=4 15/16"; Row F=8"; Second Pipe H=4 1/8"; URL=http://www.anemostat.com; Width=48"
- ESTS/DOAS 1-hp - 09L W/2ROW & Filter: Connect H=1 7/16"; Connect Length=4 1/2"; Connector for 6ROW LS=No; Connector for 6ROW RS=No; Description=DOAS SERIES FAN POWERED AIR TERMINAL; Diameter=8 7/8"; Discharge Height "Y"=16"; Discharge Width "X"=19"; Duct Inlet=4"; Filter LH=No; Filter RH=Yes; Height=20"; Induct Center C=10"; Induct Center D=24"; Induct Filter D=41 3/4"; Induction D=41"; Inlet Left=Yes; Inlet Right=No; Length=48"; Model=ESTS/DOAS; Radius=4 7/16"; Row F=4"; Second Pipe H=1/8"; URL=https://www.anemostat-hvac.com; Width=48"
- ESTS/DOAS 1-hp - 09L W/4ROW & Filter: Connect H=1 7/16"; Connect Length=4 1/2"; Connector for 6ROW LS=No; Connector for 6ROW RS=No; Description=DOAS SERIES FAN POWERED AIR TERMINAL; Diameter=8 7/8"; Discharge Height "Y"=16"; Discharge Width "X"=19"; Duct Inlet=4"; Filter LH=No; Filter RH=Yes; Height=20"; Induct Center C=10"; Induct Center D=24"; Induct Filter D=41 3/4"; Induction D=41"; Inlet Left=Yes; Inlet Right=No; Length=48"; Model=ESTS/DOAS; Radius=4 7/16"; Row F=6"; Second Pipe H=2 1/8"; URL=https://www.anemostat-hvac.com; Width=48"
- ESTS/DOAS 1-hp - 09L W/6ROW & Filter: Connect H=1 7/16"; Connect Length=4 1/2"; Connector for 6ROW LS=No; Connector for 6ROW RS=Yes; Description=DOAS SERIES FAN POWERED AIR TERMINAL; Diameter=8 7/8"; Discharge Height "Y"=16"; Discharge Width "X"=19"; Duct Inlet=4"; Filter LH=No; Filter RH=Yes; Height=20"; Induct Center C=10"; Induct Center D=24"; Induct Filter D=41 3/4"; Induction D=41"; Inlet Left=Yes; Inlet Right=No; Length=48"; Model=ESTS/DOAS; Radius=4 7/16"; Row F=8"; Second Pipe H=4 1/8"; URL=https://www.anemostat-hvac.com; Width=48"
- ESTS/DOAS 1-hp - 09R W/4ROW NO Filter: Connect H=1 5/16"; Connect Length=4 1/4"; Connector for 6ROW LS=No; Connector for 6ROW RS=No; Description=Series Fan Powered Air Terminal with ECM Motor; Diameter=8 7/8"; Discharge Height "Y"=16"; Discharge Width "X"=19"; Duct Inlet=4"; Filter LH=No; Filter RH=No; Height=20"; Induct Center C=10"; Induct Center D=24"; Induct Filter D=41 3/4"; Induction D=41"; Inlet Left=No; Inlet Right=Yes; Length=48"; Model=ESTS; Radius=4 7/16"; Row F=6"; Second Pipe H=2 1/8"; URL=http://www.anemostat.com; Width=48"
- ESTS/DOAS 1-hp - 09R W/6ROW NO Filter: Connect H=1 5/16"; Connect Length=4 1/4"; Connector for 6ROW LS=Yes; Connector for 6ROW RS=No; Description=Series Fan Powered Air Terminal with ECM Motor; Diameter=8 7/8"; Discharge Height "Y"=16"; Discharge Width "X"=19"; Duct Inlet=4"; Filter LH=No; Filter RH=No; Height=20"; Induct Center C=10"; Induct Center D=24"; Induct Filter D=41 3/4"; Induction D=41"; Inlet Left=No; Inlet Right=Yes; Length=48"; Model=ESTS; Radius=4 7/16"; Row F=8"; Second Pipe H=4 1/8"; URL=http://www.anemostat.com; Width=48"
- ESTS/DOAS 1-hp - 09R W/4ROW & Filter: Connect H=1 5/16"; Connect Length=4 1/4"; Connector for 6ROW LS=No; Connector for 6ROW RS=No; Description=Series Fan Powered Air Terminal with ECM Motor; Diameter=8 7/8"; Discharge Height "Y"=16"; Discharge Width "X"=19"; Duct Inlet=4"; Filter LH=Yes; Filter RH=No; Height=20"; Induct Center C=10"; Induct Center D=24"; Induct Filter D=41 3/4"; Induction D=41"; Inlet Left=No; Inlet Right=Yes; Length=48"; Model=ESTS; Radius=4 7/16"; Row F=6"; Second Pipe H=2 1/8"; URL=http://www.anemostat.com; Width=48"
- ESTS/DOAS 1-hp - 09R W/6ROW & Filter: Connect H=1 5/16"; Connect Length=4 1/4"; Connector for 6ROW LS=Yes; Connector for 6ROW RS=No; Description=Series Fan Powered Air Terminal with ECM Motor; Diameter=8 7/8"; Discharge Height "Y"=16"; Discharge Width "X"=19"; Duct Inlet=4"; Filter LH=Yes; Filter RH=No; Height=20"; Induct Center C=10"; Induct Center D=24"; Induct Filter D=41 3/4"; Induction D=41"; Inlet Left=No; Inlet Right=Yes; Length=48"; Model=ESTS; Radius=4 7/16"; Row F=8"; Second Pipe H=4 1/8"; URL=http://www.anemostat.com; Width=48"
- ESTS/DOAS 1-hp - 09L W/2ROW NO Filter: Connect H=1 7/16"; Connect Length=4 1/2"; Connector for 6ROW LS=No; Connector for 6ROW RS=No; Description=DOAS SERIES FAN POWERED AIR TERMINAL; Diameter=8 7/8"; Discharge Height "Y"=16"; Discharge Width "X"=19"; Duct Inlet=4"; Filter LH=No; Filter RH=No; Height=20"; Induct Center C=10"; Induct Center D=24"; Induct Filter D=41 3/4"; Induction D=41"; Inlet Left=Yes; Inlet Right=No; Length=48"; Model=ESTS/DOAS; Radius=4 7/16"; Row F=4"; Second Pipe H=1/8"; URL=https://www.anemostat-hvac.com; Width=48"
- ESTS/DOAS 1-hp - 09L W/4ROW NO Filter: Connect H=1 7/16"; Connect Length=4 1/2"; Connector for 6ROW LS=No; Connector for 6ROW RS=No; Description=DOAS SERIES FAN POWERED AIR TERMINAL; Diameter=8 7/8"; Discharge Height "Y"=16"; Discharge Width "X"=19"; Duct Inlet=4"; Filter LH=No; Filter RH=No; Height=20"; Induct Center C=10"; Induct Center D=24"; Induct Filter D=41 3/4"; Induction D=41"; Inlet Left=Yes; Inlet Right=No; Length=48"; Model=ESTS/DOAS; Radius=4 7/16"; Row F=6"; Second Pipe H=2 1/8"; URL=https://www.anemostat-hvac.com; Width=48"
- ESTS/DOAS 1-hp - 09L W/6ROW NO Filter: Connect H=1 7/16"; Connect Length=4 1/2"; Connector for 6ROW LS=No; Connector for 6ROW RS=Yes; Description=DOAS SERIES FAN POWERED AIR TERMINAL; Diameter=8 7/8"; Discharge Height "Y"=16"; Discharge Width "X"=19"; Duct Inlet=4"; Filter LH=No; Filter RH=No; Height=20"; Induct Center C=10"; Induct Center D=24"; Induct Filter D=41 3/4"; Induction D=41"; Inlet Left=Yes; Inlet Right=No; Length=48"; Model=ESTS/DOAS; Radius=4 7/16"; Row F=8"; Second Pipe H=4 1/8"; URL=https://www.anemostat-hvac.com; Width=48"
- ESTS/DOAS 1-hp - 08R W/4ROW & Filter: Connect H=1 5/16"; Connect Length=4 1/4"; Connector for 6ROW LS=No; Connector for 6ROW RS=No; Description=Series Fan Powered Air Terminal with ECM Motor; Diameter=7 7/8"; Discharge Height "Y"=16"; Discharge Width "X"=19"; Duct Inlet=4"; Filter LH=Yes; Filter RH=No; Height=20"; Induct Center C=10"; Induct Center D=24"; Induct Filter D=41 3/4"; Induction D=41"; Inlet Left=No; Inlet Right=Yes; Length=48"; Model=ESTS; Radius=3 15/16"; Row F=6"; Second Pipe H=2 1/8"; URL=http://www.anemostat.com; Width=48"
- ESTS/DOAS 1-hp - 08R W/6ROW & Filter: Connect H=1 5/16"; Connect Length=4 1/4"; Connector for 6ROW LS=Yes; Connector for 6ROW RS=No; Description=Series Fan Powered Air Terminal with ECM Motor; Diameter=7 7/8"; Discharge Height "Y"=16"; Discharge Width "X"=19"; Duct Inlet=4"; Filter LH=Yes; Filter RH=No; Height=20"; Induct Center C=10"; Induct Center D=24"; Induct Filter D=41 3/4"; Induction D=41"; Inlet Left=No; Inlet Right=Yes; Length=48"; Model=ESTS; Radius=3 15/16"; Row F=8"; Second Pipe H=4 1/8"; URL=http://www.anemostat.com; Width=48"
- ESTS/DOAS 1-hp - 08R W/4ROW NO Filter: Connect H=1 5/16"; Connect Length=4 1/4"; Connector for 6ROW LS=No; Connector for 6ROW RS=No; Description=Series Fan Powered Air Terminal with ECM Motor; Diameter=7 7/8"; Discharge Height "Y"=16"; Discharge Width "X"=19"; Duct Inlet=4"; Filter LH=No; Filter RH=No; Height=20"; Induct Center C=10"; Induct Center D=24"; Induct Filter D=41 3/4"; Induction D=41"; Inlet Left=No; Inlet Right=Yes; Length=48"; Model=ESTS; Radius=3 15/16"; Row F=6"; Second Pipe H=2 1/8"; URL=http://www.anemostat.com; Width=48"
- ESTS/DOAS 1-hp - 08R W/6ROW NO Filter: Connect H=1 5/16"; Connect Length=4 1/4"; Connector for 6ROW LS=Yes; Connector for 6ROW RS=No; Description=Series Fan Powered Air Terminal with ECM Motor; Diameter=7 7/8"; Discharge Height "Y"=16"; Discharge Width "X"=19"; Duct Inlet=4"; Filter LH=No; Filter RH=No; Height=20"; Induct Center C=10"; Induct Center D=24"; Induct Filter D=41 3/4"; Induction D=41"; Inlet Left=No; Inlet Right=Yes; Length=48"; Model=ESTS; Radius=3 15/16"; Row F=8"; Second Pipe H=4 1/8"; URL=http://www.anemostat.com; Width=48"
- ESTS/DOAS 1-hp - 08L W/2ROW & Filter: Connect H=1 7/16"; Connect Length=4 1/2"; Connector for 6ROW LS=No; Connector for 6ROW RS=No; Description=DOAS SERIES FAN POWERED AIR TERMINAL; Diameter=7 7/8"; Discharge Height "Y"=16"; Discharge Width "X"=19"; Duct Inlet=4"; Filter LH=No; Filter RH=Yes; Height=20"; Induct Center C=10"; Induct Center D=24"; Induct Filter D=41 3/4"; Induction D=41"; Inlet Left=Yes; Inlet Right=No; Length=48"; Model=ESTS/DOAS; Radius=3 15/16"; Row F=4"; Second Pipe H=1/8"; URL=https://www.anemostat-hvac.com; Width=48"
- ESTS/DOAS 1-hp - 08L W/4ROW & Filter: Connect H=1 7/16"; Connect Length=4 1/2"; Connector for 6ROW LS=No; Connector for 6ROW RS=No; Description=DOAS SERIES FAN POWERED AIR TERMINAL; Diameter=7 7/8"; Discharge Height "Y"=16"; Discharge Width "X"=19"; Duct Inlet=4"; Filter LH=No; Filter RH=Yes; Height=20"; Induct Center C=10"; Induct Center D=24"; Induct Filter D=41 3/4"; Induction D=41"; Inlet Left=Yes; Inlet Right=No; Length=48"; Model=ESTS/DOAS; Radius=3 15/16"; Row F=6"; Second Pipe H=2 1/8"; URL=https://www.anemostat-hvac.com; Width=48"
- ESTS/DOAS 1-hp - 08L W/6ROW & Filter: Connect H=1 7/16"; Connect Length=4 1/2"; Connector for 6ROW LS=No; Connector for 6ROW RS=Yes; Description=DOAS SERIES FAN POWERED AIR TERMINAL; Diameter=7 7/8"; Discharge Height "Y"=16"; Discharge Width "X"=19"; Duct Inlet=4"; Filter LH=No; Filter RH=Yes; Height=20"; Induct Center C=10"; Induct Center D=24"; Induct Filter D=41 3/4"; Induction D=41"; Inlet Left=Yes; Inlet Right=No; Length=48"; Model=ESTS/DOAS; Radius=3 15/16"; Row F=8"; Second Pipe H=4 1/8"; URL=https://www.anemostat-hvac.com; Width=48"
- ESTS/DOAS 1-hp - 08L W/2ROW NO Filter: Connect H=1 7/16"; Connect Length=4 1/2"; Connector for 6ROW LS=No; Connector for 6ROW RS=No; Description=DOAS SERIES FAN POWERED AIR TERMINAL; Diameter=7 7/8"; Discharge Height "Y"=16"; Discharge Width "X"=19"; Duct Inlet=4"; Filter LH=No; Filter RH=Yes; Height=20"; Induct Center C=10"; Induct Center D=24"; Induct Filter D=41 3/4"; Induction D=41"; Inlet Left=Yes; Inlet Right=No; Length=48"; Model=ESTS/DOAS; Radius=3 15/16"; Row F=4"; Second Pipe H=1/8"; URL=https://www.anemostat-hvac.com; Width=48"
- ESTS/DOAS 1-hp - 08L W/4ROW NO Filter: Connect H=1 7/16"; Connect Length=4 1/2"; Connector for 6ROW LS=No; Connector for 6ROW RS=No; Description=DOAS SERIES FAN POWERED AIR TERMINAL; Diameter=7 7/8"; Discharge Height "Y"=16"; Discharge Width "X"=19"; Duct Inlet=4"; Filter LH=No; Filter RH=No; Height=20"; Induct Center C=10"; Induct Center D=24"; Induct Filter D=41 3/4"; Induction D=41"; Inlet Left=Yes; Inlet Right=No; Length=48"; Model=ESTS/DOAS; Radius=3 15/16"; Row F=6"; Second Pipe H=2 1/8"; URL=https://www.anemostat-hvac.com; Width=48"
- ESTS/DOAS 1-hp - 08L W/6ROW NO Filter: Connect H=1 7/16"; Connect Length=4 1/2"; Connector for 6ROW LS=No; Connector for 6ROW RS=Yes; Description=DOAS SERIES FAN POWERED AIR TERMINAL; Diameter=7 7/8"; Discharge Height "Y"=16"; Discharge Width "X"=19"; Duct Inlet=4"; Filter LH=No; Filter RH=No; Height=20"; Induct Center C=10"; Induct Center D=24"; Induct Filter D=41 3/4"; Induction D=41"; Inlet Left=Yes; Inlet Right=No; Length=48"; Model=ESTS/DOAS; Radius=3 15/16"; Row F=8"; Second Pipe H=4 1/8"; URL=https://www.anemostat-hvac.com; Width=48"
- ESTS/DOAS 1-hp - 07R W/4ROW & Filter: Connect H=1 5/16"; Connect Length=4 1/4"; Connector for 6ROW LS=No; Connector for 6ROW RS=No; Description=Series Fan Powered Air Terminal with ECM Motor; Diameter=6 7/8"; Discharge Height "Y"=16"; Discharge Width "X"=19"; Duct Inlet=3"; Filter LH=Yes; Filter RH=No; Height=20"; Induct Center C=10"; Induct Center D=24"; Induct Filter D=41 3/4"; Induction D=41"; Inlet Left=No; Inlet Right=Yes; Length=48"; Model=ESTS; Radius=3 7/16"; Row F=6"; Second Pipe H=2 1/8"; URL=http://www.anemostat.com; Width=48"
- ESTS/DOAS 1-hp - 07R W/6ROW & Filter: Connect H=1 5/16"; Connect Length=4 1/4"; Connector for 6ROW LS=Yes; Connector for 6ROW RS=No; Description=Series Fan Powered Air Terminal with ECM Motor; Diameter=6 7/8"; Discharge Height "Y"=16"; Discharge Width "X"=19"; Duct Inlet=3"; Filter LH=Yes; Filter RH=No; Height=20"; Induct Center C=10"; Induct Center D=24"; Induct Filter D=41 3/4"; Induction D=41"; Inlet Left=No; Inlet Right=Yes; Length=48"; Model=ESTS; Radius=3 7/16"; Row F=8"; Second Pipe H=4 1/8"; URL=http://www.anemostat.com; Width=48"
- ESTS/DOAS 1-hp - 07R W/4ROW NO Filter: Connect H=1 5/16"; Connect Length=4 1/4"; Connector for 6ROW LS=No; Connector for 6ROW RS=No; Description=Series Fan Powered Air Terminal with ECM Motor; Diameter=6 7/8"; Discharge Height "Y"=16"; Discharge Width "X"=19"; Duct Inlet=3"; Filter LH=No; Filter RH=No; Height=20"; Induct Center C=10"; Induct Center D=24"; Induct Filter D=41 3/4"; Induction D=41"; Inlet Left=No; Inlet Right=Yes; Length=48"; Model=ESTS; Radius=3 7/16"; Row F=6"; Second Pipe H=2 1/8"; URL=http://www.anemostat.com; Width=48"
- ESTS/DOAS 1-hp - 07R W/6ROW NO Filter: Connect H=1 5/16"; Connect Length=4 1/4"; Connector for 6ROW LS=Yes; Connector for 6ROW RS=No; Description=Series Fan Powered Air Terminal with ECM Motor; Diameter=6 7/8"; Discharge Height "Y"=16"; Discharge Width "X"=19"; Duct Inlet=3"; Filter LH=No; Filter RH=No; Height=20"; Induct Center C=10"; Induct Center D=24"; Induct Filter D=41 3/4"; Induction D=41"; Inlet Left=No; Inlet Right=Yes; Length=48"; Model=ESTS; Radius=3 7/16"; Row F=8"; Second Pipe H=4 1/8"; URL=http://www.anemostat.com; Width=48"
- ESTS/DOAS 1-hp - 07L W/2ROW & Filter: Connect H=1 7/16"; Connect Length=4 1/2"; Connector for 6ROW LS=No; Connector for 6ROW RS=No; Description=DOAS SERIES FAN POWERED AIR TERMINAL; Diameter=6 7/8"; Discharge Height "Y"=16"; Discharge Width "X"=19"; Duct Inlet=3"; Filter LH=No; Filter RH=Yes; Height=20"; Induct Center C=10"; Induct Center D=24"; Induct Filter D=41 3/4"; Induction D=41"; Inlet Left=Yes; Inlet Right=No; Length=48"; Model=ESTS/DOAS; Radius=3 7/16"; Row F=4"; Second Pipe H=1/8"; URL=https://www.anemostat-hvac.com; Width=48"
- ESTS/DOAS 1-hp - 07L W/4ROW & Filter: Connect H=1 7/16"; Connect Length=4 1/2"; Connector for 6ROW LS=No; Connector for 6ROW RS=No; Description=DOAS SERIES FAN POWERED AIR TERMINAL; Diameter=6 7/8"; Discharge Height "Y"=16"; Discharge Width "X"=19"; Duct Inlet=3"; Filter LH=No; Filter RH=Yes; Height=20"; Induct Center C=10"; Induct Center D=24"; Induct Filter D=41 3/4"; Induction D=41"; Inlet Left=Yes; Inlet Right=No; Length=48"; Model=ESTS/DOAS; Radius=3 7/16"; Row F=6"; Second Pipe H=2 1/8"; URL=https://www.anemostat-hvac.com; Width=48"
- ESTS/DOAS 1-hp - 07L W/6ROW & Filter: Connect H=1 7/16"; Connect Length=4 1/2"; Connector for 6ROW LS=No; Connector for 6ROW RS=Yes; Description=DOAS SERIES FAN POWERED AIR TERMINAL; Diameter=6 7/8"; Discharge Height "Y"=16"; Discharge Width "X"=19"; Duct Inlet=3"; Filter LH=No; Filter RH=Yes; Height=20"; Induct Center C=10"; Induct Center D=24"; Induct Filter D=41 3/4"; Induction D=41"; Inlet Left=Yes; Inlet Right=No; Length=48"; Model=ESTS/DOAS; Radius=3 7/16"; Row F=8"; Second Pipe H=4 1/8"; URL=https://www.anemostat-hvac.com; Width=48"
- ESTS/DOAS 1-hp - 07L W/2ROW NO Filter: Connect H=1 7/16"; Connect Length=4 1/2"; Connector for 6ROW LS=No; Connector for 6ROW RS=No; Description=DOAS SERIES FAN POWERED AIR TERMINAL; Diameter=6 7/8"; Discharge Height "Y"=16"; Discharge Width "X"=19"; Duct Inlet=3"; Filter LH=No; Filter RH=Yes; Height=20"; Induct Center C=10"; Induct Center D=24"; Induct Filter D=41 3/4"; Induction D=41"; Inlet Left=Yes; Inlet Right=No; Length=48"; Model=ESTS/DOAS; Radius=3 7/16"; Row F=4"; Second Pipe H=1/8"; URL=https://www.anemostat-hvac.com; Width=48"
- ESTS/DOAS 1-hp - 07L W/4ROW NO Filter: Connect H=1 7/16"; Connect Length=4 1/2"; Connector for 6ROW LS=No; Connector for 6ROW RS=No; Description=DOAS SERIES FAN POWERED AIR TERMINAL; Diameter=6 7/8"; Discharge Height "Y"=16"; Discharge Width "X"=19"; Duct Inlet=3"; Filter LH=No; Filter RH=Yes; Height=20"; Induct Center C=10"; Induct Center D=24"; Induct Filter D=41 3/4"; Induction D=41"; Inlet Left=Yes; Inlet Right=No; Length=48"; Model=ESTS/DOAS; Radius=3 7/16"; Row F=6"; Second Pipe H=2 1/8"; URL=https://www.anemostat-hvac.com; Width=48"
- ESTS/DOAS 1-hp - 07L W/6ROW NO Filter: Connect H=1 7/16"; Connect Length=4 1/2"; Connector for 6ROW LS=No; Connector for 6ROW RS=Yes; Description=DOAS SERIES FAN POWERED AIR TERMINAL; Diameter=6 7/8"; Discharge Height "Y"=16"; Discharge Width "X"=19"; Duct Inlet=3"; Filter LH=No; Filter RH=Yes; Height=20"; Induct Center C=10"; Induct Center D=24"; Induct Filter D=41 3/4"; Induction D=41"; Inlet Left=Yes; Inlet Right=No; Length=48"; Model=ESTS/DOAS; Radius=3 7/16"; Row F=8"; Second Pipe H=4 1/8"; URL=https://www.anemostat-hvac.com; Width=48"
- ESTS/DOAS 1-hp - 06R W/4ROW & Filter: Connect H=1 5/16"; Connect Length=4 1/4"; Connector for 6ROW LS=No; Connector for 6ROW RS=No; Description=Series Fan Powered Air Terminal with ECM Motor; Diameter=5 7/8"; Discharge Height "Y"=16"; Discharge Width "X"=19"; Duct Inlet=3"; Filter LH=Yes; Filter RH=No; Height=20"; Induct Center C=10"; Induct Center D=24"; Induct Filter D=41 3/4"; Induction D=41"; Inlet Left=No; Inlet Right=Yes; Length=48"; Model=ESTS; Radius=2 15/16"; Row F=6"; Second Pipe H=2 1/8"; URL=http://www.anemostat.com; Width=48"
- ESTS/DOAS 1-hp - 06R W/6ROW & Filter: Connect H=1 5/16"; Connect Length=4 1/4"; Connector for 6ROW LS=Yes; Connector for 6ROW RS=No; Description=Series Fan Powered Air Terminal with ECM Motor; Diameter=5 7/8"; Discharge Height "Y"=16"; Discharge Width "X"=19"; Duct Inlet=3"; Filter LH=Yes; Filter RH=No; Height=20"; Induct Center C=10"; Induct Center D=24"; Induct Filter D=41 3/4"; Induction D=41"; Inlet Left=No; Inlet Right=Yes; Length=48"; Model=ESTS; Radius=2 15/16"; Row F=8"; Second Pipe H=4 1/8"; URL=http://www.anemostat.com; Width=48"
- ESTS/DOAS 1-hp - 06R W/4ROW NO Filter: Connect H=1 5/16"; Connect Length=4 1/4"; Connector for 6ROW LS=No; Connector for 6ROW RS=No; Description=Series Fan Powered Air Terminal with ECM Motor; Diameter=5 7/8"; Discharge Height "Y"=16"; Discharge Width "X"=19"; Duct Inlet=3"; Filter LH=No; Filter RH=No; Height=20"; Induct Center C=10"; Induct Center D=24"; Induct Filter D=41 3/4"; Induction D=41"; Inlet Left=No; Inlet Right=Yes; Length=48"; Model=ESTS; Radius=2 15/16"; Row F=6"; Second Pipe H=2 1/8"; URL=http://www.anemostat.com; Width=48"
- ESTS/DOAS 1-hp - 06R W/6ROW NO Filter: Connect H=1 5/16"; Connect Length=4 1/4"; Connector for 6ROW LS=Yes; Connector for 6ROW RS=No; Description=Series Fan Powered Air Terminal with ECM Motor; Diameter=5 7/8"; Discharge Height "Y"=16"; Discharge Width "X"=19"; Duct Inlet=3"; Filter LH=No; Filter RH=No; Height=20"; Induct Center C=10"; Induct Center D=24"; Induct Filter D=41 3/4"; Induction D=41"; Inlet Left=No; Inlet Right=Yes; Length=48"; Model=ESTS; Radius=2 15/16"; Row F=8"; Second Pipe H=4 1/8"; URL=http://www.anemostat.com; Width=48"
- ESTS/DOAS 1-hp - 06L W/2ROW & Filter: Connect H=1 7/16"; Connect Length=4 1/2"; Connector for 6ROW LS=No; Connector for 6ROW RS=No; Description=DOAS SERIES FAN POWERED AIR TERMINAL; Diameter=5 7/8"; Discharge Height "Y"=16"; Discharge Width "X"=19"; Duct Inlet=3"; Filter LH=No; Filter RH=Yes; Height=20"; Induct Center C=10"; Induct Center D=24"; Induct Filter D=41 3/4"; Induction D=41"; Inlet Left=Yes; Inlet Right=No; Length=48"; Model=ESTS/DOAS; Radius=2 15/16"; Row F=4"; Second Pipe H=1/8"; URL=https://www.anemostat-hvac.com; Width=48"
- ESTS/DOAS 1-hp - 06L W/4ROW & Filter: Connect H=1 7/16"; Connect Length=4 1/2"; Connector for 6ROW LS=No; Connector for 6ROW RS=No; Description=DOAS SERIES FAN POWERED AIR TERMINAL; Diameter=5 7/8"; Discharge Height "Y"=16"; Discharge Width "X"=19"; Duct Inlet=3"; Filter LH=No; Filter RH=Yes; Height=20"; Induct Center C=10"; Induct Center D=24"; Induct Filter D=41 3/4"; Induction D=41"; Inlet Left=Yes; Inlet Right=No; Length=48"; Model=ESTS/DOAS; Radius=2 15/16"; Row F=6"; Second Pipe H=2 1/8"; URL=https://www.anemostat-hvac.com; Width=48"
- ESTS/DOAS 1-hp - 06L W/6ROW & Filter: Connect H=1 7/16"; Connect Length=4 1/2"; Connector for 6ROW LS=No; Connector for 6ROW RS=Yes; Description=DOAS SERIES FAN POWERED AIR TERMINAL; Diameter=5 7/8"; Discharge Height "Y"=16"; Discharge Width "X"=19"; Duct Inlet=3"; Filter LH=No; Filter RH=Yes; Height=20"; Induct Center C=10"; Induct Center D=24"; Induct Filter D=41 3/4"; Induction D=41"; Inlet Left=Yes; Inlet Right=No; Length=48"; Model=ESTS/DOAS; Radius=2 15/16"; Row F=8"; Second Pipe H=4 1/8"; URL=https://www.anemostat-hvac.com; Width=48"
- ESTS/DOAS 1-hp - 06L W/2ROW NO Filter: Connect H=1 7/16"; Connect Length=4 1/2"; Connector for 6ROW LS=No; Connector for 6ROW RS=No; Description=DOAS SERIES FAN POWERED AIR TERMINAL; Diameter=5 7/8"; Discharge Height "Y"=16"; Discharge Width "X"=19"; Duct Inlet=3"; Filter LH=No; Filter RH=No; Height=20"; Induct Center C=10"; Induct Center D=24"; Induct Filter D=41 3/4"; Induction D=41"; Inlet Left=Yes; Inlet Right=No; Length=48"; Model=ESTS/DOAS; Radius=2 15/16"; Row F=4"; Second Pipe H=1/8"; URL=https://www.anemostat-hvac.com; Width=48"
- ESTS/DOAS 1-hp - 06L W/4ROW NO Filter: Connect H=1 7/16"; Connect Length=4 1/2"; Connector for 6ROW LS=No; Connector for 6ROW RS=No; Description=DOAS SERIES FAN POWERED AIR TERMINAL; Diameter=7 1/8"; Discharge Height "Y"=16"; Discharge Width "X"=19"; Duct Inlet=4"; Filter LH=No; Filter RH=No; Height=20"; Induct Center C=10"; Induct Center D=24"; Induct Filter D=41 3/4"; Induction D=41"; Inlet Left=Yes; Inlet Right=No; Length=48"; Model=ESTS/DOAS; Radius=3 9/16"; Row F=6"; Second Pipe H=2 1/8"; URL=https://www.anemostat-hvac.com; Width=48"
- ESTS/DOAS 1-hp - 06L W/6ROW NO Filter: Connect H=1 7/16"; Connect Length=4 1/2"; Connector for 6ROW LS=No; Connector for 6ROW RS=Yes; Description=DOAS SERIES FAN POWERED AIR TERMINAL; Diameter=7 1/8"; Discharge Height "Y"=16"; Discharge Width "X"=19"; Duct Inlet=4"; Filter LH=No; Filter RH=No; Height=20"; Induct Center C=10"; Induct Center D=24"; Induct Filter D=41 3/4"; Induction D=41"; Inlet Left=Yes; Inlet Right=No; Length=48"; Model=ESTS/DOAS; Radius=3 9/16"; Row F=8"; Second Pipe H=4 1/8"; URL=https://www.anemostat-hvac.com; Width=48"
- ESTS/DOAS 1-hp - 05R W/4ROW & Filter: Connect H=1 5/16"; Connect Length=4 1/4"; Connector for 6ROW LS=No; Connector for 6ROW RS=No; Description=Series Fan Powered Air Terminal with ECM Motor; Diameter=4 7/8"; Discharge Height "Y"=16"; Discharge Width "X"=19"; Duct Inlet=2"; Filter LH=Yes; Filter RH=No; Height=20"; Induct Center C=10"; Induct Center D=24"; Induct Filter D=41 3/4"; Induction D=41"; Inlet Left=No; Inlet Right=Yes; Length=48"; Model=ESTS; Radius=2 7/16"; Row F=6"; Second Pipe H=2 1/8"; URL=http://www.anemostat.com; Width=48"
- ESTS/DOAS 1-hp - 05R W/6ROW & Filter: Connect H=1 5/16"; Connect Length=4 1/4"; Connector for 6ROW LS=Yes; Connector for 6ROW RS=No; Description=Series Fan Powered Air Terminal with ECM Motor; Diameter=4 7/8"; Discharge Height "Y"=16"; Discharge Width "X"=19"; Duct Inlet=2"; Filter LH=Yes; Filter RH=No; Height=20"; Induct Center C=10"; Induct Center D=24"; Induct Filter D=41 3/4"; Induction D=41"; Inlet Left=No; Inlet Right=Yes; Length=48"; Model=ESTS; Radius=2 7/16"; Row F=8"; Second Pipe H=4 1/8"; URL=http://www.anemostat.com; Width=48"
- ESTS/DOAS 1-hp - 05R W/4ROW NO Filter: Connect H=1 5/16"; Connect Length=4 1/4"; Connector for 6ROW LS=No; Connector for 6ROW RS=No; Description=Series Fan Powered Air Terminal with ECM Motor; Diameter=4 7/8"; Discharge Height "Y"=16"; Discharge Width "X"=19"; Duct Inlet=2"; Filter LH=No; Filter RH=No; Height=20"; Induct Center C=10"; Induct Center D=24"; Induct Filter D=41 3/4"; Induction D=41"; Inlet Left=No; Inlet Right=Yes; Length=48"; Model=ESTS; Radius=2 7/16"; Row F=6"; Second Pipe H=2 1/8"; URL=http://www.anemostat.com; Width=48"
- ESTS/DOAS 1-hp - 05R W/6ROW NO Filter: Connect H=1 5/16"; Connect Length=4 1/4"; Connector for 6ROW LS=Yes; Connector for 6ROW RS=No; Description=Series Fan Powered Air Terminal with ECM Motor; Diameter=4 7/8"; Discharge Height "Y"=16"; Discharge Width "X"=19"; Duct Inlet=2"; Filter LH=No; Filter RH=No; Height=20"; Induct Center C=10"; Induct Center D=24"; Induct Filter D=41 3/4"; Induction D=41"; Inlet Left=No; Inlet Right=Yes; Length=48"; Model=ESTS; Radius=2 7/16"; Row F=8"; Second Pipe H=4 1/8"; URL=http://www.anemostat.com; Width=48"
- ESTS/DOAS 1-hp - 05L W/2ROW & Filter: Connect H=1 7/16"; Connect Length=4 1/2"; Connector for 6ROW LS=No; Connector for 6ROW RS=No; Description=DOAS SERIES FAN POWERED AIR TERMINAL; Diameter=4 7/8"; Discharge Height "Y"=16"; Discharge Width "X"=19"; Duct Inlet=2"; Filter LH=No; Filter RH=Yes; Height=20"; Induct Center C=10"; Induct Center D=24"; Induct Filter D=41 3/4"; Induction D=41"; Inlet Left=Yes; Inlet Right=No; Length=48"; Model=ESTS/DOAS; Radius=2 7/16"; Row F=4"; Second Pipe H=1/8"; URL=https://www.anemostat-hvac.com; Width=48"
- ESTS/DOAS 1-hp - 05L W/4ROW & Filter: Connect H=1 7/16"; Connect Length=4 1/2"; Connector for 6ROW LS=No; Connector for 6ROW RS=No; Description=DOAS SERIES FAN POWERED AIR TERMINAL; Diameter=4 7/8"; Discharge Height "Y"=16"; Discharge Width "X"=19"; Duct Inlet=2"; Filter LH=No; Filter RH=Yes; Height=20"; Induct Center C=10"; Induct Center D=24"; Induct Filter D=41 3/4"; Induction D=41"; Inlet Left=Yes; Inlet Right=No; Length=48"; Model=ESTS/DOAS; Radius=2 7/16"; Row F=6"; Second Pipe H=2 1/8"; URL=https://www.anemostat-hvac.com; Width=48"
- ESTS/DOAS 1-hp - 05L W/6ROW & Filter: Connect H=1 7/16"; Connect Length=4 1/2"; Connector for 6ROW LS=No; Connector for 6ROW RS=Yes; Description=DOAS SERIES FAN POWERED AIR TERMINAL; Diameter=4 7/8"; Discharge Height "Y"=16"; Discharge Width "X"=19"; Duct Inlet=2"; Filter LH=No; Filter RH=Yes; Height=20"; Induct Center C=10"; Induct Center D=24"; Induct Filter D=41 3/4"; Induction D=41"; Inlet Left=Yes; Inlet Right=No; Length=48"; Model=ESTS/DOAS; Radius=2 7/16"; Row F=8"; Second Pipe H=4 1/8"; URL=https://www.anemostat-hvac.com; Width=48"
- ESTS/DOAS 1-hp - 05L W/2ROW NO Filter: Connect H=1 7/16"; Connect Length=4 1/2"; Connector for 6ROW LS=No; Connector for 6ROW RS=No; Description=DOAS SERIES FAN POWERED AIR TERMINAL; Diameter=4 7/8"; Discharge Height "Y"=16"; Discharge Width "X"=19"; Duct Inlet=2"; Filter LH=No; Filter RH=No; Height=20"; Induct Center C=10"; Induct Center D=24"; Induct Filter D=41 3/4"; Induction D=41"; Inlet Left=Yes; Inlet Right=No; Length=48"; Model=ESTS/DOAS; Radius=2 7/16"; Row F=4"; Second Pipe H=1/8"; URL=https://www.anemostat-hvac.com; Width=48"
- ESTS/DOAS 1-hp - 05L W/4ROW NO Filter: Connect H=1 7/16"; Connect Length=4 1/2"; Connector for 6ROW LS=No; Connector for 6ROW RS=No; Description=DOAS SERIES FAN POWERED AIR TERMINAL; Diameter=4 7/8"; Discharge Height "Y"=16"; Discharge Width "X"=19"; Duct Inlet=2"; Filter LH=No; Filter RH=No; Height=20"; Induct Center C=10"; Induct Center D=24"; Induct Filter D=41 3/4"; Induction D=41"; Inlet Left=Yes; Inlet Right=No; Length=48"; Model=ESTS/DOAS; Radius=2 7/16"; Row F=6"; Second Pipe H=2 1/8"; URL=https://www.anemostat-hvac.com; Width=48"
- ESTS/DOAS 1-hp - 05L W/6ROW NO Filter: Connect H=1 7/16"; Connect Length=4 1/2"; Connector for 6ROW LS=No; Connector for 6ROW RS=Yes; Description=DOAS SERIES FAN POWERED AIR TERMINAL; Diameter=4 7/8"; Discharge Height "Y"=16"; Discharge Width "X"=19"; Duct Inlet=2"; Filter LH=No; Filter RH=No; Height=20"; Induct Center C=10"; Induct Center D=24"; Induct Filter D=41 3/4"; Induction D=41"; Inlet Left=Yes; Inlet Right=No; Length=48"; Model=ESTS/DOAS; Radius=2 7/16"; Row F=8"; Second Pipe H=4 1/8"; URL=https://www.anemostat-hvac.com; Width=48"
- ESTS/DOAS 1/2-hp - 05L W/4ROW & Filter: Connect H=1 7/16"; Connect Length=4 1/2"; Connector for 6ROW LS=No; Connector for 6ROW RS=No; Description=DOAS SERIES FAN POWERED AIR TERMINAL; Diameter=4 7/8"; Discharge Height "Y"=12"; Discharge Width "X"=14"; Duct Inlet=2"; Filter LH=No; Filter RH=Yes; Height=18"; Induct Center C=9"; Induct Center D=20"; Induct Filter D=33 3/4"; Induction D=33"; Inlet Left=Yes; Inlet Right=No; Length=40"; Model=ESTS/DOAS; Radius=2 7/16"; Row F=6"; Second Pipe H=2 1/8"; URL=https://www.anemostat-hvac.com; Width=40"
- ESTS/DOAS 1/2-hp - 05L W/6ROW & Filter: Connect H=1 7/16"; Connect Length=4 1/2"; Connector for 6ROW LS=No; Connector for 6ROW RS=Yes; Description=DOAS SERIES FAN POWERED AIR TERMINAL; Diameter=4 7/8"; Discharge Height "Y"=12"; Discharge Width "X"=14"; Duct Inlet=2"; Filter LH=No; Filter RH=Yes; Height=18"; Induct Center C=9"; Induct Center D=20"; Induct Filter D=33 3/4"; Induction D=33"; Inlet Left=Yes; Inlet Right=No; Length=40"; Model=ESTS/DOAS; Radius=2 7/16"; Row F=8"; Second Pipe H=4 1/8"; URL=https://www.anemostat-hvac.com; Width=40"
- ESTS/DOAS 1/2-hp - 05L W/4ROW NO Filter: Connect H=1 7/16"; Connect Length=4 1/2"; Connector for 6ROW LS=No; Connector for 6ROW RS=No; Description=DOAS SERIES FAN POWERED AIR TERMINAL; Diameter=4 7/8"; Discharge Height "Y"=12"; Discharge Width "X"=14"; Duct Inlet=2"; Filter LH=No; Filter RH=No; Height=18"; Induct Center C=9"; Induct Center D=20"; Induct Filter D=33 3/4"; Induction D=33"; Inlet Left=Yes; Inlet Right=No; Length=40"; Model=ESTS/DOAS; Radius=2 7/16"; Row F=6"; Second Pipe H=2 1/8"; URL=https://www.anemostat-hvac.com; Width=40"
- ESTS/DOAS 1/2-hp - 05L W/6ROW NO Filter: Connect H=1 7/16"; Connect Length=4 1/2"; Connector for 6ROW LS=No; Connector for 6ROW RS=Yes; Description=DOAS SERIES FAN POWERED AIR TERMINAL; Diameter=4 7/8"; Discharge Height "Y"=12"; Discharge Width "X"=14"; Duct Inlet=2"; Filter LH=No; Filter RH=No; Height=18"; Induct Center C=9"; Induct Center D=20"; Induct Filter D=33 3/4"; Induction D=33"; Inlet Left=Yes; Inlet Right=No; Length=40"; Model=ESTS/DOAS; Radius=2 7/16"; Row F=8"; Second Pipe H=4 1/8"; URL=https://www.anemostat-hvac.com; Width=40"
- ESTS/DOAS 1/2-hp - 05R W/4ROW & Filter: Connect H=1 7/16"; Connect Length=4 1/2"; Connector for 6ROW LS=No; Connector for 6ROW RS=No; Description=DOAS SERIES FAN POWERED AIR TERMINAL; Diameter=4 7/8"; Discharge Height "Y"=12"; Discharge Width "X"=14"; Duct Inlet=2"; Filter LH=Yes; Filter RH=No; Height=18"; Induct Center C=9"; Induct Center D=20"; Induct Filter D=33 3/4"; Induction D=33"; Inlet Left=No; Inlet Right=Yes; Length=40"; Model=ESTS/DOAS; Radius=2 7/16"; Row F=6"; Second Pipe H=2 1/8"; URL=https://www.anemostat-hvac.com; Width=40"
- ESTS/DOAS 1/2-hp - 05R W/6ROW & Filter: Connect H=1 7/16"; Connect Length=4 1/2"; Connector for 6ROW LS=Yes; Connector for 6ROW RS=No; Description=DOAS SERIES FAN POWERED AIR TERMINAL; Diameter=4 7/8"; Discharge Height "Y"=12"; Discharge Width "X"=14"; Duct Inlet=2"; Filter LH=Yes; Filter RH=No; Height=18"; Induct Center C=9"; Induct Center D=20"; Induct Filter D=33 3/4"; Induction D=33"; Inlet Left=No; Inlet Right=Yes; Length=40"; Model=ESTS/DOAS; Radius=2 7/16"; Row F=8"; Second Pipe H=4 1/8"; URL=https://www.anemostat-hvac.com; Width=40"
- ESTS/DOAS 1/2-hp - 05R W/4ROW NO Filter: Connect H=1 7/16"; Connect Length=4 1/2"; Connector for 6ROW LS=No; Connector for 6ROW RS=No; Description=DOAS SERIES FAN POWERED AIR TERMINAL; Diameter=4 7/8"; Discharge Height "Y"=12"; Discharge Width "X"=14"; Duct Inlet=2"; Filter LH=No; Filter RH=No; Height=18"; Induct Center C=9"; Induct Center D=20"; Induct Filter D=33 3/4"; Induction D=33"; Inlet Left=No; Inlet Right=Yes; Length=40"; Model=ESTS/DOAS; Radius=2 7/16"; Row F=6"; Second Pipe H=2 1/8"; URL=https://www.anemostat-hvac.com; Width=40"
- ESTS/DOAS 1/2-hp - 05R W/6ROW NO Filter: Connect H=1 7/16"; Connect Length=4 1/2"; Connector for 6ROW LS=Yes; Connector for 6ROW RS=No; Description=DOAS SERIES FAN POWERED AIR TERMINAL; Diameter=4 7/8"; Discharge Height "Y"=12"; Discharge Width "X"=14"; Duct Inlet=2"; Filter LH=No; Filter RH=No; Height=18"; Induct Center C=9"; Induct Center D=20"; Induct Filter D=33 3/4"; Induction D=33"; Inlet Left=No; Inlet Right=Yes; Length=40"; Model=ESTS/DOAS; Radius=2 7/16"; Row F=8"; Second Pipe H=4 1/8"; URL=https://www.anemostat-hvac.com; Width=40"
- ESTS/DOAS 1/2-hp - 06L W/4ROW & Filter: Connect H=1 7/16"; Connect Length=4 1/2"; Connector for 6ROW LS=No; Connector for 6ROW RS=No; Description=DOAS SERIES FAN POWERED AIR TERMINAL; Diameter=5 7/8"; Discharge Height "Y"=12"; Discharge Width "X"=14"; Duct Inlet=3"; Filter LH=No; Filter RH=Yes; Height=18"; Induct Center C=9"; Induct Center D=20"; Induct Filter D=33 3/4"; Induction D=33"; Inlet Left=Yes; Inlet Right=No; Length=40"; Model=ESTS/DOAS; Radius=2 15/16"; Row F=6"; Second Pipe H=2 1/8"; URL=https://www.anemostat-hvac.com; Width=40"
- ESTS/DOAS 1/2-hp - 06L W/6ROW & Filter: Connect H=1 7/16"; Connect Length=4 1/2"; Connector for 6ROW LS=No; Connector for 6ROW RS=Yes; Description=DOAS SERIES FAN POWERED AIR TERMINAL; Diameter=5 7/8"; Discharge Height "Y"=12"; Discharge Width "X"=14"; Duct Inlet=3"; Filter LH=No; Filter RH=Yes; Height=18"; Induct Center C=9"; Induct Center D=20"; Induct Filter D=33 3/4"; Induction D=33"; Inlet Left=Yes; Inlet Right=No; Length=40"; Model=ESTS/DOAS; Radius=2 15/16"; Row F=8"; Second Pipe H=4 1/8"; URL=https://www.anemostat-hvac.com; Width=40"
- ESTS/DOAS 1/2-hp - 06L W/4ROW NO Filter: Connect H=1 7/16"; Connect Length=4 1/2"; Connector for 6ROW LS=No; Connector for 6ROW RS=No; Description=DOAS SERIES FAN POWERED AIR TERMINAL; Diameter=5 7/8"; Discharge Height "Y"=12"; Discharge Width "X"=14"; Duct Inlet=3"; Filter LH=No; Filter RH=No; Height=18"; Induct Center C=9"; Induct Center D=20"; Induct Filter D=33 3/4"; Induction D=33"; Inlet Left=Yes; Inlet Right=No; Length=40"; Model=ESTS/DOAS; Radius=2 15/16"; Row F=6"; Second Pipe H=2 1/8"; URL=https://www.anemostat-hvac.com; Width=40"
- ESTS/DOAS 1/2-hp - 06L W/6ROW NO Filter: Connect H=1 7/16"; Connect Length=4 1/2"; Connector for 6ROW LS=No; Connector for 6ROW RS=Yes; Description=DOAS SERIES FAN POWERED AIR TERMINAL; Diameter=5 7/8"; Discharge Height "Y"=12"; Discharge Width "X"=14"; Duct Inlet=3"; Filter LH=No; Filter RH=No; Height=18"; Induct Center C=9"; Induct Center D=20"; Induct Filter D=33 3/4"; Induction D=33"; Inlet Left=Yes; Inlet Right=No; Length=40"; Model=ESTS/DOAS; Radius=2 15/16"; Row F=8"; Second Pipe H=4 1/8"; URL=https://www.anemostat-hvac.com; Width=40"
- ESTS/DOAS 1/2-hp - 06R W/4ROW & Filter: Connect H=1 7/16"; Connect Length=4 1/2"; Connector for 6ROW LS=No; Connector for 6ROW RS=No; Description=DOAS SERIES FAN POWERED AIR TERMINAL; Diameter=5 7/8"; Discharge Height "Y"=12"; Discharge Width "X"=14"; Duct Inlet=3"; Filter LH=Yes; Filter RH=No; Height=18"; Induct Center C=9"; Induct Center D=20"; Induct Filter D=33 3/4"; Induction D=33"; Inlet Left=No; Inlet Right=Yes; Length=40"; Model=ESTS/DOAS; Radius=2 15/16"; Row F=6"; Second Pipe H=2 1/8"; URL=https://www.anemostat-hvac.com; Width=40"
- ESTS/DOAS 1/2-hp - 06R W/6ROW & Filter: Connect H=1 7/16"; Connect Length=4 1/2"; Connector for 6ROW LS=Yes; Connector for 6ROW RS=No; Description=DOAS SERIES FAN POWERED AIR TERMINAL; Diameter=5 7/8"; Discharge Height "Y"=12"; Discharge Width "X"=14"; Duct Inlet=3"; Filter LH=Yes; Filter RH=No; Height=18"; Induct Center C=9"; Induct Center D=20"; Induct Filter D=33 3/4"; Induction D=33"; Inlet Left=No; Inlet Right=Yes; Length=40"; Model=ESTS/DOAS; Radius=2 15/16"; Row F=8"; Second Pipe H=4 1/8"; URL=https://www.anemostat-hvac.com; Width=40"
- ESTS/DOAS 1/2-hp - 06R W/4ROW NO Filter: Connect H=1 7/16"; Connect Length=4 1/2"; Connector for 6ROW LS=No; Connector for 6ROW RS=No; Description=DOAS SERIES FAN POWERED AIR TERMINAL; Diameter=5 7/8"; Discharge Height "Y"=12"; Discharge Width "X"=14"; Duct Inlet=3"; Filter LH=No; Filter RH=No; Height=18"; Induct Center C=9"; Induct Center D=20"; Induct Filter D=33 3/4"; Induction D=33"; Inlet Left=No; Inlet Right=Yes; Length=40"; Model=ESTS/DOAS; Radius=2 15/16"; Row F=6"; Second Pipe H=2 1/8"; URL=https://www.anemostat-hvac.com; Width=40"
- ESTS/DOAS 1/2-hp - 06R W/6ROW NO Filter: Connect H=1 7/16"; Connect Length=4 1/2"; Connector for 6ROW LS=Yes; Connector for 6ROW RS=No; Description=DOAS SERIES FAN POWERED AIR TERMINAL; Diameter=5 7/8"; Discharge Height "Y"=12"; Discharge Width "X"=14"; Duct Inlet=3"; Filter LH=No; Filter RH=No; Height=18"; Induct Center C=9"; Induct Center D=20"; Induct Filter D=33 3/4"; Induction D=33"; Inlet Left=No; Inlet Right=Yes; Length=40"; Model=ESTS/DOAS; Radius=2 15/16"; Row F=8"; Second Pipe H=4 1/8"; URL=https://www.anemostat-hvac.com; Width=40"
- ESTS/DOAS 1/2-hp - 07L W/4ROW & Filter: Connect H=1 7/16"; Connect Length=4 1/2"; Connector for 6ROW LS=No; Connector for 6ROW RS=No; Description=DOAS SERIES FAN POWERED AIR TERMINAL; Diameter=6 7/8"; Discharge Height "Y"=12"; Discharge Width "X"=14"; Duct Inlet=3"; Filter LH=No; Filter RH=Yes; Height=18"; Induct Center C=9"; Induct Center D=20"; Induct Filter D=33 3/4"; Induction D=33"; Inlet Left=Yes; Inlet Right=No; Length=40"; Model=ESTS/DOAS; Radius=3 7/16"; Row F=6"; Second Pipe H=2 1/8"; URL=https://www.anemostat-hvac.com; Width=40"
- ESTS/DOAS 1/2-hp - 07L W/6ROW & Filter: Connect H=1 7/16"; Connect Length=4 1/2"; Connector for 6ROW LS=No; Connector for 6ROW RS=Yes; Description=DOAS SERIES FAN POWERED AIR TERMINAL; Diameter=6 7/8"; Discharge Height "Y"=12"; Discharge Width "X"=14"; Duct Inlet=3"; Filter LH=No; Filter RH=Yes; Height=18"; Induct Center C=9"; Induct Center D=20"; Induct Filter D=33 3/4"; Induction D=33"; Inlet Left=Yes; Inlet Right=No; Length=40"; Model=ESTS/DOAS; Radius=3 7/16"; Row F=8"; Second Pipe H=4 1/8"; URL=https://www.anemostat-hvac.com; Width=40"
- ESTS/DOAS 1/2-hp - 07L W/4ROW NO Filter: Connect H=1 7/16"; Connect Length=4 1/2"; Connector for 6ROW LS=No; Connector for 6ROW RS=No; Description=DOAS SERIES FAN POWERED AIR TERMINAL; Diameter=6 7/8"; Discharge Height "Y"=12"; Discharge Width "X"=14"; Duct Inlet=3"; Filter LH=No; Filter RH=No; Height=18"; Induct Center C=9"; Induct Center D=20"; Induct Filter D=33 3/4"; Induction D=33"; Inlet Left=Yes; Inlet Right=No; Length=40"; Model=ESTS/DOAS; Radius=3 7/16"; Row F=6"; Second Pipe H=2 1/8"; URL=https://www.anemostat-hvac.com; Width=40"
- ESTS/DOAS 1/2-hp - 07L W/6ROW NO Filter: Connect H=1 7/16"; Connect Length=4 1/2"; Connector for 6ROW LS=No; Connector for 6ROW RS=Yes; Description=DOAS SERIES FAN POWERED AIR TERMINAL; Diameter=6 7/8"; Discharge Height "Y"=12"; Discharge Width "X"=14"; Duct Inlet=3"; Filter LH=No; Filter RH=No; Height=18"; Induct Center C=9"; Induct Center D=20"; Induct Filter D=33 3/4"; Induction D=33"; Inlet Left=Yes; Inlet Right=No; Length=40"; Model=ESTS/DOAS; Radius=3 7/16"; Row F=8"; Second Pipe H=4 1/8"; URL=https://www.anemostat-hvac.com; Width=40"
- ESTS/DOAS 1/2-hp - 07R W/4ROW & Filter: Connect H=1 7/16"; Connect Length=4 1/2"; Connector for 6ROW LS=No; Connector for 6ROW RS=No; Description=DOAS SERIES FAN POWERED AIR TERMINAL; Diameter=6 7/8"; Discharge Height "Y"=12"; Discharge Width "X"=14"; Duct Inlet=3"; Filter LH=Yes; Filter RH=No; Height=18"; Induct Center C=9"; Induct Center D=20"; Induct Filter D=33 3/4"; Induction D=33"; Inlet Left=No; Inlet Right=Yes; Length=40"; Model=ESTS/DOAS; Radius=3 7/16"; Row F=6"; Second Pipe H=2 1/8"; URL=https://www.anemostat-hvac.com; Width=40"
- ESTS/DOAS 1/2-hp - 07R W/6ROW & Filter: Connect H=1 7/16"; Connect Length=4 1/2"; Connector for 6ROW LS=Yes; Connector for 6ROW RS=No; Description=DOAS SERIES FAN POWERED AIR TERMINAL; Diameter=6 7/8"; Discharge Height "Y"=12"; Discharge Width "X"=14"; Duct Inlet=3"; Filter LH=Yes; Filter RH=No; Height=18"; Induct Center C=9"; Induct Center D=20"; Induct Filter D=33 3/4"; Induction D=33"; Inlet Left=No; Inlet Right=Yes; Length=40"; Model=ESTS/DOAS; Radius=3 7/16"; Row F=8"; Second Pipe H=4 1/8"; URL=https://www.anemostat-hvac.com; Width=40"
- ESTS/DOAS 1/2-hp - 07R W/4ROW NO Filter: Connect H=1 7/16"; Connect Length=4 1/2"; Connector for 6ROW LS=No; Connector for 6ROW RS=No; Description=DOAS SERIES FAN POWERED AIR TERMINAL; Diameter=6 7/8"; Discharge Height "Y"=12"; Discharge Width "X"=14"; Duct Inlet=3"; Filter LH=No; Filter RH=No; Height=18"; Induct Center C=9"; Induct Center D=20"; Induct Filter D=33 3/4"; Induction D=33"; Inlet Left=No; Inlet Right=Yes; Length=40"; Model=ESTS/DOAS; Radius=3 7/16"; Row F=6"; Second Pipe H=2 1/8"; URL=https://www.anemostat-hvac.com; Width=40"
- ESTS/DOAS 1/2-hp - 07R W/6ROW NO Filter: Connect H=1 7/16"; Connect Length=4 1/2"; Connector for 6ROW LS=Yes; Connector for 6ROW RS=No; Description=DOAS SERIES FAN POWERED AIR TERMINAL; Diameter=6 7/8"; Discharge Height "Y"=12"; Discharge Width "X"=14"; Duct Inlet=3"; Filter LH=No; Filter RH=No; Height=18"; Induct Center C=9"; Induct Center D=20"; Induct Filter D=33 3/4"; Induction D=33"; Inlet Left=No; Inlet Right=Yes; Length=40"; Model=ESTS/DOAS; Radius=3 7/16"; Row F=8"; Second Pipe H=4 1/8"; URL=https://www.anemostat-hvac.com; Width=40"
- ESTS/DOAS 1/2-hp - 08L W/4ROW & Filter: Connect H=1 7/16"; Connect Length=4 1/2"; Connector for 6ROW LS=No; Connector for 6ROW RS=No; Description=DOAS SERIES FAN POWERED AIR TERMINAL; Diameter=7 7/8"; Discharge Height "Y"=12"; Discharge Width "X"=14"; Duct Inlet=4"; Filter LH=No; Filter RH=Yes; Height=18"; Induct Center C=9"; Induct Center D=20"; Induct Filter D=33 3/4"; Induction D=33"; Inlet Left=Yes; Inlet Right=No; Length=40"; Model=ESTS/DOAS; Radius=3 15/16"; Row F=6"; Second Pipe H=2 1/8"; URL=https://www.anemostat-hvac.com; Width=40"
- ESTS/DOAS 1/2-hp - 08L W/6ROW & Filter: Connect H=1 7/16"; Connect Length=4 1/2"; Connector for 6ROW LS=No; Connector for 6ROW RS=Yes; Description=DOAS SERIES FAN POWERED AIR TERMINAL; Diameter=7 7/8"; Discharge Height "Y"=12"; Discharge Width "X"=14"; Duct Inlet=4"; Filter LH=No; Filter RH=Yes; Height=18"; Induct Center C=9"; Induct Center D=20"; Induct Filter D=33 3/4"; Induction D=33"; Inlet Left=Yes; Inlet Right=No; Length=40"; Model=ESTS/DOAS; Radius=3 15/16"; Row F=8"; Second Pipe H=4 1/8"; URL=https://www.anemostat-hvac.com; Width=40"
- ESTS/DOAS 1/2-hp - 08L W/4ROW NO Filter: Connect H=1 7/16"; Connect Length=4 1/2"; Connector for 6ROW LS=No; Connector for 6ROW RS=No; Description=DOAS SERIES FAN POWERED AIR TERMINAL; Diameter=7 7/8"; Discharge Height "Y"=12"; Discharge Width "X"=14"; Duct Inlet=4"; Filter LH=No; Filter RH=No; Height=18"; Induct Center C=9"; Induct Center D=20"; Induct Filter D=33 3/4"; Induction D=33"; Inlet Left=Yes; Inlet Right=No; Length=40"; Model=ESTS/DOAS; Radius=3 15/16"; Row F=6"; Second Pipe H=2 1/8"; URL=https://www.anemostat-hvac.com; Width=40"
- ESTS/DOAS 1/2-hp - 08L W/6ROW NO Filter: Connect H=1 7/16"; Connect Length=4 1/2"; Connector for 6ROW LS=No; Connector for 6ROW RS=Yes; Description=DOAS SERIES FAN POWERED AIR TERMINAL; Diameter=7 7/8"; Discharge Height "Y"=12"; Discharge Width "X"=14"; Duct Inlet=4"; Filter LH=No; Filter RH=No; Height=18"; Induct Center C=9"; Induct Center D=20"; Induct Filter D=33 3/4"; Induction D=33"; Inlet Left=Yes; Inlet Right=No; Length=40"; Model=ESTS/DOAS; Radius=3 15/16"; Row F=8"; Second Pipe H=4 1/8"; URL=https://www.anemostat-hvac.com; Width=40"
- ESTS/DOAS 1/2-hp - 08R W/4ROW & Filter: Connect H=1 7/16"; Connect Length=4 1/2"; Connector for 6ROW LS=No; Connector for 6ROW RS=No; Description=DOAS SERIES FAN POWERED AIR TERMINAL; Diameter=7 7/8"; Discharge Height "Y"=12"; Discharge Width "X"=14"; Duct Inlet=4"; Filter LH=Yes; Filter RH=No; Height=18"; Induct Center C=9"; Induct Center D=20"; Induct Filter D=33 3/4"; Induction D=33"; Inlet Left=No; Inlet Right=Yes; Length=40"; Model=ESTS/DOAS; Radius=3 15/16"; Row F=6"; Second Pipe H=2 1/8"; URL=https://www.anemostat-hvac.com; Width=40"
- ESTS/DOAS 1/2-hp - 08R W/6ROW & Filter: Connect H=1 7/16"; Connect Length=4 1/2"; Connector for 6ROW LS=Yes; Connector for 6ROW RS=No; Description=DOAS SERIES FAN POWERED AIR TERMINAL; Diameter=7 7/8"; Discharge Height "Y"=12"; Discharge Width "X"=14"; Duct Inlet=4"; Filter LH=Yes; Filter RH=No; Height=18"; Induct Center C=9"; Induct Center D=20"; Induct Filter D=33 3/4"; Induction D=33"; Inlet Left=No; Inlet Right=Yes; Length=40"; Model=ESTS/DOAS; Radius=3 15/16"; Row F=8"; Second Pipe H=4 1/8"; URL=https://www.anemostat-hvac.com; Width=40"
- ESTS/DOAS 1/2-hp - 08R W/4ROW NO Filter: Connect H=1 7/16"; Connect Length=4 1/2"; Connector for 6ROW LS=No; Connector for 6ROW RS=No; Description=DOAS SERIES FAN POWERED AIR TERMINAL; Diameter=7 7/8"; Discharge Height "Y"=12"; Discharge Width "X"=14"; Duct Inlet=4"; Filter LH=No; Filter RH=No; Height=18"; Induct Center C=9"; Induct Center D=20"; Induct Filter D=33 3/4"; Induction D=33"; Inlet Left=No; Inlet Right=Yes; Length=40"; Model=ESTS/DOAS; Radius=3 15/16"; Row F=6"; Second Pipe H=2 1/8"; URL=https://www.anemostat-hvac.com; Width=40"
- ESTS/DOAS 1/2-hp - 08R W/6ROW NO Filter: Connect H=1 7/16"; Connect Length=4 1/2"; Connector for 6ROW LS=No; Connector for 6ROW RS=No; Description=DOAS SERIES FAN POWERED AIR TERMINAL; Diameter=7 7/8"; Discharge Height "Y"=12"; Discharge Width "X"=14"; Duct Inlet=4"; Filter LH=No; Filter RH=No; Height=18"; Induct Center C=9"; Induct Center D=20"; Induct Filter D=33 3/4"; Induction D=33"; Inlet Left=No; Inlet Right=Yes; Length=40"; Model=ESTS/DOAS; Radius=3 15/16"; Row F=8"; Second Pipe H=4 1/8"; URL=https://www.anemostat-hvac.com; Width=40"
- ESTS/DOAS 1/2-hp - 09L W/4ROW & Filter: Connect H=1 7/16"; Connect Length=4 1/2"; Connector for 6ROW LS=No; Connector for 6ROW RS=No; Description=DOAS SERIES FAN POWERED AIR TERMINAL; Diameter=8 7/8"; Discharge Height "Y"=12"; Discharge Width "X"=14"; Duct Inlet=4"; Filter LH=No; Filter RH=Yes; Height=18"; Induct Center C=9"; Induct Center D=20"; Induct Filter D=33 3/4"; Induction D=33"; Inlet Left=Yes; Inlet Right=No; Length=40"; Model=ESTS/DOAS; Radius=4 7/16"; Row F=6"; Second Pipe H=2 1/8"; URL=https://www.anemostat-hvac.com; Width=40"
- ESTS/DOAS 1/2-hp - 09L W/6ROW & Filter: Connect H=1 7/16"; Connect Length=4 1/2"; Connector for 6ROW LS=No; Connector for 6ROW RS=Yes; Description=DOAS SERIES FAN POWERED AIR TERMINAL; Diameter=8 7/8"; Discharge Height "Y"=12"; Discharge Width "X"=14"; Duct Inlet=4"; Filter LH=No; Filter RH=Yes; Height=18"; Induct Center C=9"; Induct Center D=20"; Induct Filter D=33 3/4"; Induction D=33"; Inlet Left=Yes; Inlet Right=No; Length=40"; Model=ESTS/DOAS; Radius=4 7/16"; Row F=8"; Second Pipe H=4 1/8"; URL=https://www.anemostat-hvac.com; Width=40"
- ESTS/DOAS 1/2-hp - 09L W/4ROW NO Filter: Connect H=1 7/16"; Connect Length=4 1/2"; Connector for 6ROW LS=No; Connector for 6ROW RS=No; Description=DOAS SERIES FAN POWERED AIR TERMINAL; Diameter=8 7/8"; Discharge Height "Y"=12"; Discharge Width "X"=14"; Duct Inlet=4"; Filter LH=No; Filter RH=No; Height=18"; Induct Center C=9"; Induct Center D=20"; Induct Filter D=33 3/4"; Induction D=33"; Inlet Left=Yes; Inlet Right=No; Length=40"; Model=ESTS/DOAS; Radius=4 7/16"; Row F=6"; Second Pipe H=2 1/8"; URL=https://www.anemostat-hvac.com; Width=40"
- ESTS/DOAS 1/2-hp - 09L W/6ROW NO Filter: Connect H=1 7/16"; Connect Length=4 1/2"; Connector for 6ROW LS=No; Connector for 6ROW RS=Yes; Description=DOAS SERIES FAN POWERED AIR TERMINAL; Diameter=8 7/8"; Discharge Height "Y"=12"; Discharge Width "X"=14"; Duct Inlet=4"; Filter LH=No; Filter RH=No; Height=18"; Induct Center C=9"; Induct Center D=20"; Induct Filter D=33 3/4"; Induction D=33"; Inlet Left=Yes; Inlet Right=No; Length=40"; Model=ESTS/DOAS; Radius=4 7/16"; Row F=8"; Second Pipe H=4 1/8"; URL=https://www.anemostat-hvac.com; Width=40"
- ESTS/DOAS 1/2-hp - 09R W/4ROW & Filter: Connect H=1 7/16"; Connect Length=4 1/2"; Connector for 6ROW LS=No; Connector for 6ROW RS=No; Description=DOAS SERIES FAN POWERED AIR TERMINAL; Diameter=8 7/8"; Discharge Height "Y"=12"; Discharge Width "X"=14"; Duct Inlet=4"; Filter LH=Yes; Filter RH=No; Height=18"; Induct Center C=9"; Induct Center D=20"; Induct Filter D=33 3/4"; Induction D=33"; Inlet Left=No; Inlet Right=Yes; Length=40"; Model=ESTS/DOAS; Radius=4 7/16"; Row F=6"; Second Pipe H=2 1/8"; URL=https://www.anemostat-hvac.com; Width=40"
- ESTS/DOAS 1/2-hp - 09R W/6ROW & Filter: Connect H=1 7/16"; Connect Length=4 1/2"; Connector for 6ROW LS=Yes; Connector for 6ROW RS=No; Description=DOAS SERIES FAN POWERED AIR TERMINAL; Diameter=8 7/8"; Discharge Height "Y"=12"; Discharge Width "X"=14"; Duct Inlet=4"; Filter LH=Yes; Filter RH=No; Height=18"; Induct Center C=9"; Induct Center D=20"; Induct Filter D=33 3/4"; Induction D=33"; Inlet Left=No; Inlet Right=Yes; Length=40"; Model=ESTS/DOAS; Radius=4 7/16"; Row F=8"; Second Pipe H=4 1/8"; URL=https://www.anemostat-hvac.com; Width=40"
- ESTS/DOAS 1/2-hp - 09R W/4ROW NO Filter: Connect H=1 7/16"; Connect Length=4 1/2"; Connector for 6ROW LS=No; Connector for 6ROW RS=No; Description=DOAS SERIES FAN POWERED AIR TERMINAL; Diameter=8 7/8"; Discharge Height "Y"=12"; Discharge Width "X"=14"; Duct Inlet=4"; Filter LH=No; Filter RH=No; Height=18"; Induct Center C=9"; Induct Center D=20"; Induct Filter D=33 3/4"; Induction D=33"; Inlet Left=No; Inlet Right=Yes; Length=40"; Model=ESTS/DOAS; Radius=4 7/16"; Row F=6"; Second Pipe H=2 1/8"; URL=https://www.anemostat-hvac.com; Width=40"
- ESTS/DOAS 1/2-hp - 09R W/6ROW NO Filter: Connect H=1 7/16"; Connect Length=4 1/2"; Connector for 6ROW LS=Yes; Connector for 6ROW RS=No; Description=DOAS SERIES FAN POWERED AIR TERMINAL; Diameter=8 7/8"; Discharge Height "Y"=12"; Discharge Width "X"=14"; Duct Inlet=4"; Filter LH=No; Filter RH=No; Height=18"; Induct Center C=9"; Induct Center D=20"; Induct Filter D=33 3/4"; Induction D=33"; Inlet Left=No; Inlet Right=Yes; Length=40"; Model=ESTS/DOAS; Radius=4 7/16"; Row F=8"; Second Pipe H=4 1/8"; URL=https://www.anemostat-hvac.com; Width=40"
- ESTS/DOAS 1/2-hp - 10L W/4ROW & Filter: Connect H=1 7/16"; Connect Length=4 1/2"; Connector for 6ROW LS=No; Connector for 6ROW RS=No; Description=DOAS SERIES FAN POWERED AIR TERMINAL; Diameter=9 7/8"; Discharge Height "Y"=12"; Discharge Width "X"=14"; Duct Inlet=5"; Filter LH=No; Filter RH=Yes; Height=18"; Induct Center C=9"; Induct Center D=20"; Induct Filter D=33 3/4"; Induction D=33"; Inlet Left=Yes; Inlet Right=No; Length=40"; Model=ESTS/DOAS; Radius=4 15/16"; Row F=6"; Second Pipe H=2 1/8"; URL=https://www.anemostat-hvac.com; Width=40"
- ESTS/DOAS 1/2-hp - 10L W/6ROW & Filter: Connect H=1 7/16"; Connect Length=4 1/2"; Connector for 6ROW LS=No; Connector for 6ROW RS=Yes; Description=DOAS SERIES FAN POWERED AIR TERMINAL; Diameter=9 7/8"; Discharge Height "Y"=12"; Discharge Width "X"=14"; Duct Inlet=5"; Filter LH=No; Filter RH=Yes; Height=18"; Induct Center C=9"; Induct Center D=20"; Induct Filter D=33 3/4"; Induction D=33"; Inlet Left=Yes; Inlet Right=No; Length=40"; Model=ESTS/DOAS; Radius=4 15/16"; Row F=8"; Second Pipe H=4 1/8"; URL=https://www.anemostat-hvac.com; Width=40"
- ESTS/DOAS 1/2-hp - 10L W/4ROW NO Filter: Connect H=1 7/16"; Connect Length=4 1/2"; Connector for 6ROW LS=No; Connector for 6ROW RS=No; Description=DOAS SERIES FAN POWERED AIR TERMINAL; Diameter=9 7/8"; Discharge Height "Y"=12"; Discharge Width "X"=14"; Duct Inlet=5"; Filter LH=No; Filter RH=No; Height=18"; Induct Center C=9"; Induct Center D=20"; Induct Filter D=33 3/4"; Induction D=33"; Inlet Left=Yes; Inlet Right=No; Length=40"; Model=ESTS/DOAS; Radius=4 15/16"; Row F=6"; Second Pipe H=2 1/8"; URL=https://www.anemostat-hvac.com; Width=40"
- ESTS/DOAS 1/2-hp - 10L W/6ROW NO Filter: Connect H=1 7/16"; Connect Length=4 1/2"; Connector for 6ROW LS=No; Connector for 6ROW RS=Yes; Description=DOAS SERIES FAN POWERED AIR TERMINAL; Diameter=9 7/8"; Discharge Height "Y"=12"; Discharge Width "X"=14"; Duct Inlet=5"; Filter LH=No; Filter RH=No; Height=18"; Induct Center C=9"; Induct Center D=20"; Induct Filter D=33 3/4"; Induction D=33"; Inlet Left=Yes; Inlet Right=No; Length=40"; Model=ESTS/DOAS; Radius=4 15/16"; Row F=8"; Second Pipe H=4 1/8"; URL=https://www.anemostat-hvac.com; Width=40"
- ESTS/DOAS 1/2-hp - 10R W/4ROW & Filter: Connect H=1 7/16"; Connect Length=4 1/2"; Connector for 6ROW LS=No; Connector for 6ROW RS=No; Description=DOAS SERIES FAN POWERED AIR TERMINAL; Diameter=9 7/8"; Discharge Height "Y"=12"; Discharge Width "X"=14"; Duct Inlet=5"; Filter LH=Yes; Filter RH=No; Height=18"; Induct Center C=9"; Induct Center D=20"; Induct Filter D=33 3/4"; Induction D=33"; Inlet Left=No; Inlet Right=Yes; Length=40"; Model=ESTS/DOAS; Radius=4 15/16"; Row F=6"; Second Pipe H=2 1/8"; URL=https://www.anemostat-hvac.com; Width=40"
- ESTS/DOAS 1/2-hp - 10R W/6ROW & Filter: Connect H=1 7/16"; Connect Length=4 1/2"; Connector for 6ROW LS=Yes; Connector for 6ROW RS=No; Description=DOAS SERIES FAN POWERED AIR TERMINAL; Diameter=9 7/8"; Discharge Height "Y"=12"; Discharge Width "X"=14"; Duct Inlet=5"; Filter LH=Yes; Filter RH=No; Height=18"; Induct Center C=9"; Induct Center D=20"; Induct Filter D=33 3/4"; Induction D=33"; Inlet Left=No; Inlet Right=Yes; Length=40"; Model=ESTS/DOAS; Radius=4 15/16"; Row F=8"; Second Pipe H=4 1/8"; URL=https://www.anemostat-hvac.com; Width=40"
- ESTS/DOAS 1/2-hp - 10R W/4ROW NO Filter: Connect H=1 7/16"; Connect Length=4 1/2"; Connector for 6ROW LS=No; Connector for 6ROW RS=No; Description=DOAS SERIES FAN POWERED AIR TERMINAL; Diameter=9 7/8"; Discharge Height "Y"=12"; Discharge Width "X"=14"; Duct Inlet=5"; Filter LH=No; Filter RH=No; Height=18"; Induct Center C=9"; Induct Center D=20"; Induct Filter D=33 3/4"; Induction D=33"; Inlet Left=No; Inlet Right=Yes; Length=40"; Model=ESTS/DOAS; Radius=4 15/16"; Row F=6"; Second Pipe H=2 1/8"; URL=https://www.anemostat-hvac.com; Width=40"
- ESTS/DOAS 1/2-hp - 10R W/6ROW NO Filter: Connect H=1 7/16"; Connect Length=4 1/2"; Connector for 6ROW LS=Yes; Connector for 6ROW RS=No; Description=DOAS SERIES FAN POWERED AIR TERMINAL; Diameter=9 7/8"; Discharge Height "Y"=12"; Discharge Width "X"=14"; Duct Inlet=5"; Filter LH=No; Filter RH=No; Height=18"; Induct Center C=9"; Induct Center D=20"; Induct Filter D=33 3/4"; Induction D=33"; Inlet Left=No; Inlet Right=Yes; Length=40"; Model=ESTS/DOAS; Radius=4 15/16"; Row F=8"; Second Pipe H=4 1/8"; URL=https://www.anemostat-hvac.com; Width=40"
- ESTS/DOAS 1/2-hp - 12L W/4ROW & Filter: Connect H=1 7/16"; Connect Length=4 1/2"; Connector for 6ROW LS=No; Connector for 6ROW RS=No; Description=DOAS SERIES FAN POWERED AIR TERMINAL; Diameter=11 7/8"; Discharge Height "Y"=12"; Discharge Width "X"=14"; Duct Inlet=6"; Filter LH=No; Filter RH=Yes; Height=18"; Induct Center C=9"; Induct Center D=20"; Induct Filter D=33 3/4"; Induction D=33"; Inlet Left=Yes; Inlet Right=No; Length=40"; Model=ESTS/DOAS; Radius=5 15/16"; Row F=6"; Second Pipe H=2 1/8"; URL=https://www.anemostat-hvac.com; Width=40"
- ESTS/DOAS 1/2-hp - 12L W/6ROW & Filter: Connect H=1 7/16"; Connect Length=4 1/2"; Connector for 6ROW LS=No; Connector for 6ROW RS=Yes; Description=DOAS SERIES FAN POWERED AIR TERMINAL; Diameter=11 7/8"; Discharge Height "Y"=12"; Discharge Width "X"=14"; Duct Inlet=6"; Filter LH=No; Filter RH=Yes; Height=18"; Induct Center C=9"; Induct Center D=20"; Induct Filter D=33 3/4"; Induction D=33"; Inlet Left=Yes; Inlet Right=No; Length=40"; Model=ESTS/DOAS; Radius=5 15/16"; Row F=8"; Second Pipe H=4 1/8"; URL=https://www.anemostat-hvac.com; Width=40"
- ESTS/DOAS 1/2-hp - 12L W/4ROW NO Filter: Connect H=1 7/16"; Connect Length=4 1/2"; Connector for 6ROW LS=No; Connector for 6ROW RS=No; Description=DOAS SERIES FAN POWERED AIR TERMINAL; Diameter=11 7/8"; Discharge Height "Y"=12"; Discharge Width "X"=14"; Duct Inlet=6"; Filter LH=No; Filter RH=No; Height=18"; Induct Center C=9"; Induct Center D=20"; Induct Filter D=33 3/4"; Induction D=33"; Inlet Left=Yes; Inlet Right=No; Length=40"; Model=ESTS/DOAS; Radius=5 15/16"; Row F=6"; Second Pipe H=2 1/8"; URL=https://www.anemostat-hvac.com; Width=40"
- ESTS/DOAS 1/2-hp - 12L W/6ROW NO Filter: Connect H=1 7/16"; Connect Length=4 1/2"; Connector for 6ROW LS=No; Connector for 6ROW RS=Yes; Description=DOAS SERIES FAN POWERED AIR TERMINAL; Diameter=11 7/8"; Discharge Height "Y"=12"; Discharge Width "X"=14"; Duct Inlet=6"; Filter LH=No; Filter RH=No; Height=18"; Induct Center C=9"; Induct Center D=20"; Induct Filter D=33 3/4"; Induction D=33"; Inlet Left=Yes; Inlet Right=No; Length=40"; Model=ESTS/DOAS; Radius=5 15/16"; Row F=8"; Second Pipe H=4 1/8"; URL=https://www.anemostat-hvac.com; Width=40"
- ESTS/DOAS 1/2-hp - 12R W/4ROW & Filter: Connect H=1 7/16"; Connect Length=4 1/2"; Connector for 6ROW LS=No; Connector for 6ROW RS=No; Description=DOAS SERIES FAN POWERED AIR TERMINAL; Diameter=11 7/8"; Discharge Height "Y"=12"; Discharge Width "X"=14"; Duct Inlet=6"; Filter LH=Yes; Filter RH=No; Height=18"; Induct Center C=9"; Induct Center D=20"; Induct Filter D=33 3/4"; Induction D=33"; Inlet Left=No; Inlet Right=Yes; Length=40"; Model=ESTS/DOAS; Radius=5 15/16"; Row F=6"; Second Pipe H=2 1/8"; URL=https://www.anemostat-hvac.com; Width=40"
- ESTS/DOAS 1/2-hp - 12R W/6ROW & Filter: Connect H=1 7/16"; Connect Length=4 1/2"; Connector for 6ROW LS=Yes; Connector for 6ROW RS=No; Description=DOAS SERIES FAN POWERED AIR TERMINAL; Diameter=11 7/8"; Discharge Height "Y"=12"; Discharge Width "X"=14"; Duct Inlet=6"; Filter LH=Yes; Filter RH=No; Height=18"; Induct Center C=9"; Induct Center D=20"; Induct Filter D=33 3/4"; Induction D=33"; Inlet Left=No; Inlet Right=Yes; Length=40"; Model=ESTS/DOAS; Radius=5 15/16"; Row F=8"; Second Pipe H=4 1/8"; URL=https://www.anemostat-hvac.com; Width=40"
- ESTS/DOAS 1/2-hp - 12R W/4ROW NO Filter: Connect H=1 7/16"; Connect Length=4 1/2"; Connector for 6ROW LS=No; Connector for 6ROW RS=No; Description=DOAS SERIES FAN POWERED AIR TERMINAL; Diameter=11 7/8"; Discharge Height "Y"=12"; Discharge Width "X"=14"; Duct Inlet=6"; Filter LH=No; Filter RH=No; Height=18"; Induct Center C=9"; Induct Center D=20"; Induct Filter D=33 3/4"; Induction D=33"; Inlet Left=No; Inlet Right=Yes; Length=40"; Model=ESTS/DOAS; Radius=5 15/16"; Row F=6"; Second Pipe H=2 1/8"; URL=https://www.anemostat-hvac.com; Width=40"
- ESTS/DOAS 1/2-hp - 12R W/6ROW NO Filter: Connect H=1 7/16"; Connect Length=4 1/2"; Connector for 6ROW LS=Yes; Connector for 6ROW RS=No; Description=DOAS SERIES FAN POWERED AIR TERMINAL; Diameter=11 7/8"; Discharge Height "Y"=12"; Discharge Width "X"=14"; Duct Inlet=6"; Filter LH=No; Filter RH=No; Height=18"; Induct Center C=9"; Induct Center D=20"; Induct Filter D=33 3/4"; Induction D=33"; Inlet Left=No; Inlet Right=Yes; Length=40"; Model=ESTS/DOAS; Radius=5 15/16"; Row F=8"; Second Pipe H=4 1/8"; URL=https://www.anemostat-hvac.com; Width=40"
- ESTS/DOAS 1/2-hp - 14L W/4ROW & Filter: Connect H=1 7/16"; Connect Length=4 1/2"; Connector for 6ROW LS=No; Connector for 6ROW RS=No; Description=DOAS SERIES FAN POWERED AIR TERMINAL; Diameter=13 7/8"; Discharge Height "Y"=12"; Discharge Width "X"=14"; Duct Inlet=7"; Filter LH=No; Filter RH=Yes; Height=18"; Induct Center C=9"; Induct Center D=20"; Induct Filter D=33 3/4"; Induction D=33"; Inlet Left=Yes; Inlet Right=No; Length=40"; Model=ESTS/DOAS; Radius=6 15/16"; Row F=6"; Second Pipe H=2 1/8"; URL=https://www.anemostat-hvac.com; Width=40"
- ESTS/DOAS 1/2-hp - 14L W/6ROW & Filter: Connect H=1 7/16"; Connect Length=4 1/2"; Connector for 6ROW LS=No; Connector for 6ROW RS=Yes; Description=DOAS SERIES FAN POWERED AIR TERMINAL; Diameter=13 7/8"; Discharge Height "Y"=12"; Discharge Width "X"=14"; Duct Inlet=7"; Filter LH=No; Filter RH=Yes; Height=18"; Induct Center C=9"; Induct Center D=20"; Induct Filter D=33 3/4"; Induction D=33"; Inlet Left=Yes; Inlet Right=No; Length=40"; Model=ESTS/DOAS; Radius=6 15/16"; Row F=8"; Second Pipe H=4 1/8"; URL=https://www.anemostat-hvac.com; Width=40"
- ESTS/DOAS 1/2-hp - 14L W/4ROW NO Filter: Connect H=1 7/16"; Connect Length=4 1/2"; Connector for 6ROW LS=No; Connector for 6ROW RS=No; Description=DOAS SERIES FAN POWERED AIR TERMINAL; Diameter=13 7/8"; Discharge Height "Y"=12"; Discharge Width "X"=14"; Duct Inlet=7"; Filter LH=No; Filter RH=No; Height=18"; Induct Center C=9"; Induct Center D=20"; Induct Filter D=33 3/4"; Induction D=33"; Inlet Left=Yes; Inlet Right=No; Length=40"; Model=ESTS/DOAS; Radius=6 15/16"; Row F=6"; Second Pipe H=2 1/8"; URL=https://www.anemostat-hvac.com; Width=40"
- ESTS/DOAS 1/2-hp - 14L W/6ROW NO Filter: Connect H=1 7/16"; Connect Length=4 1/2"; Connector for 6ROW LS=No; Connector for 6ROW RS=Yes; Description=DOAS SERIES FAN POWERED AIR TERMINAL; Diameter=13 7/8"; Discharge Height "Y"=12"; Discharge Width "X"=14"; Duct Inlet=7"; Filter LH=No; Filter RH=No; Height=18"; Induct Center C=9"; Induct Center D=20"; Induct Filter D=33 3/4"; Induction D=33"; Inlet Left=Yes; Inlet Right=No; Length=40"; Model=ESTS/DOAS; Radius=6 15/16"; Row F=8"; Second Pipe H=4 1/8"; URL=https://www.anemostat-hvac.com; Width=40"
- ESTS/DOAS 1/2-hp - 14R W/4ROW & Filter: Connect H=1 7/16"; Connect Length=4 1/2"; Connector for 6ROW LS=No; Connector for 6ROW RS=No; Description=DOAS SERIES FAN POWERED AIR TERMINAL; Diameter=13 7/8"; Discharge Height "Y"=12"; Discharge Width "X"=14"; Duct Inlet=7"; Filter LH=Yes; Filter RH=No; Height=18"; Induct Center C=9"; Induct Center D=20"; Induct Filter D=33 3/4"; Induction D=33"; Inlet Left=No; Inlet Right=Yes; Length=40"; Model=ESTS/DOAS; Radius=6 15/16"; Row F=6"; Second Pipe H=2 1/8"; URL=https://www.anemostat-hvac.com; Width=40"
- ESTS/DOAS 1/2-hp - 14R W/6ROW & Filter: Connect H=1 7/16"; Connect Length=4 1/2"; Connector for 6ROW LS=Yes; Connector for 6ROW RS=No; Description=DOAS SERIES FAN POWERED AIR TERMINAL; Diameter=13 7/8"; Discharge Height "Y"=12"; Discharge Width "X"=14"; Duct Inlet=7"; Filter LH=Yes; Filter RH=No; Height=18"; Induct Center C=9"; Induct Center D=20"; Induct Filter D=33 3/4"; Induction D=33"; Inlet Left=No; Inlet Right=Yes; Length=40"; Model=ESTS/DOAS; Radius=6 15/16"; Row F=8"; Second Pipe H=4 1/8"; URL=https://www.anemostat-hvac.com; Width=40"
- ESTS/DOAS 1/2-hp - 14R W/4ROW NO Filter: Connect H=1 7/16"; Connect Length=4 1/2"; Connector for 6ROW LS=No; Connector for 6ROW RS=No; Description=DOAS SERIES FAN POWERED AIR TERMINAL; Diameter=13 7/8"; Discharge Height "Y"=12"; Discharge Width "X"=14"; Duct Inlet=7"; Filter LH=No; Filter RH=No; Height=18"; Induct Center C=9"; Induct Center D=20"; Induct Filter D=33 3/4"; Induction D=33"; Inlet Left=No; Inlet Right=Yes; Length=40"; Model=ESTS/DOAS; Radius=6 15/16"; Row F=6"; Second Pipe H=2 1/8"; URL=https://www.anemostat-hvac.com; Width=40"
- ESTS/DOAS 1/2-hp - 14R W/6ROW NO Filter: Connect H=1 7/16"; Connect Length=4 1/2"; Connector for 6ROW LS=Yes; Connector for 6ROW RS=No; Description=DOAS SERIES FAN POWERED AIR TERMINAL; Diameter=13 7/8"; Discharge Height "Y"=12"; Discharge Width "X"=14"; Duct Inlet=7"; Filter LH=No; Filter RH=No; Height=18"; Induct Center C=9"; Induct Center D=20"; Induct Filter D=33 3/4"; Induction D=33"; Inlet Left=No; Inlet Right=Yes; Length=40"; Model=ESTS/DOAS; Radius=6 15/16"; Row F=8"; Second Pipe H=4 1/8"; URL=https://www.anemostat-hvac.com; Width=40"
- ESTS/DOAS 1/3-hp - 05L W/4ROW & Filter: Connect H=1 7/16"; Connect Length=4 1/2"; Connector for 6ROW LS=No; Connector for 6ROW RS=No; Description=DOAS SERIES FAN POWERED AIR TERMINAL; Diameter=4 7/8"; Discharge Height "Y"=11"; Discharge Width "X"=11 1/2"; Duct Inlet=2"; Filter LH=No; Filter RH=Yes; Height=18"; Induct Center C=9"; Induct Center D=18"; Induct Filter D=29 3/4"; Induction D=29"; Inlet Left=Yes; Inlet Right=No; Length=36"; Model=ESTS/DOAS; Radius=2 7/16"; Row F=6"; Second Pipe H=2 1/8"; URL=https://www.anemostat-hvac.com; Width=32"
- ESTS/DOAS 1/3-hp - 05L W/6ROW & Filter: Connect H=1 7/16"; Connect Length=4 1/2"; Connector for 6ROW LS=No; Connector for 6ROW RS=Yes; Description=DOAS SERIES FAN POWERED AIR TERMINAL; Diameter=4 7/8"; Discharge Height "Y"=11"; Discharge Width "X"=11 1/2"; Duct Inlet=2"; Filter LH=No; Filter RH=Yes; Height=18"; Induct Center C=9"; Induct Center D=18"; Induct Filter D=29 3/4"; Induction D=29"; Inlet Left=Yes; Inlet Right=No; Length=36"; Model=ESTS/DOAS; Radius=2 7/16"; Row F=8"; Second Pipe H=4 1/8"; URL=https://www.anemostat-hvac.com; Width=32"
- ESTS/DOAS 1/3-hp - 05L W/4ROW NO Filter: Connect H=1 7/16"; Connect Length=4 1/2"; Connector for 6ROW LS=No; Connector for 6ROW RS=No; Description=DOAS SERIES FAN POWERED AIR TERMINAL; Diameter=4 7/8"; Discharge Height "Y"=11"; Discharge Width "X"=11 1/2"; Duct Inlet=2"; Filter LH=No; Filter RH=No; Height=18"; Induct Center C=9"; Induct Center D=18"; Induct Filter D=29 3/4"; Induction D=29"; Inlet Left=Yes; Inlet Right=No; Length=36"; Model=ESTS/DOAS; Radius=2 7/16"; Row F=6"; Second Pipe H=2 1/8"; URL=https://www.anemostat-hvac.com; Width=32"
- ESTS/DOAS 1/3-hp - 05L W/6ROW NO Filter: Connect H=1 7/16"; Connect Length=4 1/2"; Connector for 6ROW LS=No; Connector for 6ROW RS=Yes; Description=DOAS SERIES FAN POWERED AIR TERMINAL; Diameter=4 7/8"; Discharge Height "Y"=11"; Discharge Width "X"=11 1/2"; Duct Inlet=2"; Filter LH=No; Filter RH=No; Height=18"; Induct Center C=9"; Induct Center D=18"; Induct Filter D=29 3/4"; Induction D=29"; Inlet Left=Yes; Inlet Right=No; Length=36"; Model=ESTS/DOAS; Radius=2 7/16"; Row F=8"; Second Pipe H=4 1/8"; URL=https://www.anemostat-hvac.com; Width=32"
- ESTS/DOAS 1/3-hp - 05R W/4ROW & Filter: Connect H=1 7/16"; Connect Length=4 1/2"; Connector for 6ROW LS=No; Connector for 6ROW RS=No; Description=DOAS SERIES FAN POWERED AIR TERMINAL; Diameter=4 7/8"; Discharge Height "Y"=11"; Discharge Width "X"=11 1/2"; Duct Inlet=2"; Filter LH=Yes; Filter RH=No; Height=18"; Induct Center C=9"; Induct Center D=18"; Induct Filter D=29 3/4"; Induction D=29"; Inlet Left=No; Inlet Right=Yes; Length=36"; Model=ESTS/DOAS; Radius=2 7/16"; Row F=6"; Second Pipe H=2 1/8"; URL=https://www.anemostat-hvac.com; Width=32"
- ESTS/DOAS 1/3-hp - 05R W/6ROW & Filter: Connect H=1 7/16"; Connect Length=4 1/2"; Connector for 6ROW LS=Yes; Connector for 6ROW RS=No; Description=DOAS SERIES FAN POWERED AIR TERMINAL; Diameter=4 7/8"; Discharge Height "Y"=11"; Discharge Width "X"=11 1/2"; Duct Inlet=2"; Filter LH=Yes; Filter RH=No; Height=18"; Induct Center C=9"; Induct Center D=18"; Induct Filter D=29 3/4"; Induction D=29"; Inlet Left=No; Inlet Right=Yes; Length=36"; Model=ESTS/DOAS; Radius=2 7/16"; Row F=8"; Second Pipe H=4 1/8"; URL=https://www.anemostat-hvac.com; Width=32"
- ESTS/DOAS 1/3-hp - 05R W/4ROW NO Filter: Connect H=1 7/16"; Connect Length=4 1/2"; Connector for 6ROW LS=No; Connector for 6ROW RS=No; Description=DOAS SERIES FAN POWERED AIR TERMINAL; Diameter=4 7/8"; Discharge Height "Y"=11"; Discharge Width "X"=11 1/2"; Duct Inlet=2"; Filter LH=No; Filter RH=No; Height=18"; Induct Center C=9"; Induct Center D=18"; Induct Filter D=29 3/4"; Induction D=29"; Inlet Left=No; Inlet Right=Yes; Length=36"; Model=ESTS/DOAS; Radius=2 7/16"; Row F=6"; Second Pipe H=2 1/8"; URL=https://www.anemostat-hvac.com; Width=32"
- ESTS/DOAS 1/3-hp - 05R W/6ROW NO Filter: Connect H=1 7/16"; Connect Length=4 1/2"; Connector for 6ROW LS=Yes; Connector for 6ROW RS=No; Description=DOAS SERIES FAN POWERED AIR TERMINAL; Diameter=4 7/8"; Discharge Height "Y"=11"; Discharge Width "X"=11 1/2"; Duct Inlet=2"; Filter LH=No; Filter RH=No; Height=18"; Induct Center C=9"; Induct Center D=18"; Induct Filter D=29 3/4"; Induction D=29"; Inlet Left=No; Inlet Right=Yes; Length=36"; Model=ESTS/DOAS; Radius=2 7/16"; Row F=8"; Second Pipe H=4 1/8"; URL=https://www.anemostat-hvac.com; Width=32"
- ESTS/DOAS 1/3-hp - 06L W/4ROW & Filter: Connect H=1 7/16"; Connect Length=4 1/2"; Connector for 6ROW LS=No; Connector for 6ROW RS=No; Description=DOAS SERIES FAN POWERED AIR TERMINAL; Diameter=5 7/8"; Discharge Height "Y"=11"; Discharge Width "X"=11 1/2"; Duct Inlet=3"; Filter LH=No; Filter RH=Yes; Height=18"; Induct Center C=9"; Induct Center D=18"; Induct Filter D=29 3/4"; Induction D=29"; Inlet Left=Yes; Inlet Right=No; Length=36"; Model=ESTS/DOAS; Radius=2 15/16"; Row F=6"; Second Pipe H=2 1/8"; URL=https://www.anemostat-hvac.com; Width=32"
- ESTS/DOAS 1/3-hp - 06L W/6ROW & Filter: Connect H=1 7/16"; Connect Length=4 1/2"; Connector for 6ROW LS=No; Connector for 6ROW RS=Yes; Description=DOAS SERIES FAN POWERED AIR TERMINAL; Diameter=5 7/8"; Discharge Height "Y"=11"; Discharge Width "X"=11 1/2"; Duct Inlet=3"; Filter LH=No; Filter RH=Yes; Height=18"; Induct Center C=9"; Induct Center D=18"; Induct Filter D=29 3/4"; Induction D=29"; Inlet Left=Yes; Inlet Right=No; Length=36"; Model=ESTS/DOAS; Radius=2 15/16"; Row F=8"; Second Pipe H=4 1/8"; URL=https://www.anemostat-hvac.com; Width=32"
- ESTS/DOAS 1/3-hp - 06L W/4ROW NO Filter: Connect H=1 7/16"; Connect Length=4 1/2"; Connector for 6ROW LS=No; Connector for 6ROW RS=No; Description=DOAS SERIES FAN POWERED AIR TERMINAL; Diameter=5 7/8"; Discharge Height "Y"=11"; Discharge Width "X"=11 1/2"; Duct Inlet=3"; Filter LH=No; Filter RH=No; Height=18"; Induct Center C=9"; Induct Center D=18"; Induct Filter D=29 3/4"; Induction D=29"; Inlet Left=Yes; Inlet Right=No; Length=36"; Model=ESTS/DOAS; Radius=2 15/16"; Row F=6"; Second Pipe H=2 1/8"; URL=https://www.anemostat-hvac.com; Width=32"
- ESTS/DOAS 1/3-hp - 06L W/6ROW NO Filter: Connect H=1 7/16"; Connect Length=4 1/2"; Connector for 6ROW LS=No; Connector for 6ROW RS=Yes; Description=DOAS SERIES FAN POWERED AIR TERMINAL; Diameter=5 7/8"; Discharge Height "Y"=11"; Discharge Width "X"=11 1/2"; Duct Inlet=3"; Filter LH=No; Filter RH=No; Height=18"; Induct Center C=9"; Induct Center D=18"; Induct Filter D=29 3/4"; Induction D=29"; Inlet Left=Yes; Inlet Right=No; Length=36"; Model=ESTS/DOAS; Radius=2 15/16"; Row F=8"; Second Pipe H=4 1/8"; URL=https://www.anemostat-hvac.com; Width=32"
- ESTS/DOAS 1/3-hp - 06R W/4ROW & Filter: Connect H=1 7/16"; Connect Length=4 1/2"; Connector for 6ROW LS=No; Connector for 6ROW RS=No; Description=DOAS SERIES FAN POWERED AIR TERMINAL; Diameter=5 7/8"; Discharge Height "Y"=11"; Discharge Width "X"=11 1/2"; Duct Inlet=3"; Filter LH=Yes; Filter RH=No; Height=18"; Induct Center C=9"; Induct Center D=18"; Induct Filter D=29 3/4"; Induction D=29"; Inlet Left=No; Inlet Right=Yes; Length=36"; Model=ESTS/DOAS; Radius=2 15/16"; Row F=6"; Second Pipe H=2 1/8"; URL=https://www.anemostat-hvac.com; Width=32"
- ESTS/DOAS 1/3-hp - 06R W/6ROW & Filter: Connect H=1 7/16"; Connect Length=4 1/2"; Connector for 6ROW LS=Yes; Connector for 6ROW RS=No; Description=DOAS SERIES FAN POWERED AIR TERMINAL; Diameter=5 7/8"; Discharge Height "Y"=11"; Discharge Width "X"=11 1/2"; Duct Inlet=3"; Filter LH=Yes; Filter RH=No; Height=18"; Induct Center C=9"; Induct Center D=18"; Induct Filter D=29 3/4"; Induction D=29"; Inlet Left=No; Inlet Right=Yes; Length=36"; Model=ESTS/DOAS; Radius=2 15/16"; Row F=8"; Second Pipe H=4 1/8"; URL=https://www.anemostat-hvac.com; Width=32"
- ESTS/DOAS 1/3-hp - 06R W/4ROW NO Filter: Connect H=1 7/16"; Connect Length=4 1/2"; Connector for 6ROW LS=No; Connector for 6ROW RS=No; Description=DOAS SERIES FAN POWERED AIR TERMINAL; Diameter=5 7/8"; Discharge Height "Y"=11"; Discharge Width "X"=11 1/2"; Duct Inlet=3"; Filter LH=No; Filter RH=No; Height=18"; Induct Center C=9"; Induct Center D=18"; Induct Filter D=29 3/4"; Induction D=29"; Inlet Left=No; Inlet Right=Yes; Length=36"; Model=ESTS/DOAS; Radius=2 15/16"; Row F=6"; Second Pipe H=2 1/8"; URL=https://www.anemostat-hvac.com; Width=32"
- ESTS/DOAS 1/3-hp - 06R W/6ROW NO Filter: Connect H=1 7/16"; Connect Length=4 1/2"; Connector for 6ROW LS=Yes; Connector for 6ROW RS=No; Description=DOAS SERIES FAN POWERED AIR TERMINAL; Diameter=5 7/8"; Discharge Height "Y"=11"; Discharge Width "X"=11 1/2"; Duct Inlet=3"; Filter LH=No; Filter RH=No; Height=18"; Induct Center C=9"; Induct Center D=18"; Induct Filter D=29 3/4"; Induction D=29"; Inlet Left=No; Inlet Right=Yes; Length=36"; Model=ESTS/DOAS; Radius=2 15/16"; Row F=8"; Second Pipe H=4 1/8"; URL=https://www.anemostat-hvac.com; Width=32"
- ESTS/DOAS 1/3-hp - 07L W/4ROW & Filter: Connect H=1 7/16"; Connect Length=4 1/2"; Connector for 6ROW LS=No; Connector for 6ROW RS=No; Description=DOAS SERIES FAN POWERED AIR TERMINAL; Diameter=6 7/8"; Discharge Height "Y"=11"; Discharge Width "X"=11 1/2"; Duct Inlet=3"; Filter LH=No; Filter RH=Yes; Height=18"; Induct Center C=9"; Induct Center D=18"; Induct Filter D=29 3/4"; Induction D=29"; Inlet Left=Yes; Inlet Right=No; Length=36"; Model=ESTS/DOAS; Radius=3 7/16"; Row F=6"; Second Pipe H=2 1/8"; URL=https://www.anemostat-hvac.com; Width=32"
- ESTS/DOAS 1/3-hp - 07L W/6ROW & Filter: Connect H=1 7/16"; Connect Length=4 1/2"; Connector for 6ROW LS=No; Connector for 6ROW RS=Yes; Description=DOAS SERIES FAN POWERED AIR TERMINAL; Diameter=6 7/8"; Discharge Height "Y"=11"; Discharge Width "X"=11 1/2"; Duct Inlet=3"; Filter LH=No; Filter RH=Yes; Height=18"; Induct Center C=9"; Induct Center D=18"; Induct Filter D=29 3/4"; Induction D=29"; Inlet Left=Yes; Inlet Right=No; Length=36"; Model=ESTS/DOAS; Radius=3 7/16"; Row F=8"; Second Pipe H=4 1/8"; URL=https://www.anemostat-hvac.com; Width=32"
- ESTS/DOAS 1/3-hp - 07L W/4ROW NO Filter: Connect H=1 7/16"; Connect Length=4 1/2"; Connector for 6ROW LS=No; Connector for 6ROW RS=No; Description=DOAS SERIES FAN POWERED AIR TERMINAL; Diameter=6 7/8"; Discharge Height "Y"=11"; Discharge Width "X"=11 1/2"; Duct Inlet=3"; Filter LH=No; Filter RH=No; Height=18"; Induct Center C=9"; Induct Center D=18"; Induct Filter D=29 3/4"; Induction D=29"; Inlet Left=Yes; Inlet Right=No; Length=36"; Model=ESTS/DOAS; Radius=3 7/16"; Row F=6"; Second Pipe H=2 1/8"; URL=https://www.anemostat-hvac.com; Width=32"
- ESTS/DOAS 1/3-hp - 07L W/6ROW NO Filter: Connect H=1 7/16"; Connect Length=4 1/2"; Connector for 6ROW LS=No; Connector for 6ROW RS=Yes; Description=DOAS SERIES FAN POWERED AIR TERMINAL; Diameter=6 7/8"; Discharge Height "Y"=11"; Discharge Width "X"=11 1/2"; Duct Inlet=3"; Filter LH=No; Filter RH=No; Height=18"; Induct Center C=9"; Induct Center D=18"; Induct Filter D=29 3/4"; Induction D=29"; Inlet Left=Yes; Inlet Right=No; Length=36"; Model=ESTS/DOAS; Radius=3 7/16"; Row F=8"; Second Pipe H=4 1/8"; URL=https://www.anemostat-hvac.com; Width=32"
- ESTS/DOAS 1/3-hp - 07R W/4ROW & Filter: Connect H=1 7/16"; Connect Length=4 1/2"; Connector for 6ROW LS=No; Connector for 6ROW RS=No; Description=DOAS SERIES FAN POWERED AIR TERMINAL; Diameter=6 7/8"; Discharge Height "Y"=11"; Discharge Width "X"=11 1/2"; Duct Inlet=3"; Filter LH=Yes; Filter RH=No; Height=18"; Induct Center C=9"; Induct Center D=18"; Induct Filter D=29 3/4"; Induction D=29"; Inlet Left=No; Inlet Right=Yes; Length=36"; Model=ESTS/DOAS; Radius=3 7/16"; Row F=6"; Second Pipe H=2 1/8"; URL=https://www.anemostat-hvac.com; Width=32"
- ESTS/DOAS 1/3-hp - 07R W/6ROW & Filter: Connect H=1 7/16"; Connect Length=4 1/2"; Connector for 6ROW LS=Yes; Connector for 6ROW RS=No; Description=DOAS SERIES FAN POWERED AIR TERMINAL; Diameter=6 7/8"; Discharge Height "Y"=11"; Discharge Width "X"=11 1/2"; Duct Inlet=3"; Filter LH=Yes; Filter RH=No; Height=18"; Induct Center C=9"; Induct Center D=18"; Induct Filter D=29 3/4"; Induction D=29"; Inlet Left=No; Inlet Right=Yes; Length=36"; Model=ESTS/DOAS; Radius=3 7/16"; Row F=8"; Second Pipe H=4 1/8"; URL=https://www.anemostat-hvac.com; Width=32"
- ESTS/DOAS 1/3-hp - 07R W/4ROW NO Filter: Connect H=1 7/16"; Connect Length=4 1/2"; Connector for 6ROW LS=No; Connector for 6ROW RS=No; Description=DOAS SERIES FAN POWERED AIR TERMINAL; Diameter=6 7/8"; Discharge Height "Y"=11"; Discharge Width "X"=11 1/2"; Duct Inlet=3"; Filter LH=No; Filter RH=No; Height=18"; Induct Center C=9"; Induct Center D=18"; Induct Filter D=29 3/4"; Induction D=29"; Inlet Left=No; Inlet Right=Yes; Length=36"; Model=ESTS/DOAS; Radius=3 7/16"; Row F=6"; Second Pipe H=2 1/8"; URL=https://www.anemostat-hvac.com; Width=32"
- ESTS/DOAS 1/3-hp - 07R W/6ROW NO Filter: Connect H=1 7/16"; Connect Length=4 1/2"; Connector for 6ROW LS=Yes; Connector for 6ROW RS=No; Description=DOAS SERIES FAN POWERED AIR TERMINAL; Diameter=6 7/8"; Discharge Height "Y"=11"; Discharge Width "X"=11 1/2"; Duct Inlet=3"; Filter LH=No; Filter RH=No; Height=18"; Induct Center C=9"; Induct Center D=18"; Induct Filter D=29 3/4"; Induction D=29"; Inlet Left=No; Inlet Right=Yes; Length=36"; Model=ESTS/DOAS; Radius=3 7/16"; Row F=8"; Second Pipe H=4 1/8"; URL=https://www.anemostat-hvac.com; Width=32"
- ESTS/DOAS 1/3-hp - 08L W/4ROW & Filter: Connect H=1 7/16"; Connect Length=4 1/2"; Connector for 6ROW LS=No; Connector for 6ROW RS=No; Description=DOAS SERIES FAN POWERED AIR TERMINAL; Diameter=7 7/8"; Discharge Height "Y"=11"; Discharge Width "X"=11 1/2"; Duct Inlet=4"; Filter LH=No; Filter RH=Yes; Height=18"; Induct Center C=9"; Induct Center D=18"; Induct Filter D=29 3/4"; Induction D=29"; Inlet Left=Yes; Inlet Right=No; Length=36"; Model=ESTS/DOAS; Radius=3 15/16"; Row F=6"; Second Pipe H=2 1/8"; URL=https://www.anemostat-hvac.com; Width=32"
- ESTS/DOAS 1/3-hp - 08L W/6ROW & Filter: Connect H=1 7/16"; Connect Length=4 1/2"; Connector for 6ROW LS=No; Connector for 6ROW RS=Yes; Description=DOAS SERIES FAN POWERED AIR TERMINAL; Diameter=7 7/8"; Discharge Height "Y"=11"; Discharge Width "X"=11 1/2"; Duct Inlet=4"; Filter LH=No; Filter RH=Yes; Height=18"; Induct Center C=9"; Induct Center D=18"; Induct Filter D=29 3/4"; Induction D=29"; Inlet Left=Yes; Inlet Right=No; Length=36"; Model=ESTS/DOAS; Radius=3 15/16"; Row F=8"; Second Pipe H=4 1/8"; URL=https://www.anemostat-hvac.com; Width=32"
- ESTS/DOAS 1/3-hp - 08L W/4ROW NO Filter: Connect H=1 7/16"; Connect Length=4 1/2"; Connector for 6ROW LS=No; Connector for 6ROW RS=No; Description=DOAS SERIES FAN POWERED AIR TERMINAL; Diameter=7 7/8"; Discharge Height "Y"=11"; Discharge Width "X"=11 1/2"; Duct Inlet=4"; Filter LH=No; Filter RH=No; Height=18"; Induct Center C=9"; Induct Center D=18"; Induct Filter D=29 3/4"; Induction D=29"; Inlet Left=Yes; Inlet Right=No; Length=36"; Model=ESTS/DOAS; Radius=3 15/16"; Row F=6"; Second Pipe H=2 1/8"; URL=https://www.anemostat-hvac.com; Width=32"
- ESTS/DOAS 1/3-hp - 08L W/6ROW NO Filter: Connect H=1 7/16"; Connect Length=4 1/2"; Connector for 6ROW LS=No; Connector for 6ROW RS=Yes; Description=DOAS SERIES FAN POWERED AIR TERMINAL; Diameter=7 7/8"; Discharge Height "Y"=11"; Discharge Width "X"=11 1/2"; Duct Inlet=4"; Filter LH=No; Filter RH=No; Height=18"; Induct Center C=9"; Induct Center D=18"; Induct Filter D=29 3/4"; Induction D=29"; Inlet Left=Yes; Inlet Right=No; Length=36"; Model=ESTS/DOAS; Radius=3 15/16"; Row F=8"; Second Pipe H=4 1/8"; URL=https://www.anemostat-hvac.com; Width=32"
- ESTS/DOAS 1/3-hp - 08R W/4ROW & Filter: Connect H=1 7/16"; Connect Length=4 1/2"; Connector for 6ROW LS=No; Connector for 6ROW RS=No; Description=DOAS SERIES FAN POWERED AIR TERMINAL; Diameter=7 7/8"; Discharge Height "Y"=11"; Discharge Width "X"=11 1/2"; Duct Inlet=4"; Filter LH=Yes; Filter RH=No; Height=18"; Induct Center C=9"; Induct Center D=18"; Induct Filter D=29 3/4"; Induction D=29"; Inlet Left=No; Inlet Right=Yes; Length=36"; Model=ESTS/DOAS; Radius=3 15/16"; Row F=6"; Second Pipe H=2 1/8"; URL=https://www.anemostat-hvac.com; Width=32"
- ESTS/DOAS 1/3-hp - 08R W/6ROW & Filter: Connect H=1 7/16"; Connect Length=4 1/2"; Connector for 6ROW LS=Yes; Connector for 6ROW RS=No; Description=DOAS SERIES FAN POWERED AIR TERMINAL; Diameter=7 7/8"; Discharge Height "Y"=11"; Discharge Width "X"=11 1/2"; Duct Inlet=4"; Filter LH=Yes; Filter RH=No; Height=18"; Induct Center C=9"; Induct Center D=18"; Induct Filter D=29 3/4"; Induction D=29"; Inlet Left=No; Inlet Right=Yes; Length=36"; Model=ESTS/DOAS; Radius=3 15/16"; Row F=8"; Second Pipe H=4 1/8"; URL=https://www.anemostat-hvac.com; Width=32"
- ESTS/DOAS 1/3-hp - 08R W/4ROW NO Filter: Connect H=1 7/16"; Connect Length=4 1/2"; Connector for 6ROW LS=No; Connector for 6ROW RS=No; Description=DOAS SERIES FAN POWERED AIR TERMINAL; Diameter=7 7/8"; Discharge Height "Y"=11"; Discharge Width "X"=11 1/2"; Duct Inlet=4"; Filter LH=No; Filter RH=No; Height=18"; Induct Center C=9"; Induct Center D=18"; Induct Filter D=29 3/4"; Induction D=29"; Inlet Left=No; Inlet Right=Yes; Length=36"; Model=ESTS/DOAS; Radius=3 15/16"; Row F=6"; Second Pipe H=2 1/8"; URL=https://www.anemostat-hvac.com; Width=32"
- ESTS/DOAS 1/3-hp - 08R W/6ROW NO Filter: Connect H=1 7/16"; Connect Length=4 1/2"; Connector for 6ROW LS=Yes; Connector for 6ROW RS=No; Description=DOAS SERIES FAN POWERED AIR TERMINAL; Diameter=7 7/8"; Discharge Height "Y"=11"; Discharge Width "X"=11 1/2"; Duct Inlet=4"; Filter LH=No; Filter RH=No; Height=18"; Induct Center C=9"; Induct Center D=18"; Induct Filter D=29 3/4"; Induction D=29"; Inlet Left=No; Inlet Right=Yes; Length=36"; Model=ESTS/DOAS; Radius=3 15/16"; Row F=8"; Second Pipe H=4 1/8"; URL=https://www.anemostat-hvac.com; Width=32"
- ESTS/DOAS 1/3-hp - 09L W/4ROW & Filter: Connect H=1 7/16"; Connect Length=4 1/2"; Connector for 6ROW LS=No; Connector for 6ROW RS=No; Description=DOAS SERIES FAN POWERED AIR TERMINAL; Diameter=8 7/8"; Discharge Height "Y"=11"; Discharge Width "X"=11 1/2"; Duct Inlet=4"; Filter LH=No; Filter RH=Yes; Height=18"; Induct Center C=9"; Induct Center D=18"; Induct Filter D=29 3/4"; Induction D=29"; Inlet Left=Yes; Inlet Right=No; Length=36"; Model=ESTS/DOAS; Radius=4 7/16"; Row F=6"; Second Pipe H=2 1/8"; URL=https://www.anemostat-hvac.com; Width=32"
- ESTS/DOAS 1/3-hp - 09L W/6ROW & Filter: Connect H=1 7/16"; Connect Length=4 1/2"; Connector for 6ROW LS=No; Connector for 6ROW RS=Yes; Description=DOAS SERIES FAN POWERED AIR TERMINAL; Diameter=8 7/8"; Discharge Height "Y"=11"; Discharge Width "X"=11 1/2"; Duct Inlet=4"; Filter LH=No; Filter RH=Yes; Height=18"; Induct Center C=9"; Induct Center D=18"; Induct Filter D=29 3/4"; Induction D=29"; Inlet Left=Yes; Inlet Right=No; Length=36"; Model=ESTS/DOAS; Radius=4 7/16"; Row F=8"; Second Pipe H=4 1/8"; URL=https://www.anemostat-hvac.com; Width=32"
- ESTS/DOAS 1/3-hp - 09L W/4ROW NO Filter: Connect H=1 7/16"; Connect Length=4 1/2"; Connector for 6ROW LS=No; Connector for 6ROW RS=No; Description=DOAS SERIES FAN POWERED AIR TERMINAL; Diameter=8 7/8"; Discharge Height "Y"=11"; Discharge Width "X"=11 1/2"; Duct Inlet=4"; Filter LH=No; Filter RH=No; Height=18"; Induct Center C=9"; Induct Center D=18"; Induct Filter D=29 3/4"; Induction D=29"; Inlet Left=Yes; Inlet Right=No; Length=36"; Model=ESTS/DOAS; Radius=4 7/16"; Row F=6"; Second Pipe H=2 1/8"; URL=https://www.anemostat-hvac.com; Width=32"
- ESTS/DOAS 1/3-hp - 09L W/6ROW NO Filter: Connect H=1 7/16"; Connect Length=4 1/2"; Connector for 6ROW LS=No; Connector for 6ROW RS=Yes; Description=DOAS SERIES FAN POWERED AIR TERMINAL; Diameter=8 7/8"; Discharge Height "Y"=11"; Discharge Width "X"=11 1/2"; Duct Inlet=4"; Filter LH=No; Filter RH=No; Height=18"; Induct Center C=9"; Induct Center D=18"; Induct Filter D=29 3/4"; Induction D=29"; Inlet Left=Yes; Inlet Right=No; Length=36"; Model=ESTS/DOAS; Radius=4 7/16"; Row F=8"; Second Pipe H=4 1/8"; URL=https://www.anemostat-hvac.com; Width=32"
- ESTS/DOAS 1/3-hp - 09R W/4ROW & Filter: Connect H=1 7/16"; Connect Length=4 1/2"; Connector for 6ROW LS=No; Connector for 6ROW RS=No; Description=DOAS SERIES FAN POWERED AIR TERMINAL; Diameter=8 7/8"; Discharge Height "Y"=11"; Discharge Width "X"=11 1/2"; Duct Inlet=4"; Filter LH=Yes; Filter RH=No; Height=18"; Induct Center C=9"; Induct Center D=18"; Induct Filter D=29 3/4"; Induction D=29"; Inlet Left=No; Inlet Right=Yes; Length=36"; Model=ESTS/DOAS; Radius=4 7/16"; Row F=6"; Second Pipe H=2 1/8"; URL=https://www.anemostat-hvac.com; Width=32"
- ESTS/DOAS 1/3-hp - 09R W/6ROW & Filter: Connect H=1 7/16"; Connect Length=4 1/2"; Connector for 6ROW LS=Yes; Connector for 6ROW RS=No; Description=DOAS SERIES FAN POWERED AIR TERMINAL; Diameter=8 7/8"; Discharge Height "Y"=11"; Discharge Width "X"=11 1/2"; Duct Inlet=4"; Filter LH=Yes; Filter RH=No; Height=18"; Induct Center C=9"; Induct Center D=18"; Induct Filter D=29 3/4"; Induction D=29"; Inlet Left=No; Inlet Right=Yes; Length=36"; Model=ESTS/DOAS; Radius=4 7/16"; Row F=8"; Second Pipe H=4 1/8"; URL=https://www.anemostat-hvac.com; Width=32"
- ESTS/DOAS 1/3-hp - 09R W/4ROW NO Filter: Connect H=1 7/16"; Connect Length=4 1/2"; Connector for 6ROW LS=No; Connector for 6ROW RS=No; Description=DOAS SERIES FAN POWERED AIR TERMINAL; Diameter=8 7/8"; Discharge Height "Y"=11"; Discharge Width "X"=11 1/2"; Duct Inlet=4"; Filter LH=No; Filter RH=No; Height=18"; Induct Center C=9"; Induct Center D=18"; Induct Filter D=29 3/4"; Induction D=29"; Inlet Left=No; Inlet Right=Yes; Length=36"; Model=ESTS/DOAS; Radius=4 7/16"; Row F=6"; Second Pipe H=2 1/8"; URL=https://www.anemostat-hvac.com; Width=32"
- ESTS/DOAS 1/3-hp - 09R W/6ROW NO Filter: Connect H=1 7/16"; Connect Length=4 1/2"; Connector for 6ROW LS=Yes; Connector for 6ROW RS=No; Description=DOAS SERIES FAN POWERED AIR TERMINAL; Diameter=8 7/8"; Discharge Height "Y"=11"; Discharge Width "X"=11 1/2"; Duct Inlet=4"; Filter LH=No; Filter RH=No; Height=18"; Induct Center C=9"; Induct Center D=18"; Induct Filter D=29 3/4"; Induction D=29"; Inlet Left=No; Inlet Right=Yes; Length=36"; Model=ESTS/DOAS; Radius=4 7/16"; Row F=8"; Second Pipe H=4 1/8"; URL=https://www.anemostat-hvac.com; Width=32"
- ESTS/DOAS 1/3-hp - 10L W/4ROW & Filter: Connect H=1 7/16"; Connect Length=4 1/2"; Connector for 6ROW LS=No; Connector for 6ROW RS=No; Description=DOAS SERIES FAN POWERED AIR TERMINAL; Diameter=9 7/8"; Discharge Height "Y"=11"; Discharge Width "X"=11 1/2"; Duct Inlet=5"; Filter LH=No; Filter RH=Yes; Height=18"; Induct Center C=9"; Induct Center D=18"; Induct Filter D=29 3/4"; Induction D=29"; Inlet Left=Yes; Inlet Right=No; Length=36"; Model=ESTS/DOAS; Radius=4 15/16"; Row F=6"; Second Pipe H=2 1/8"; URL=https://www.anemostat-hvac.com; Width=32"
- ESTS/DOAS 1/3-hp - 10L W/6ROW & Filter: Connect H=1 7/16"; Connect Length=4 1/2"; Connector for 6ROW LS=No; Connector for 6ROW RS=Yes; Description=DOAS SERIES FAN POWERED AIR TERMINAL; Diameter=9 7/8"; Discharge Height "Y"=11"; Discharge Width "X"=11 1/2"; Duct Inlet=5"; Filter LH=No; Filter RH=Yes; Height=18"; Induct Center C=9"; Induct Center D=18"; Induct Filter D=29 3/4"; Induction D=29"; Inlet Left=Yes; Inlet Right=No; Length=36"; Model=ESTS/DOAS; Radius=4 15/16"; Row F=8"; Second Pipe H=4 1/8"; URL=https://www.anemostat-hvac.com; Width=32"
- ESTS/DOAS 1/3-hp - 10L W/4ROW NO Filter: Connect H=1 7/16"; Connect Length=4 1/2"; Connector for 6ROW LS=No; Connector for 6ROW RS=No; Description=DOAS SERIES FAN POWERED AIR TERMINAL; Diameter=9 7/8"; Discharge Height "Y"=11"; Discharge Width "X"=11 1/2"; Duct Inlet=5"; Filter LH=No; Filter RH=No; Height=18"; Induct Center C=9"; Induct Center D=18"; Induct Filter D=29 3/4"; Induction D=29"; Inlet Left=Yes; Inlet Right=No; Length=36"; Model=ESTS/DOAS; Radius=4 15/16"; Row F=6"; Second Pipe H=2 1/8"; URL=https://www.anemostat-hvac.com; Width=32"
- ESTS/DOAS 1/3-hp - 10L W/6ROW NO Filter: Connect H=1 7/16"; Connect Length=4 1/2"; Connector for 6ROW LS=No; Connector for 6ROW RS=Yes; Description=DOAS SERIES FAN POWERED AIR TERMINAL; Diameter=9 7/8"; Discharge Height "Y"=11"; Discharge Width "X"=11 1/2"; Duct Inlet=5"; Filter LH=No; Filter RH=No; Height=18"; Induct Center C=9"; Induct Center D=18"; Induct Filter D=29 3/4"; Induction D=29"; Inlet Left=Yes; Inlet Right=No; Length=36"; Model=ESTS/DOAS; Radius=4 15/16"; Row F=8"; Second Pipe H=4 1/8"; URL=https://www.anemostat-hvac.com; Width=32"
- ESTS/DOAS 1/3-hp - 10R W/4ROW & Filter: Connect H=1 7/16"; Connect Length=4 1/2"; Connector for 6ROW LS=No; Connector for 6ROW RS=No; Description=DOAS SERIES FAN POWERED AIR TERMINAL; Diameter=9 7/8"; Discharge Height "Y"=11"; Discharge Width "X"=11 1/2"; Duct Inlet=5"; Filter LH=Yes; Filter RH=No; Height=18"; Induct Center C=9"; Induct Center D=18"; Induct Filter D=29 3/4"; Induction D=29"; Inlet Left=No; Inlet Right=Yes; Length=36"; Model=ESTS/DOAS; Radius=4 15/16"; Row F=6"; Second Pipe H=2 1/8"; URL=https://www.anemostat-hvac.com; Width=32"
- ESTS/DOAS 1/3-hp - 10R W/6ROW & Filter: Connect H=1 7/16"; Connect Length=4 1/2"; Connector for 6ROW LS=Yes; Connector for 6ROW RS=No; Description=DOAS SERIES FAN POWERED AIR TERMINAL; Diameter=9 7/8"; Discharge Height "Y"=11"; Discharge Width "X"=11 1/2"; Duct Inlet=5"; Filter LH=Yes; Filter RH=No; Height=18"; Induct Center C=9"; Induct Center D=18"; Induct Filter D=29 3/4"; Induction D=29"; Inlet Left=No; Inlet Right=Yes; Length=36"; Model=ESTS/DOAS; Radius=4 15/16"; Row F=8"; Second Pipe H=4 1/8"; URL=https://www.anemostat-hvac.com; Width=32"
- ESTS/DOAS 1/3-hp - 10R W/4ROW NO Filter: Connect H=1 7/16"; Connect Length=4 1/2"; Connector for 6ROW LS=No; Connector for 6ROW RS=No; Description=DOAS SERIES FAN POWERED AIR TERMINAL; Diameter=9 7/8"; Discharge Height "Y"=11"; Discharge Width "X"=11 1/2"; Duct Inlet=5"; Filter LH=No; Filter RH=No; Height=18"; Induct Center C=9"; Induct Center D=18"; Induct Filter D=29 3/4"; Induction D=29"; Inlet Left=No; Inlet Right=Yes; Length=36"; Model=ESTS/DOAS; Radius=4 15/16"; Row F=6"; Second Pipe H=2 1/8"; URL=https://www.anemostat-hvac.com; Width=32"
- ESTS/DOAS 1/3-hp - 10R W/6ROW NO Filter: Connect H=1 7/16"; Connect Length=4 1/2"; Connector for 6ROW LS=Yes; Connector for 6ROW RS=No; Description=DOAS SERIES FAN POWERED AIR TERMINAL; Diameter=9 7/8"; Discharge Height "Y"=11"; Discharge Width "X"=11 1/2"; Duct Inlet=5"; Filter LH=No; Filter RH=No; Height=18"; Induct Center C=9"; Induct Center D=18"; Induct Filter D=29 3/4"; Induction D=29"; Inlet Left=No; Inlet Right=Yes; Length=36"; Model=ESTS/DOAS; Radius=4 15/16"; Row F=8"; Second Pipe H=4 1/8"; URL=https://www.anemostat-hvac.com; Width=32"

## geometry (parser evidence)
native form markers: Sweep x1
no freeform markers — native parametric forms only
